FCSTD DOCUMENT  (FreeCAD 0.18R16131 (Git))
Label: Escriba
License: All rights reserved
LicenseURL: http://en.wikipedia.org/wiki/All_rights_reserved
objects: Part::Feature×205, Sketcher::SketchObject×65, App::Part×62, Part::Cylinder×43, Part::Cut×39, PartDesign::Pocket×28, Part::FeaturePython×28, Part::Box×26, Part::Chamfer×22, PartDesign::Pad×16, App::DocumentObjectGroup×14, Part::Revolution×13, Part::MultiFuse×8, PartDesign::Chamfer×8, PartDesign::Revolution×8, Part::Fuse×6, Part::Compound×1, Part::Fillet×1, Mesh::Feature×1
note: 569 computed .brp shape members not serialized (recipe doc carries the construction recipe); baked Part::Feature solids carry a one-line shape summary decoded from their .brp

FEATURE [Part::Cylinder] Cylinder  label="Rod-001"
  Angle = 360
  AttacherType = Attacher::AttachEngine3D
  Height = 500
  Placement = pos=(90,23,26) rot=(0,1,0;1.5708rad)
  Radius = 4
FEATURE [Part::Cylinder] Cylinder001  label="Rod-002"
  Angle = 360
  AttacherType = Attacher::AttachEngine3D
  Height = 500
  Placement = pos=(90,97,26) rot=(0,1,0;1.5708rad)
  Radius = 4
FEATURE [Part::Cylinder] Cylinder002  label="Rod-003"
  Angle = 360
  AttacherType = Attacher::AttachEngine3D
  Height = 350
  Placement = pos=(18,336,14.75) rot=(1,0,0;1.5708rad)
  Radius = 4
FEATURE [Part::Cylinder] Cylinder003  label="Rod-004"
  Angle = 360
  AttacherType = Attacher::AttachEngine3D
  Height = 350
  Placement = pos=(53,336,14.75) rot=(1,0,0;1.5708rad)
  Radius = 4
FEATURE [Part::Compound] Compound001  label="extruder-motor"
  Placement = pos=(109.65,-100.5,-442) rot=(0,0,1;0rad)
FEATURE [Sketcher::SketchObject] Sketch007  label="bottom-part-sketch"
  MapMode = 5
  sketch-geometry (8):
    g0: LineSegment StartX=-16.65 StartY=-21.15 StartZ=0 EndX=16.65 EndY=-21.15 EndZ=0
    g1: LineSegment StartX=21.15 StartY=-16.65 StartZ=0 EndX=21.15 EndY=16.65 EndZ=0
    g2: LineSegment StartX=16.65 StartY=21.15 StartZ=0 EndX=-16.65 EndY=21.15 EndZ=0
    g3: LineSegment StartX=-21.15 StartY=16.65 StartZ=0 EndX=-21.15 EndY=-16.65 EndZ=0
    g4: ArcOfCircle CenterX=0 CenterY=0 CenterZ=0 NormalX=0 NormalY=0 NormalZ=1 AngleXU=0 Radius=26.9174 StartAngle=2.2377 EndAngle=2.47468
    g5: ArcOfCircle CenterX=0 CenterY=0 CenterZ=0 NormalX=0 NormalY=0 NormalZ=1 AngleXU=0 Radius=26.9174 StartAngle=3.8085 EndAngle=4.04548
    g6: ArcOfCircle CenterX=0 CenterY=0 CenterZ=0 NormalX=0 NormalY=0 NormalZ=1 AngleXU=0 Radius=26.9174 StartAngle=5.3793 EndAngle=5.61628
    g7: ArcOfCircle CenterX=0 CenterY=0 CenterZ=0 NormalX=0 NormalY=0 NormalZ=1 AngleXU=0 Radius=26.9174 StartAngle=0.666908 EndAngle=0.903888
  constraints (29):
    c: Horizontal(g0)
    c: Horizontal(g2)
    c: Vertical(g1)
    c: Vertical(g3)
    c: PointOnObject(g0,g4)
    c: PointOnObject(g0,g4)
    c: PointOnObject(g1,g4)
    c: PointOnObject(g1,g4)
    c: Coincident(g4,g2)
    c: Coincident(g7,g2)
    c: Equal(g4,g5)
    c: Coincident(g4,g3)
    c: Coincident(g5,g3)
    c: Coincident(g4,g5)
    c: Equal(g5,g6)
    c: PointOnObject(g5,g0)
    c: PointOnObject(g6,g0)
    c: Coincident(g5,g6)
    c: Equal(g6,g7)
    c: PointOnObject(g6,g1)
    c: PointOnObject(g7,g1)
    c: Coincident(g6,g7)
    c: Equal(g3,g2)
    c: Equal(g2,g1)
    c: Equal(g1,g0)
    c: DistanceX(g3,g1) = 42.3
    c: DistanceX(g2) = -33.3
    c: DistanceY(g2) = 21.15
    c: DistanceX(g1) = 21.15
FEATURE [PartDesign::Pad] Pad002  label="bottom-slice"
  Length = 9.6
  Length2 = 100
  Profile = -> Sketch007
  Type = 0
FEATURE [Sketcher::SketchObject] Sketch008  label="middle-part-sketch"
  ExternalGeometry = -> [Pad002]
  MapMode = 5
  Placement = pos=(0,0,9.6) rot=(0,0,1;0rad)
  Support = -> [Pad002]
  sketch-geometry (9):
    g0: LineSegment StartX=-21 StartY=-13.75 StartZ=0 EndX=-21 EndY=13.75 EndZ=0
    g1: LineSegment StartX=-21 StartY=13.75 StartZ=0 EndX=-13.75 EndY=21 EndZ=0
    g2: LineSegment StartX=-13.75 StartY=21 StartZ=0 EndX=13.75 EndY=21 EndZ=0
    g3: LineSegment [constr] StartX=-21 StartY=13.75 StartZ=0 EndX=-9 EndY=13.75 EndZ=0
    g4: LineSegment StartX=13.75 StartY=21 StartZ=0 EndX=21 EndY=13.75 EndZ=0
    g5: LineSegment StartX=21 StartY=13.75 StartZ=0 EndX=21 EndY=-13.75 EndZ=0
    g6: LineSegment StartX=21 StartY=-13.75 StartZ=0 EndX=13.75 EndY=-21 EndZ=0
    g7: LineSegment StartX=13.75 StartY=-21 StartZ=0 EndX=-13.75 EndY=-21 EndZ=0
    g8: LineSegment StartX=-13.75 StartY=-21 StartZ=0 EndX=-21 EndY=-13.75 EndZ=0
  constraints (24):
    c: Coincident(g0,g1)
    c: Coincident(g1,g2)
    c: Horizontal(g2)
    c: Symmetric(g0,g0,g-1)
    c: Symmetric(g1,g2,g-2)
    c: Horizontal(g3)
    c: Coincident(g3,g0)
    c: DistanceX(g3) = 12
    c: Angle(g3,g1) = 0.785398
    c: DistanceY(g0) = 27.5
    c: Coincident(g4,g5)
    c: Vertical(g5)
    c: Coincident(g5,g6)
    c: Coincident(g6,g7)
    c: Horizontal(g7)
    c: Coincident(g7,g8)
    c: Coincident(g8,g0)
    c: Symmetric(g1,g7,g-1)
    c: Coincident(g4,g2)
    c: Symmetric(g4,g0,g-2)
    c: Symmetric(g0,g5,g-2)
    c: Symmetric(g6,g7,g-2)
    c: DistanceX(g-1,g0) = -21
    c: Equal(g0,g2)
FEATURE [PartDesign::Pad] Pad003  label="middle-slice"
  Length = 22.75
  Length2 = 100
  Profile = -> Sketch008
  Type = 0
FEATURE [Sketcher::SketchObject] Sketch009  label="top-part-sketch"
  MapMode = 5
  Placement = pos=(0,0,32.35) rot=(0,0,1;0rad)
  Support = -> [Pad003]
  sketch-geometry (8):
    g0: LineSegment StartX=-16.65 StartY=-21.15 StartZ=0 EndX=16.65 EndY=-21.15 EndZ=0
    g1: LineSegment StartX=21.15 StartY=-16.65 StartZ=0 EndX=21.15 EndY=16.65 EndZ=0
    g2: LineSegment StartX=16.65 StartY=21.15 StartZ=0 EndX=-16.65 EndY=21.15 EndZ=0
    g3: LineSegment StartX=-21.15 StartY=16.65 StartZ=0 EndX=-21.15 EndY=-16.65 EndZ=0
    g4: ArcOfCircle CenterX=0 CenterY=0 CenterZ=0 NormalX=0 NormalY=0 NormalZ=1 AngleXU=0 Radius=26.9174 StartAngle=2.2377 EndAngle=2.47468
    g5: ArcOfCircle CenterX=0 CenterY=0 CenterZ=0 NormalX=0 NormalY=0 NormalZ=1 AngleXU=0 Radius=26.9174 StartAngle=3.8085 EndAngle=4.04548
    g6: ArcOfCircle CenterX=0 CenterY=0 CenterZ=0 NormalX=0 NormalY=0 NormalZ=1 AngleXU=0 Radius=26.9174 StartAngle=5.3793 EndAngle=5.61628
    g7: ArcOfCircle CenterX=0 CenterY=0 CenterZ=0 NormalX=0 NormalY=0 NormalZ=1 AngleXU=0 Radius=26.9174 StartAngle=0.666908 EndAngle=0.903888
  constraints (29):
    c: Horizontal(g0)
    c: Horizontal(g2)
    c: Vertical(g1)
    c: Vertical(g3)
    c: PointOnObject(g0,g4)
    c: PointOnObject(g0,g4)
    c: PointOnObject(g1,g4)
    c: PointOnObject(g1,g4)
    c: Coincident(g4,g2)
    c: Coincident(g7,g2)
    c: Equal(g4,g5)
    c: Coincident(g4,g3)
    c: Coincident(g5,g3)
    c: Coincident(g4,g5)
    c: Equal(g5,g6)
    c: PointOnObject(g5,g0)
    c: PointOnObject(g6,g0)
    c: Coincident(g5,g6)
    c: Equal(g6,g7)
    c: PointOnObject(g6,g1)
    c: PointOnObject(g7,g1)
    c: Coincident(g6,g7)
    c: Equal(g3,g2)
    c: Equal(g2,g1)
    c: Equal(g1,g0)
    c: DistanceX(g3,g1) = 42.3
    c: DistanceX(g2) = -33.3
    c: DistanceY(g2) = 21.15
    c: DistanceX(g1) = 21.15
FEATURE [PartDesign::Pad] Pad004  label="top-slice"
  Length = 7.75
  Length2 = 100
  Profile = -> Sketch009
  Type = 0
FEATURE [Sketcher::SketchObject] Sketch010  label="top-drills-sketch"
  MapMode = 5
  Placement = pos=(0,0,40.1) rot=(0,0,1;0rad)
  Support = -> [Pad004]
  sketch-geometry (6):
    g0: LineSegment [constr] StartX=-15.5 StartY=15.5 StartZ=0 EndX=15.5 EndY=15.5 EndZ=0
    g1: LineSegment [constr] StartX=-15.5 StartY=15.5 StartZ=0 EndX=-15.5 EndY=-15.5 EndZ=0
    g2: Circle CenterX=-15.5 CenterY=15.5 CenterZ=0 NormalX=0 NormalY=0 NormalZ=1 AngleXU=0 Radius=1.225
    g3: Circle CenterX=15.5 CenterY=15.5 CenterZ=0 NormalX=0 NormalY=0 NormalZ=1 AngleXU=0 Radius=1.225
    g4: Circle CenterX=15.5 CenterY=-15.5 CenterZ=0 NormalX=0 NormalY=0 NormalZ=1 AngleXU=0 Radius=1.225
    g5: Circle CenterX=-15.5 CenterY=-15.5 CenterZ=0 NormalX=0 NormalY=0 NormalZ=1 AngleXU=0 Radius=1.225
  constraints (15):
    c: Horizontal(g0)
    c: Symmetric(g0,g0,g-2)
    c: Vertical(g1)
    c: Symmetric(g1,g1,g-1)
    c: Equal(g0,g1)
    c: DistanceX(g0) = 31
    c: Coincident(g1,g0)
    c: Radius(g2) = 1.225
    c: Coincident(g2,g0)
    c: Equal(g5,g4)
    c: Equal(g4,g3)
    c: Equal(g3,g2)
    c: Coincident(g3,g0)
    c: Coincident(g5,g1)
    c: Symmetric(g4,g1,g-2)
FEATURE [PartDesign::Pocket] Pocket003  label="top-drills"
  Length = 4.5
  Length2 = 100
  Profile = -> Sketch010
  Type = 0
FEATURE [Sketcher::SketchObject] Sketch011  label="shaft-base-sketch"
  MapMode = 5
  Placement = pos=(0,0,40.1) rot=(0,0,1;0rad)
  Support = -> [Pocket003]
  sketch-geometry (2):
    g0: Circle CenterX=0 CenterY=0 CenterZ=0 NormalX=0 NormalY=0 NormalZ=1 AngleXU=0 Radius=11
    g1: Circle CenterX=0 CenterY=0 CenterZ=0 NormalX=0 NormalY=0 NormalZ=1 AngleXU=0 Radius=5
  constraints (4):
    c: Coincident(g0,g-1)
    c: Radius(g0) = 11
    c: Coincident(g1,g-1)
    c: Radius(g1) = 5
FEATURE [PartDesign::Pad] Pad005  label="shaft-base"
  Length = 2
  Length2 = 100
  Profile = -> Sketch011
  Type = 0
FEATURE [Sketcher::SketchObject] Sketch012  label="shaft-1-sketch"
  MapMode = 5
  Placement = pos=(0,0,40.1) rot=(0,0,1;0rad)
  Support = -> [Pad005]
  sketch-geometry (1):
    g0: Circle CenterX=0 CenterY=0 CenterZ=0 NormalX=0 NormalY=0 NormalZ=1 AngleXU=0 Radius=2.5
  constraints (2):
    c: Coincident(g0,g-1)
    c: Radius(g0) = 2.5
FEATURE [PartDesign::Pad] Pad006  label="shaft-1"
  Length = 20
  Length2 = 100
  Profile = -> Sketch012
  Type = 0
FEATURE [Sketcher::SketchObject] Sketch013  label="shaft-2-sketch"
  ExternalGeometry = -> [Pad006]
  MapMode = 5
  Placement = pos=(0,0,60.1) rot=(0,0,1;0rad)
  Support = -> [Pad006]
  sketch-geometry (4):
    g0: LineSegment StartX=-2 StartY=1.5 StartZ=0 EndX=-2 EndY=-1.5 EndZ=0
    g1: LineSegment StartX=-2 StartY=1.5 StartZ=0 EndX=-2.5 EndY=1.5 EndZ=0
    g2: LineSegment StartX=-2.5 StartY=1.5 StartZ=0 EndX=-2.5 EndY=-1.5 EndZ=0
    g3: LineSegment StartX=-2.5 StartY=-1.5 StartZ=0 EndX=-2 EndY=-1.5 EndZ=0
  constraints (12):
    c: Vertical(g0)
    c: Symmetric(g0,g0,g-1)
    c: PointOnObject(g0,g-3)
    c: Coincident(g1,g2)
    c: Coincident(g2,g3)
    c: Horizontal(g3)
    c: Horizontal(g1)
    c: Coincident(g1,g0)
    c: Coincident(g0,g3)
    c: Vertical(g2)
    c: Tangent(g2,g-3)
    c: DistanceX(g1) = -0.5
FEATURE [PartDesign::Pocket] Pocket004  label="shaft-2"
  Length = 17
  Length2 = 100
  Profile = -> Sketch013
  Type = 0
FEATURE [Sketcher::SketchObject] Sketch014  label="bottom-drills-sketch"
  MapMode = 5
  Placement = pos=(0,0,0) rot=(1,0,0;3.14159rad)
  Support = -> [Pocket004]
  sketch-geometry (7):
    g0: LineSegment [constr] StartX=-15.5 StartY=15.5 StartZ=0 EndX=15.5 EndY=15.5 EndZ=0
    g1: LineSegment [constr] StartX=-15.5 StartY=15.5 StartZ=0 EndX=-15.5 EndY=-15.5 EndZ=0
    g2: Circle CenterX=-15.5 CenterY=15.5 CenterZ=0 NormalX=0 NormalY=0 NormalZ=1 AngleXU=0 Radius=1.5
    g3: Circle CenterX=15.5 CenterY=15.5 CenterZ=0 NormalX=0 NormalY=0 NormalZ=1 AngleXU=0 Radius=1.5
    g4: Circle CenterX=15.5 CenterY=-15.5 CenterZ=0 NormalX=0 NormalY=0 NormalZ=1 AngleXU=0 Radius=1.5
    g5: Circle CenterX=-15.5 CenterY=-15.5 CenterZ=0 NormalX=0 NormalY=0 NormalZ=1 AngleXU=0 Radius=1.5
    g6: Circle CenterX=0 CenterY=0 CenterZ=0 NormalX=0 NormalY=0 NormalZ=1 AngleXU=0 Radius=4.5
  constraints (17):
    c: Horizontal(g0)
    c: Vertical(g1)
    c: Coincident(g1,g0)
    c: Symmetric(g0,g0,g-2)
    c: Symmetric(g0,g1,g-1)
    c: Equal(g1,g0)
    c: DistanceX(g0) = 31
    c: Coincident(g2,g0)
    c: Radius(g2) = 1.5
    c: Coincident(g5,g1)
    c: Coincident(g0,g3)
    c: Equal(g3,g2)
    c: Equal(g2,g5)
    c: Equal(g5,g4)
    c: Symmetric(g4,g1,g-2)
    c: Coincident(g6,g-1)
    c: Radius(g6) = 4.5
FEATURE [PartDesign::Pocket] Pocket005  label="bottom-drills"
  Length = 3
  Length2 = 100
  Profile = -> Sketch014
  Type = 0
FEATURE [Part::Chamfer] Chamfer004  label="motor-no-connector"
  Base = -> Pocket005
  Edges = 1 edges r=0.4: [Edge102]
FEATURE [Sketcher::SketchObject] Sketch015  label="connector-support-sketch"
  ExternalGeometry = -> [Chamfer004]
  MapMode = 5
  Placement = pos=(0,0,43.1) rot=(0,0,1;0rad)
  Support = -> [Chamfer004]
  sketch-geometry (4):
    g0: LineSegment StartX=21.15 StartY=8.2 StartZ=0 EndX=25.45 EndY=8.2 EndZ=0
    g1: LineSegment StartX=25.45 StartY=8.2 StartZ=0 EndX=25.45 EndY=-8.2 EndZ=0
    g2: LineSegment StartX=25.45 StartY=-8.2 StartZ=0 EndX=21.15 EndY=-8.2 EndZ=0
    g3: LineSegment StartX=21.15 StartY=-8.2 StartZ=0 EndX=21.15 EndY=8.2 EndZ=0
  constraints (12):
    c: Coincident(g0,g1)
    c: Coincident(g1,g2)
    c: Coincident(g2,g3)
    c: Coincident(g3,g0)
    c: Horizontal(g0)
    c: Horizontal(g2)
    c: Vertical(g1)
    c: Vertical(g3)
    c: Symmetric(g0,g2,g-1)
    c: PointOnObject(g0,g-3)
    c: DistanceY(g1) = -16.4
    c: DistanceX(g0) = 4.3
FEATURE [PartDesign::Pad] Pad007  label="connector-motor"
  Length = 3.6
  Length2 = 100
  Profile = -> Sketch015
  Reversed = true
  Type = 0
FEATURE [Sketcher::SketchObject] Sketch016  label="connector-slot-sketch"
  ExternalGeometry = -> [Pad007]
  MapMode = 5
  Placement = pos=(21.15,0,0) rot=(0.57735,-0.57735,-0.57735;2.0944rad)
  Support = -> [Pad007]
  sketch-geometry (4):
    g0: LineSegment StartX=-8.2 StartY=9.6 StartZ=0 EndX=8.2 EndY=9.6 EndZ=0
    g1: LineSegment StartX=8.2 StartY=9.6 StartZ=0 EndX=8.2 EndY=3.6 EndZ=0
    g2: LineSegment StartX=8.2 StartY=3.6 StartZ=0 EndX=-8.2 EndY=3.6 EndZ=0
    g3: LineSegment StartX=-8.2 StartY=3.6 StartZ=0 EndX=-8.2 EndY=9.6 EndZ=0
  constraints (11):
    c: Coincident(g0,g1)
    c: Coincident(g1,g2)
    c: Coincident(g2,g3)
    c: Coincident(g3,g0)
    c: Horizontal(g0)
    c: Horizontal(g2)
    c: Vertical(g1)
    c: Vertical(g3)
    c: Coincident(g2,g-3)
    c: Coincident(g1,g-3)
    c: PointOnObject(g0,g-4)
FEATURE [PartDesign::Pocket] Pocket006  label="connector-slot"
  Length = 1
  Length2 = 100
  Profile = -> Sketch016
  Type = 0
FEATURE [Sketcher::SketchObject] Sketch017  label="connector-main-body-sketch"
  MapMode = 5
  Placement = pos=(0,0,0) rot=(0.57735,0.57735,0.57735;2.0944rad)
  sketch-geometry (4):
    g0: LineSegment StartX=-7.5 StartY=3.05 StartZ=0 EndX=7.5 EndY=3.05 EndZ=0
    g1: LineSegment StartX=7.5 StartY=3.05 StartZ=0 EndX=7.5 EndY=-3.05 EndZ=0
    g2: LineSegment StartX=7.5 StartY=-3.05 StartZ=0 EndX=-7.5 EndY=-3.05 EndZ=0
    g3: LineSegment StartX=-7.5 StartY=-3.05 StartZ=0 EndX=-7.5 EndY=3.05 EndZ=0
  constraints (11):
    c: Coincident(g0,g1)
    c: Coincident(g1,g2)
    c: Coincident(g2,g3)
    c: Coincident(g3,g0)
    c: Horizontal(g0)
    c: Horizontal(g2)
    c: Vertical(g1)
    c: Vertical(g3)
    c: Symmetric(g0,g1,g-1)
    c: DistanceX(g0) = 15
    c: DistanceY(g1) = -6.1
FEATURE [PartDesign::Pad] Pad008  label="connector-main-body"
  Length = 6.7
  Length2 = 100
  Placement = pos=(0,0,0) rot=(0.57735,0.57735,0.57735;2.0944rad)
  Profile = -> Sketch017
  Type = 0
FEATURE [Sketcher::SketchObject] Sketch018  label="connector-cutout-1-sketch"
  MapMode = 5
  Placement = pos=(6.7,0,0) rot=(0.57735,0.57735,0.57735;2.0944rad)
  Support = -> [Pad008]
  sketch-geometry (8):
    g0: LineSegment StartX=-6.5 StartY=1.85 StartZ=0 EndX=-3.22738 EndY=1.85 EndZ=0
    g1: LineSegment StartX=6.5 StartY=1.85 StartZ=0 EndX=6.5 EndY=-1.85 EndZ=0
    g2: LineSegment StartX=6.5 StartY=-1.85 StartZ=0 EndX=-6.5 EndY=-1.85 EndZ=0
    g3: LineSegment StartX=-6.5 StartY=-1.85 StartZ=0 EndX=-6.5 EndY=1.85 EndZ=0
    g4: LineSegment StartX=-3.22738 StartY=1.85 StartZ=0 EndX=-3.22738 EndY=3.85 EndZ=0
    g5: LineSegment StartX=-3.22738 StartY=3.85 StartZ=0 EndX=3.22738 EndY=3.85 EndZ=0
    g6: LineSegment StartX=3.22738 StartY=3.85 StartZ=0 EndX=3.22738 EndY=1.85 EndZ=0
    g7: LineSegment StartX=3.22738 StartY=1.85 StartZ=0 EndX=6.5 EndY=1.85 EndZ=0
  constraints (21):
    c: Coincident(g7,g1)
    c: Coincident(g1,g2)
    c: Coincident(g2,g3)
    c: Coincident(g3,g0)
    c: Horizontal(g0)
    c: Horizontal(g2)
    c: Vertical(g1)
    c: Vertical(g3)
    c: Symmetric(g0,g1,g-1)
    c: DistanceX(g2) = -13
    c: DistanceY(g1) = -3.7
    c: Vertical(g4)
    c: Coincident(g4,g5)
    c: Horizontal(g5)
    c: Coincident(g5,g6)
    c: Vertical(g6)
    c: Symmetric(g4,g5,g-2)
    c: Coincident(g0,g4)
    c: Coincident(g7,g6)
    c: Tangent(g0,g7)
    c: DistanceY(g6) = -2
FEATURE [PartDesign::Pocket] Pocket007  label="connector-cutout-1"
  Length = 4.6
  Length2 = 100
  Placement = pos=(0,0,0) rot=(0.57735,0.57735,0.57735;2.0944rad)
  Profile = -> Sketch018
  Type = 0
FEATURE [Part::Box] Box  label="pin-master"
  AttacherType = Attacher::AttachEngine3D
  Height = 0.5
  Length = 4
  Width = 0.5
FEATURE [Part::FeaturePython] Array  label="pins"  # Draft array (typed FeaturePython)
  Angle = 360
  ArrayType = 0
  Axis = (0,0,1)
  Base = -> Box
  Center = (0,0,0)
  IntervalX = (1,0,0)
  IntervalY = (0,2,0)
  IntervalZ = (0,0,1)
  NumberPolar = 1
  NumberX = 1
  NumberY = 6
  NumberZ = 1
  Placement = pos=(2,-5.3,0) rot=(0,0,1;0rad)
FEATURE [App::DocumentObjectGroup] Group  label="connector-src"
  Group = -> [Pad008,Pocket007,Array]
FEATURE [Part::MultiFuse] Fusion001  label="connector"
  Placement = pos=(20.15,1e-15,6.65) rot=(0,0,1;0rad)
  Shapes = -> [Pocket007,Array]
FEATURE [Part::MultiFuse] Fusion002  label="Motor-with-connector"
  Shapes = -> [Pocket006,Fusion001]
FEATURE [Part::Feature] Fusion001001  label="Motor-with-connector-final002"
  Placement = pos=(509,0,0) rot=(0.707107,0.707107,0;3.14159rad)
  shape: bbox 42.3 x 48 x 60.1 mm, 110 faces (baked)
FEATURE [Part::Feature] Fusion001002  label="Motor-with-connector-final001"
  Placement = pos=(-3,0,0) rot=(0.707107,0.707107,0;3.14159rad)
  shape: bbox 42.3 x 48 x 60.1 mm, 110 faces (baked)
FEATURE [App::Part] Part003  label="Steppers"
  Group = -> [Compound001,Group,Pocket006,Fusion001,Sketch008,Sketch014,Pad002,Sketch007,Pad007,Pocket004,Sketch017,Sketch015,Sketch016,Sketch013,Sketch009,Chamfer004,Sketch010,Pad003,Sketch012,Pocket007,Sketch011,Pad008,Box,Pad004,Pad006,Pocket003,Pad005,Array,Sketch018,Pocket005,Fusion002,Fusion001001,Fusion001002]
  License = CC BY 3.0
  LicenseURL = http://creativecommons.org/licenses/by/3.0/
  Origin = -> Origin003
  Placement = pos=(97.85,60,108.6) rot=(0,0,1;0rad)
FEATURE [Part::Box] Box001  label="Cubo"
  AttacherType = Attacher::AttachEngine3D
  Height = 22.7
  Length = 11.8
  Width = 22.5
FEATURE [Part::Box] Box002  label="Cubo001"
  AttacherType = Attacher::AttachEngine3D
  Height = 2.5
  Length = 11.8
  Placement = pos=(0,-4.7,15.9) rot=(0,0,1;0rad)
  Width = 32.4
FEATURE [Part::Fuse] Fusion001003  label="Square_body"
  Base = -> Box001
  Tool = -> Box002
FEATURE [Part::Cylinder] Cylinder006  label="Cilindro"
  Angle = 360
  AttacherType = Attacher::AttachEngine3D
  Height = 4
  Placement = pos=(5.9,16.6,22.7) rot=(0,0,1;0rad)
  Radius = 5.9
FEATURE [Part::Cylinder] Cylinder007  label="Cilindro001"
  Angle = 360
  AttacherType = Attacher::AttachEngine3D
  Height = 4
  Placement = pos=(5.9,10.3,22.7) rot=(0,0,1;0rad)
  Radius = 2.5
FEATURE [Part::Fuse] Fusion001004
  Base = -> Cylinder006
  Tool = -> Cylinder007
FEATURE [Part::Fuse] Fusion003
  Base = -> Fusion001003
  Tool = -> Fusion001004
FEATURE [Part::Cylinder] Cylinder008  label="Taladro"
  Angle = 360
  AttacherType = Attacher::AttachEngine3D
  Height = 10
  Placement = pos=(5.9,-2.35,11) rot=(0,0,1;0rad)
  Radius = 1
FEATURE [Part::Cylinder] Cylinder009  label="Taladro2"
  Angle = 360
  AttacherType = Attacher::AttachEngine3D
  Height = 10
  Placement = pos=(5.9,24.85,11) rot=(0,0,1;0rad)
  Radius = 1
FEATURE [Part::Fuse] Fusion004  label="Taladros"
  Base = -> Cylinder008
  Tool = -> Cylinder009
FEATURE [Part::Box] Box003  label="Cubo002"
  AttacherType = Attacher::AttachEngine3D
  Height = 10
  Length = 1.3
  Placement = pos=(5.25,-6,12) rot=(0,0,1;0rad)
  Width = 3.3
FEATURE [Part::Box] Box004  label="Cubo003"
  AttacherType = Attacher::AttachEngine3D
  Height = 10
  Length = 1.3
  Placement = pos=(5.25,25,12) rot=(0,0,1;0rad)
  Width = 3.3
FEATURE [Part::Fuse] Fusion005  label="Rebajes"
  Base = -> Box003
  Tool = -> Box004
FEATURE [Part::Fuse] Fusion006  label="Taladros001"
  Base = -> Fusion004
  Tool = -> Fusion005
FEATURE [Part::Cut] Cut002  label="Cuerpo_con_taladros"
  Base = -> Fusion003
  Placement = pos=(-5.9,0,0) rot=(0,0,1;0rad)
  Tool = -> Fusion006
FEATURE [Sketcher::SketchObject] Sketch019
  MapMode = 5
  Placement = pos=(-5.9,22.5,0) rot=(0,0.707107,0.707107;3.14159rad)
  Support = -> [Cut002]
  sketch-geometry (4):
    g0: LineSegment StartX=-4.1 StartY=4.5 StartZ=0 EndX=-7.7 EndY=4.5 EndZ=0
    g1: LineSegment StartX=-7.7 StartY=4.5 StartZ=0 EndX=-7.7 EndY=5.7 EndZ=0
    g2: LineSegment StartX=-7.7 StartY=5.7 StartZ=0 EndX=-4.1 EndY=5.7 EndZ=0
    g3: LineSegment StartX=-4.1 StartY=5.7 StartZ=0 EndX=-4.1 EndY=4.5 EndZ=0
  constraints (12):
    c: Coincident(g0,g1)
    c: Coincident(g1,g2)
    c: Coincident(g2,g3)
    c: Coincident(g3,g0)
    c: Horizontal(g0)
    c: Horizontal(g2)
    c: Vertical(g1)
    c: Vertical(g3)
    c: DistanceX(g2) = 3.6
    c: DistanceY(g1) = 1.2
    c: DistanceX(g-1,g0) = -4.1
    c: DistanceY(g-1,g0) = 4.5
FEATURE [PartDesign::Pocket] Pocket008  label="Ranura_cable"
  Length = 3
  Length2 = 100
  Placement = pos=(-5.9,0,0) rot=(0,0,1;0rad)
  Profile = -> Sketch019
  Type = 0
FEATURE [Part::Cylinder] Cylinder010  label="Cilindro002"
  Angle = 360
  AttacherType = Attacher::AttachEngine3D
  Height = 3
  Placement = pos=(2.51021,16.5511,26.9) rot=(0,0,1;0rad)
  Radius = 0.35
FEATURE [Part::FeaturePython] Array001  # Draft array (typed FeaturePython)
  Angle = 360
  ArrayType = 1
  Axis = (0,0,1)
  Base = -> Cylinder010
  Center = (0,16.6,0)
  Fuse = false
  IntervalAxis = (0,0,0)
  IntervalX = (1,0,0)
  IntervalY = (0,1,0)
  IntervalZ = (0,0,0)
  NumberPolar = 20
  NumberX = 2
  NumberY = 2
  NumberZ = 1
FEATURE [Part::Cylinder] Cylinder011  label="Cilindro_interior"
  Angle = 360
  AttacherType = Attacher::AttachEngine3D
  Height = 3.2
  Placement = pos=(0,16.6,26.7) rot=(0,0,1;0rad)
  Radius = 2.3
FEATURE [Part::Cylinder] Cylinder012  label="Cilindro_exterior"
  Angle = 360
  AttacherType = Attacher::AttachEngine3D
  Height = 3.2
  Placement = pos=(0,16.6,26.7) rot=(0,0,1;0rad)
  Radius = 0.85
FEATURE [Part::Cut] Cut003  label="Cilindro_vaciado"
  Base = -> Cylinder011
  Tool = -> Cylinder012
FEATURE [Part::Fillet] Fillet
  Base = -> Cut003
  Edges = 1 edges r=0.3: [Edge1]
FEATURE [Part::Cut] Cut004  label="Eje_engranaje"
  Base = -> Fillet
  Tool = -> Array001
FEATURE [App::DocumentObjectGroup] Grupo003  label="Servo"
  Group = -> [Cut002,Pocket008,Cut004]
FEATURE [Part::Feature] Fusion007001  label="Servo-sg90-final"
  shape: bbox 11.8 x 32.4 x 29.9 mm, 77 faces (baked)
FEATURE [App::Part] Part004  label="Servinho"
  Group = -> [Fusion001004,Cylinder006,Cut002,Cylinder007,Cylinder010,Fusion006,Cylinder009,Box002,Cylinder011,Fillet,Box004,Cylinder008,Fusion004,Cut003,Array001,Fusion005,Box003,Cut004,Sketch019,Pocket008,Box001,Cylinder012,Fusion003,Fusion001003,Grupo003,Fusion007001]
  License = CC BY 3.0
  LicenseURL = http://creativecommons.org/licenses/by/3.0/
  Origin = -> Origin004
  Placement = pos=(-48,0,0) rot=(0,0,1;0rad)
FEATURE [Part::Feature] Part__Feature035  label="RES0805 v011"
  Placement = pos=(12.5,-1.605,-6.045) rot=(1,0,0;1.5708rad)
  shape: bbox 0.4 x 0.5 x 1.25 mm, 15 faces (baked)
FEATURE [Part::Feature] Part__Feature029  label="RES0805 v005"
  Placement = pos=(12.5,-1.605,-0.245) rot=(1,0,0;1.5708rad)
  shape: bbox 1.9 x 0.4 x 1.25 mm, 10 faces (baked)
FEATURE [Part::Feature] Part__Feature023  label="BL-LS0805UWC v004"
  Placement = pos=(26.5,0.0068546,-2.40685) rot=(-1,0,0;1.5708rad)
  shape: bbox 0.1999 x 0.199 x 0.1999 mm, 6 faces (baked)
FEATURE [Part::Feature] Part__Feature033  label="RES0805 v009"
  Placement = pos=(12.5,-1.605,-6.045) rot=(1,0,0;1.5708rad)
  shape: bbox 1.9 x 0.4 x 1.25 mm, 10 faces (baked)
FEATURE [Part::Feature] Part__Feature025  label="RES0805 v1"
  Placement = pos=(27,0.005,-0.255) rot=(-1,0,0;1.5708rad)
  shape: bbox 1.9 x 0.4 x 1.25 mm, 10 faces (baked)
FEATURE [Part::Feature] Part__Feature042  label="COMPOUND005"
  shape: bbox 1.7 x 0.6509 x 1.7 mm, 7 faces (baked)
FEATURE [Part::Feature] Part__Feature021  label="Header 3 pin v008"
  Placement = pos=(29.4117,-1.60424,-3.01166) rot=(0.707107,0,0.707107;3.14159rad)
  shape: bbox 0.6 x 9.1 x 0.6 mm, 10 faces (baked)
FEATURE [Part::Feature] Part__Feature044  label="COMPOUND007"
  shape: bbox 1.7 x 0.6509 x 1.7 mm, 7 faces (baked)
FEATURE [Part::Feature] Part__Feature030  label="RES0805 v006"
  Placement = pos=(12.5,-1.605,-0.245) rot=(1,0,0;1.5708rad)
  shape: bbox 1.2 x 0.05 x 1.25 mm, 6 faces (baked)
FEATURE [Part::Feature] Part__Feature026  label="RES0805 v002"
  Placement = pos=(27,0.005,-0.255) rot=(-1,0,0;1.5708rad)
  shape: bbox 1.2 x 0.05 x 1.25 mm, 6 faces (baked)
FEATURE [Part::Feature] Part__Feature037  label="COMPOUND"
  shape: bbox 24.5 x 14.7 x 6.01 mm, 397 faces (baked)
FEATURE [Part::Feature] Part__Feature028  label="RES0805 v004"
  Placement = pos=(27,0.005,-0.255) rot=(-1,0,0;1.5708rad)
  shape: bbox 0.4 x 0.5 x 1.25 mm, 15 faces (baked)
FEATURE [Part::Feature] Part__Feature032  label="RES0805 v008"
  Placement = pos=(12.5,-1.605,-0.245) rot=(1,0,0;1.5708rad)
  shape: bbox 0.4 x 0.5 x 1.25 mm, 15 faces (baked)
FEATURE [Part::Feature] Part__Feature045  label="COMPOUND008"
  shape: bbox 1.7 x 0.6509 x 1.7 mm, 7 faces (baked)
FEATURE [Part::Feature] Part__Feature019  label="Header 3 pin v006"
  Placement = pos=(29.4117,-1.60424,-3.01166) rot=(0.707107,0,0.707107;3.14159rad)
  shape: bbox 0.6 x 9.1 x 0.6 mm, 10 faces (baked)
FEATURE [Part::Feature] Part__Feature034  label="RES0805 v010"
  Placement = pos=(12.5,-1.605,-6.045) rot=(1,0,0;1.5708rad)
  shape: bbox 1.2 x 0.05 x 1.25 mm, 6 faces (baked)
FEATURE [Part::Feature] Part__Feature043  label="COMPOUND006"
  shape: bbox 1.7 x 0.6509 x 1.7 mm, 7 faces (baked)
FEATURE [Part::Feature] Part__Feature038  label="COMPOUND001"
  shape: bbox 33 x 1.6 x 10.1 mm, 24 faces (baked)
FEATURE [Part::Feature] Part__Feature040  label="COMPOUND003"
  shape: bbox 1.795 x 0.7 x 1.795 mm, 3 faces (baked)
FEATURE [Part::Feature] Part__Feature036  label="RES0805 v012"
  Placement = pos=(12.5,-1.605,-6.045) rot=(1,0,0;1.5708rad)
  shape: bbox 0.4 x 0.5 x 1.25 mm, 15 faces (baked)
FEATURE [Part::Feature] Part__Feature041  label="COMPOUND004"
  shape: bbox 1.795 x 0.7 x 1.795 mm, 3 faces (baked)
FEATURE [Part::Feature] Part__Feature039  label="COMPOUND002"
  shape: bbox 1.795 x 0.7 x 1.795 mm, 3 faces (baked)
FEATURE [Part::Feature] Part__Feature031  label="RES0805 v007"
  Placement = pos=(12.5,-1.605,-0.245) rot=(1,0,0;1.5708rad)
  shape: bbox 0.4 x 0.5 x 1.25 mm, 15 faces (baked)
FEATURE [Part::Feature] Part__Feature024  label="BL-LS0805UWC v005"
  Placement = pos=(26.5,0.0068546,-2.40685) rot=(-1,0,0;1.5708rad)
  shape: bbox 1.8 x 0.301 x 1.25 mm, 30 faces (baked)
FEATURE [Part::Feature] Part__Feature020  label="Header 3 pin v007"
  Placement = pos=(29.4117,-1.60424,-3.01166) rot=(0.707107,0,0.707107;3.14159rad)
  shape: bbox 0.6 x 9.1 x 0.6 mm, 10 faces (baked)
FEATURE [Part::Feature] Part__Feature027  label="RES0805 v003"
  Placement = pos=(27,0.005,-0.255) rot=(-1,0,0;1.5708rad)
  shape: bbox 0.4 x 0.5 x 1.25 mm, 15 faces (baked)
FEATURE [Part::Feature] Part__Feature022  label="BL-LS0805UWC v3"
  Placement = pos=(26.5,0.0068546,-2.40685) rot=(-1,0,0;1.5708rad)
  shape: bbox 1.4 x 0.499 x 1.25 mm, 11 faces (baked)
FEATURE [Part::Feature] Part__Feature018  label="Header 3 pin v5"
  Placement = pos=(29.4117,-1.60424,-3.01166) rot=(0.707107,0,0.707107;3.14159rad)
  shape: bbox 5.9 x 7 x 10.16 mm, 44 faces (baked)
FEATURE [App::Part] Part005  label="TCST2103"
  Group = -> [Part__Feature045,Part__Feature033,Part__Feature030,Part__Feature024,Part__Feature028,Part__Feature029,Part__Feature026,Part__Feature027,Part__Feature025,Part__Feature031,Part__Feature032,Part__Feature039,Part__Feature041,Part__Feature023,Part__Feature034,Part__Feature037,Part__Feature035,Part__Feature018,Part__Feature022,Part__Feature020,Part__Feature021,Part__Feature019,Part__Feature036,+5 more]
  License = CC BY 3.0
  LicenseURL = http://creativecommons.org/licenses/by/3.0/
  Origin = -> Origin005
  Placement = pos=(93,38,54) rot=(0.57735,0.57735,-0.57735;2.0944rad)
FEATURE [Part::Feature] Arduino_UNO
  Placement = pos=(-36.508,0.214012,94.725) rot=(0,0,1;0rad)
  shape: bbox 68.2 x 1.55 x 53.05 mm, 23 faces, 0 solids (baked)
FEATURE [Part::Feature] Arduino_UNO001
  Placement = pos=(-33.508,1.76401,48.375) rot=(0,0,1;0rad)
  shape: bbox 9.475 x 3.104 x 6.2 mm, 73 faces, 0 solids (baked)
FEATURE [Part::Feature] Arduino_UNO002
  Placement = pos=(-8.15803,1.76401,83.425) rot=(0,0,1;0rad)
  shape: bbox 35.6 x 4.9 x 9.9 mm, 18 faces, 0 solids (baked)
FEATURE [Part::Feature] Arduino_UNO003
  Placement = pos=(-7.75803,5.66401,81.875) rot=(0,0,1;0rad)
  shape: bbox 35.62 x 3.2 x 7.279 mm, 10 faces, 0 solids (baked)
FEATURE [Part::Feature] Arduino_UNO004
  Placement = pos=(-7.55448,4.26401,82.5715) rot=(0,0,1;0rad)
  shape: bbox 1.1 x 3 x 0.5 mm, 10 faces, 0 solids (baked)
FEATURE [Part::Feature] Arduino_UNO005
  Placement = pos=(25.7455,4.26401,82.5715) rot=(0,0,1;0rad)
  shape: bbox 1.1 x 3 x 0.5 mm, 10 faces, 0 solids (baked)
FEATURE [Part::Feature] Arduino_UNO006 .. Arduino_UNO017  x12 (patterned run collapsed; names and placements below)
  shape: bbox 1.6 x 3 x 0.5 mm, 10 faces, 0 solids (baked)
  placements: 12 in arithmetic series — first pos=(-5.45448,4.26401,82.5715) rot=(0,0,1;0rad), step (2.6,0,0), last pos=(23.1455,4.26401,82.5715) rot=(0,0,1;0rad)
FEATURE [Part::Feature] Arduino_UNO018
  Placement = pos=(26.8455,4.26401,74.3785) rot=(0,1,0;3.14159rad)
  shape: bbox 1.1 x 3 x 0.5 mm, 10 faces, 0 solids (baked)
FEATURE [Part::Feature] Arduino_UNO019 .. Arduino_UNO030  x12 (patterned run collapsed; names and placements below)
  shape: bbox 1.6 x 3 x 0.5 mm, 10 faces, 0 solids (baked)
  placements: 12 in arithmetic series — first pos=(24.7455,4.26401,74.3785) rot=(0,1,0;3.14159rad), step (-2.6,0,0), last pos=(-3.85448,4.26401,74.3785) rot=(0,1,0;3.14159rad)
FEATURE [Part::Feature] Arduino_UNO031
  Placement = pos=(-6.45448,4.26401,74.3785) rot=(0,1,0;3.14159rad)
  shape: bbox 1.1 x 3 x 0.5 mm, 10 faces, 0 solids (baked)
FEATURE [Part::Feature] Arduino_UNO032
  Placement = pos=(-14.658,1.76401,88.925) rot=(0,1,0;1.5708rad)
  shape: bbox 6.55 x 5.529 x 12.08 mm, 55 faces, 0 solids (baked)
FEATURE [Part::Feature] Arduino_UNO033
  Placement = pos=(-7.60803,1.76401,88.925) rot=(0,1,0;1.5708rad)
  shape: bbox 6.55 x 5.529 x 12.08 mm, 55 faces, 0 solids (baked)
FEATURE [Part::Feature] Arduino_UNO034
  Placement = pos=(-20.808,1.76401,68.375) rot=(0,0,1;0rad)
  shape: bbox 15.38 x 3.463 x 4.513 mm, 27 faces, 0 solids (baked)
FEATURE [Part::Feature] Arduino_UNO035
  Placement = pos=(25.492,1.76401,70.375) rot=(0,0,1;0rad)
  shape: bbox 5 x 11.6 x 7.4 mm, 188 faces, 0 solids (baked)
FEATURE [Part::Feature] Arduino_UNO036
  Placement = pos=(-10.308,1.76401,93.525) rot=(0,0,1;0rad)
  shape: bbox 47.95 x 11.7 x 50.9 mm, 600 faces, 0 solids (baked)
FEATURE [Part::Feature] Arduino_UNO037
  Placement = pos=(-14.208,1.76401,62.675) rot=(0,1,0;1.5708rad)
  shape: bbox 5 x 0.9 x 5 mm, 9 faces, 0 solids (baked)
FEATURE [Part::Feature] Arduino_UNO038
  Placement = pos=(-27.208,1.76401,74.225) rot=(0,1,0;3.14159rad)
  shape: bbox 7.764 x 1.9 x 6 mm, 73 faces, 0 solids (baked)
FEATURE [Part::Feature] Arduino_UNO039
  Placement = pos=(-26.808,1.76401,62.575) rot=(0,0,1;0rad)
  shape: bbox 16.3 x 15 x 13.1 mm, 84 faces, 0 solids (baked)
FEATURE [Part::Feature] Arduino_UNO040
  Placement = pos=(-38.608,1.76401,91.125) rot=(0,0,1;0rad)
  shape: bbox 14.86 x 14.9 x 9.825 mm, 124 faces, 0 solids (baked)
FEATURE [Part::Feature] Arduino_UNO041
  Placement = pos=(-22.008,1.76401,45.975) rot=(0,-1,0;1.5708rad)
  shape: bbox 7.4 x 11.6 x 5 mm, 188 faces, 0 solids (baked)
FEATURE [Part::Feature] Arduino_UNO042
  Placement = pos=(-17.208,1.76401,93.425) rot=(0,0,1;0rad)
  shape: bbox 5.688 x 2.22 x 2.6 mm, 62 faces, 0 solids (baked)
FEATURE [App::Part] Part001  label="Arduino"
  Group = -> [Arduino_UNO,Arduino_UNO001,Arduino_UNO002,Arduino_UNO003,Arduino_UNO004,Arduino_UNO005,Arduino_UNO006,Arduino_UNO007,Arduino_UNO008,Arduino_UNO009,Arduino_UNO010,Arduino_UNO011,Arduino_UNO012,Arduino_UNO013,Arduino_UNO014,Arduino_UNO015,Arduino_UNO016,Arduino_UNO017,Arduino_UNO018,Arduino_UNO019,Arduino_UNO020,Arduino_UNO021,Arduino_UNO022,Arduino_UNO023,Arduino_UNO024,Arduino_UNO025,+17 more]
  License = CC BY 3.0
  LicenseURL = http://creativecommons.org/licenses/by/3.0/
  Origin = -> Origin001
  Placement = pos=(100,83,20.8) rot=(0.57735,-0.57735,-0.57735;2.0944rad)
FEATURE [Part::Box] Box005  label="Cube"
  AttacherType = Attacher::AttachEngine3D
  Height = 5.75
  Length = 105
  Placement = pos=(0,0,0.25) rot=(0,0,1;0rad)
  Width = 120
FEATURE [Sketcher::SketchObject] Sketch021
  MapMode = 5
  sketch-geometry (8):
    g0: LineSegment StartX=-2.75 StartY=-1.58771 StartZ=0 EndX=-2.75 EndY=1.58771 EndZ=0
    g1: LineSegment StartX=-2.75 StartY=1.58771 StartZ=0 EndX=0 EndY=3.17543 EndZ=0
    g2: LineSegment StartX=0 StartY=3.17543 StartZ=0 EndX=2.75 EndY=1.58771 EndZ=0
    g3: LineSegment StartX=2.75 StartY=1.58771 StartZ=0 EndX=2.75 EndY=-1.58771 EndZ=0
    g4: LineSegment StartX=2.75 StartY=-1.58771 StartZ=0 EndX=0 EndY=-3.17543 EndZ=0
    g5: LineSegment StartX=0 StartY=-3.17543 StartZ=0 EndX=-2.75 EndY=-1.58771 EndZ=0
    g6: LineSegment [constr] StartX=-2.75 StartY=1.58771 StartZ=0 EndX=2.75 EndY=-1.58771 EndZ=0
    g7: GeomPoint [constr] X=0 Y=0 Z=0
  constraints (22):
    c: Vertical(g0)
    c: Coincident(g0,g1)
    c: Coincident(g1,g2)
    c: Coincident(g2,g3)
    c: Vertical(g3)
    c: Coincident(g3,g4)
    c: Coincident(g4,g5)
    c: Coincident(g5,g0)
    c: PointOnObject(g4,g-2)
    c: PointOnObject(g1,g-2)
    c: Equal(g1,g2)
    c: Equal(g2,g3)
    c: Equal(g3,g4)
    c: Equal(g4,g5)
    c: Equal(g5,g0)
    c: DistanceX(g0,g3) = 5.5
    c: Distance(g4,g2) = 5.5
    c: Coincident(g6,g0)
    c: Coincident(g6,g3)
    c: PointOnObject(g7,g6)
    c: PointOnObject(g7,g-2)
    c: Coincident(g7,g-1)
FEATURE [PartDesign::Pad] Pad
  Length = 15
  Length2 = 4
  Profile = -> Sketch021
  Type = 0
FEATURE [Sketcher::SketchObject] Sketch022
  MapMode = 5
  Placement = pos=(0,0,0) rot=(1,0,0;3.14159rad)
  Support = -> [Pad]
  sketch-geometry (1):
    g0: Circle CenterX=0 CenterY=0 CenterZ=0 NormalX=0 NormalY=0 NormalZ=1 AngleXU=0 Radius=1.5
  constraints (1):
    c: Radius(g0) = 1.5
FEATURE [PartDesign::Pad] Pad001
  Length = 6
  Length2 = 4
  Profile = -> Sketch022
  Type = 0
FEATURE [Sketcher::SketchObject] Sketch023
  MapMode = 5
  Placement = pos=(0,0,15) rot=(0,0,1;0rad)
  Support = -> [Pad001]
  sketch-geometry (1):
    g0: Circle CenterX=0 CenterY=0 CenterZ=0 NormalX=0 NormalY=0 NormalZ=1 AngleXU=0 Radius=1.5
  constraints (2):
    c: Coincident(g0,g-1)
    c: Radius(g0) = 1.5
FEATURE [PartDesign::Pocket] Pocket009
  Length = 8.5
  Length2 = 100
  Profile = -> Sketch023
  Type = 0
FEATURE [PartDesign::Chamfer] Chamfer005
  Base = -> Pocket009 [Edge24]
  Size = 1.5
FEATURE [PartDesign::Chamfer] Chamfer006
  Base = -> Chamfer005 [Edge26]
  Size = 0.5
FEATURE [App::Part] Part007  label="Hex-Standoff-M3-15mm001"
  Group = -> [Pad001,Chamfer005,Pocket009,Pad,Sketch023,Sketch021,Sketch022,Chamfer006]
  License = CC BY 3.0
  LicenseURL = http://creativecommons.org/licenses/by/3.0/
  Origin = -> Origin007
  Placement = pos=(12.9,53.7,21) rot=(0,1,0;-3.14159rad)
FEATURE [Sketcher::SketchObject] Sketch025
  MapMode = 5
  sketch-geometry (8):
    g0: LineSegment StartX=-2.75 StartY=-1.58771 StartZ=0 EndX=-2.75 EndY=1.58771 EndZ=0
    g1: LineSegment StartX=-2.75 StartY=1.58771 StartZ=0 EndX=0 EndY=3.17543 EndZ=0
    g2: LineSegment StartX=0 StartY=3.17543 StartZ=0 EndX=2.75 EndY=1.58771 EndZ=0
    g3: LineSegment StartX=2.75 StartY=1.58771 StartZ=0 EndX=2.75 EndY=-1.58771 EndZ=0
    g4: LineSegment StartX=2.75 StartY=-1.58771 StartZ=0 EndX=0 EndY=-3.17543 EndZ=0
    g5: LineSegment StartX=0 StartY=-3.17543 StartZ=0 EndX=-2.75 EndY=-1.58771 EndZ=0
    g6: LineSegment [constr] StartX=-2.75 StartY=1.58771 StartZ=0 EndX=2.75 EndY=-1.58771 EndZ=0
    g7: GeomPoint [constr] X=0 Y=0 Z=0
  constraints (22):
    c: Vertical(g0)
    c: Coincident(g0,g1)
    c: Coincident(g1,g2)
    c: Coincident(g2,g3)
    c: Vertical(g3)
    c: Coincident(g3,g4)
    c: Coincident(g4,g5)
    c: Coincident(g5,g0)
    c: PointOnObject(g4,g-2)
    c: PointOnObject(g1,g-2)
    c: Equal(g1,g2)
    c: Equal(g2,g3)
    c: Equal(g3,g4)
    c: Equal(g4,g5)
    c: Equal(g5,g0)
    c: DistanceX(g0,g3) = 5.5
    c: Distance(g4,g2) = 5.5
    c: Coincident(g6,g0)
    c: Coincident(g6,g3)
    c: PointOnObject(g7,g6)
    c: PointOnObject(g7,g-2)
    c: Coincident(g7,g-1)
FEATURE [PartDesign::Pad] Pad010
  Length = 15
  Length2 = 4
  Profile = -> Sketch025
  Type = 0
FEATURE [Sketcher::SketchObject] Sketch026
  MapMode = 5
  Placement = pos=(0,0,0) rot=(1,0,0;3.14159rad)
  Support = -> [Pad010]
  sketch-geometry (1):
    g0: Circle CenterX=0 CenterY=0 CenterZ=0 NormalX=0 NormalY=0 NormalZ=1 AngleXU=0 Radius=1.5
  constraints (1):
    c: Radius(g0) = 1.5
FEATURE [PartDesign::Pad] Pad009
  Length = 6
  Length2 = 4
  Profile = -> Sketch026
  Type = 0
FEATURE [Sketcher::SketchObject] Sketch024
  MapMode = 5
  Placement = pos=(0,0,15) rot=(0,0,1;0rad)
  Support = -> [Pad009]
  sketch-geometry (1):
    g0: Circle CenterX=0 CenterY=0 CenterZ=0 NormalX=0 NormalY=0 NormalZ=1 AngleXU=0 Radius=1.5
  constraints (2):
    c: Coincident(g0,g-1)
    c: Radius(g0) = 1.5
FEATURE [PartDesign::Pocket] Pocket010
  Length = 8.5
  Length2 = 100
  Profile = -> Sketch024
  Type = 0
FEATURE [PartDesign::Chamfer] Chamfer008
  Base = -> Pocket010 [Edge24]
  Size = 1.5
FEATURE [PartDesign::Chamfer] Chamfer007
  Base = -> Chamfer008 [Edge26]
  Size = 0.5
FEATURE [App::Part] Part009  label="Hex-Standoff-M3-15mm002"
  Group = -> [Pad009,Chamfer008,Pocket010,Pad010,Sketch024,Sketch025,Sketch026,Chamfer007]
  License = CC BY 3.0
  LicenseURL = http://creativecommons.org/licenses/by/3.0/
  Origin = -> Origin009
  Placement = pos=(7.67,105.9,21) rot=(0,1,0;-3.14159rad)
FEATURE [Sketcher::SketchObject] Sketch027
  MapMode = 5
  sketch-geometry (8):
    g0: LineSegment StartX=-2.75 StartY=-1.58771 StartZ=0 EndX=-2.75 EndY=1.58771 EndZ=0
    g1: LineSegment StartX=-2.75 StartY=1.58771 StartZ=0 EndX=0 EndY=3.17543 EndZ=0
    g2: LineSegment StartX=0 StartY=3.17543 StartZ=0 EndX=2.75 EndY=1.58771 EndZ=0
    g3: LineSegment StartX=2.75 StartY=1.58771 StartZ=0 EndX=2.75 EndY=-1.58771 EndZ=0
    g4: LineSegment StartX=2.75 StartY=-1.58771 StartZ=0 EndX=0 EndY=-3.17543 EndZ=0
    g5: LineSegment StartX=0 StartY=-3.17543 StartZ=0 EndX=-2.75 EndY=-1.58771 EndZ=0
    g6: LineSegment [constr] StartX=-2.75 StartY=1.58771 StartZ=0 EndX=2.75 EndY=-1.58771 EndZ=0
    g7: GeomPoint [constr] X=0 Y=0 Z=0
  constraints (22):
    c: Vertical(g0)
    c: Coincident(g0,g1)
    c: Coincident(g1,g2)
    c: Coincident(g2,g3)
    c: Vertical(g3)
    c: Coincident(g3,g4)
    c: Coincident(g4,g5)
    c: Coincident(g5,g0)
    c: PointOnObject(g4,g-2)
    c: PointOnObject(g1,g-2)
    c: Equal(g1,g2)
    c: Equal(g2,g3)
    c: Equal(g3,g4)
    c: Equal(g4,g5)
    c: Equal(g5,g0)
    c: DistanceX(g0,g3) = 5.5
    c: Distance(g4,g2) = 5.5
    c: Coincident(g6,g0)
    c: Coincident(g6,g3)
    c: PointOnObject(g7,g6)
    c: PointOnObject(g7,g-2)
    c: Coincident(g7,g-1)
FEATURE [PartDesign::Pad] Pad012
  Length = 15
  Length2 = 4
  Profile = -> Sketch027
  Type = 0
FEATURE [Sketcher::SketchObject] Sketch029
  MapMode = 5
  Placement = pos=(0,0,0) rot=(1,0,0;3.14159rad)
  Support = -> [Pad012]
  sketch-geometry (1):
    g0: Circle CenterX=0 CenterY=0 CenterZ=0 NormalX=0 NormalY=0 NormalZ=1 AngleXU=0 Radius=1.5
  constraints (1):
    c: Radius(g0) = 1.5
FEATURE [PartDesign::Pad] Pad011
  Length = 6
  Length2 = 4
  Profile = -> Sketch029
  Type = 0
FEATURE [Sketcher::SketchObject] Sketch028
  MapMode = 5
  Placement = pos=(0,0,15) rot=(0,0,1;0rad)
  Support = -> [Pad011]
  sketch-geometry (1):
    g0: Circle CenterX=0 CenterY=0 CenterZ=0 NormalX=0 NormalY=0 NormalZ=1 AngleXU=0 Radius=1.5
  constraints (2):
    c: Coincident(g0,g-1)
    c: Radius(g0) = 1.5
FEATURE [PartDesign::Pocket] Pocket011
  Length = 8.5
  Length2 = 100
  Profile = -> Sketch028
  Type = 0
FEATURE [PartDesign::Chamfer] Chamfer009
  Base = -> Pocket011 [Edge24]
  Size = 1.5
FEATURE [PartDesign::Chamfer] Chamfer010
  Base = -> Chamfer009 [Edge26]
  Size = 0.5
FEATURE [App::Part] Part010  label="Hex-Standoff-M3-15mm003"
  Group = -> [Pad011,Chamfer009,Pocket011,Pad012,Sketch028,Sketch027,Sketch029,Chamfer010]
  License = CC BY 3.0
  LicenseURL = http://creativecommons.org/licenses/by/3.0/
  Origin = -> Origin010
  Placement = pos=(40.9,53.7,21) rot=(0,1,0;-3.14159rad)
FEATURE [Sketcher::SketchObject] Sketch030
  MapMode = 5
  sketch-geometry (8):
    g0: LineSegment StartX=-2.75 StartY=-1.58771 StartZ=0 EndX=-2.75 EndY=1.58771 EndZ=0
    g1: LineSegment StartX=-2.75 StartY=1.58771 StartZ=0 EndX=0 EndY=3.17543 EndZ=0
    g2: LineSegment StartX=0 StartY=3.17543 StartZ=0 EndX=2.75 EndY=1.58771 EndZ=0
    g3: LineSegment StartX=2.75 StartY=1.58771 StartZ=0 EndX=2.75 EndY=-1.58771 EndZ=0
    g4: LineSegment StartX=2.75 StartY=-1.58771 StartZ=0 EndX=0 EndY=-3.17543 EndZ=0
    g5: LineSegment StartX=0 StartY=-3.17543 StartZ=0 EndX=-2.75 EndY=-1.58771 EndZ=0
    g6: LineSegment [constr] StartX=-2.75 StartY=1.58771 StartZ=0 EndX=2.75 EndY=-1.58771 EndZ=0
    g7: GeomPoint [constr] X=0 Y=0 Z=0
  constraints (22):
    c: Vertical(g0)
    c: Coincident(g0,g1)
    c: Coincident(g1,g2)
    c: Coincident(g2,g3)
    c: Vertical(g3)
    c: Coincident(g3,g4)
    c: Coincident(g4,g5)
    c: Coincident(g5,g0)
    c: PointOnObject(g4,g-2)
    c: PointOnObject(g1,g-2)
    c: Equal(g1,g2)
    c: Equal(g2,g3)
    c: Equal(g3,g4)
    c: Equal(g4,g5)
    c: Equal(g5,g0)
    c: DistanceX(g0,g3) = 5.5
    c: Distance(g4,g2) = 5.5
    c: Coincident(g6,g0)
    c: Coincident(g6,g3)
    c: PointOnObject(g7,g6)
    c: PointOnObject(g7,g-2)
    c: Coincident(g7,g-1)
FEATURE [PartDesign::Pad] Pad014
  Length = 15
  Length2 = 4
  Profile = -> Sketch030
  Type = 0
FEATURE [Sketcher::SketchObject] Sketch032
  MapMode = 5
  Placement = pos=(0,0,0) rot=(1,0,0;3.14159rad)
  Support = -> [Pad014]
  sketch-geometry (1):
    g0: Circle CenterX=0 CenterY=0 CenterZ=0 NormalX=0 NormalY=0 NormalZ=1 AngleXU=0 Radius=1.5
  constraints (1):
    c: Radius(g0) = 1.5
FEATURE [PartDesign::Pad] Pad013
  Length = 6
  Length2 = 4
  Profile = -> Sketch032
  Type = 0
FEATURE [Sketcher::SketchObject] Sketch031
  MapMode = 5
  Placement = pos=(0,0,15) rot=(0,0,1;0rad)
  Support = -> [Pad013]
  sketch-geometry (1):
    g0: Circle CenterX=0 CenterY=0 CenterZ=0 NormalX=0 NormalY=0 NormalZ=1 AngleXU=0 Radius=1.5
  constraints (2):
    c: Coincident(g0,g-1)
    c: Radius(g0) = 1.5
FEATURE [PartDesign::Pocket] Pocket012
  Length = 8.5
  Length2 = 100
  Profile = -> Sketch031
  Type = 0
FEATURE [PartDesign::Chamfer] Chamfer011
  Base = -> Pocket012 [Edge24]
  Size = 1.5
FEATURE [PartDesign::Chamfer] Chamfer012
  Base = -> Chamfer011 [Edge26]
  Size = 0.5
FEATURE [App::Part] Part011  label="Hex-Standoff-M3-15mm004"
  Group = -> [Pad013,Chamfer011,Pocket012,Pad014,Sketch031,Sketch030,Sketch032,Chamfer012]
  License = CC BY 3.0
  LicenseURL = http://creativecommons.org/licenses/by/3.0/
  Origin = -> Origin011
  Placement = pos=(56,104.5,21) rot=(0,1,0;-3.14159rad)
FEATURE [Sketcher::SketchObject] Sketch033
  MapMode = 5
  Placement = pos=(0,0,0) rot=(1,0,0;1.5708rad)
  sketch-geometry (7):
    g0: LineSegment StartX=1.45 StartY=3 StartZ=0 EndX=2.75 EndY=3 EndZ=0
    g1: LineSegment StartX=2.75 StartY=3 StartZ=0 EndX=2.75 EndY=0 EndZ=0
    g2: LineSegment StartX=2.75 StartY=0 StartZ=0 EndX=1.5 EndY=0 EndZ=0
    g3: LineSegment StartX=1.5 StartY=0 StartZ=0 EndX=1.5 EndY=-10 EndZ=0
    g4: LineSegment StartX=1.5 StartY=-10 StartZ=0 EndX=0 EndY=-10 EndZ=0
    g5: LineSegment StartX=0 StartY=-10 StartZ=0 EndX=0 EndY=1.55 EndZ=0
    g6: LineSegment StartX=0 StartY=1.55 StartZ=0 EndX=1.45 EndY=3 EndZ=0
  constraints (21):
    c: Horizontal(g0)
    c: Coincident(g0,g1)
    c: Vertical(g1)
    c: Coincident(g1,g2)
    c: Horizontal(g2)
    c: Coincident(g2,g3)
    c: Vertical(g3)
    c: Coincident(g3,g4)
    c: Horizontal(g4)
    c: Coincident(g4,g5)
    c: Vertical(g5)
    c: Coincident(g0,g6)
    c: DistanceX(g4) = -1.5
    c: DistanceY(g1,g3) = -10
    c: Angle(g6,g0) = 2.35619
    c: DistanceY(g1) = -3
    c: DistanceX(g0,g5) = -2.75
    c: DistanceX(g0,g5) = -1.45
    c: PointOnObject(g1,g-1)
    c: PointOnObject(g5,g-2)
    c: Coincident(g6,g5)
FEATURE [PartDesign::Revolution] Revolution004  label="main-body"
  Angle = 360
  Axis = (0,0,1)
  Base = (0,0,0)
  Placement = pos=(0,0,0) rot=(1,0,0;1.5708rad)
  Profile = -> Sketch033
  ReferenceAxis = -> Sketch033 [V_Axis]
  Reversed = true
FEATURE [Sketcher::SketchObject] Sketch035  label="Sketch034"
  MapMode = 5
  Placement = pos=(0,0,0) rot=(1,0,0;1.5708rad)
  sketch-geometry (4):
    g0: LineSegment StartX=0 StartY=0.29908 StartZ=0 EndX=2.75 EndY=1.3 EndZ=0
    g1: LineSegment StartX=2.75 StartY=1.3 StartZ=0 EndX=2.75 EndY=10 EndZ=0
    g2: LineSegment StartX=2.75 StartY=10 StartZ=0 EndX=0 EndY=10 EndZ=0
    g3: LineSegment StartX=0 StartY=10 StartZ=0 EndX=0 EndY=0.29908 EndZ=0
  constraints (12):
    c: Coincident(g0,g1)
    c: Vertical(g1)
    c: Coincident(g1,g2)
    c: Horizontal(g2)
    c: Coincident(g2,g3)
    c: Vertical(g3)
    c: Coincident(g0,g3)
    c: DistanceX(g2) = -2.75
    c: PointOnObject(g0,g-2)
    c: DistanceY(g-1,g0) = 1.3
    c: DistanceY(g2) = 10
    c: Angle(g0,g3) = 1.22173
FEATURE [PartDesign::Revolution] Revolution005
  Angle = 360
  Axis = (0,0,1)
  Base = (0,0,0)
  Placement = pos=(0,0,0) rot=(1,0,0;1.5708rad)
  Profile = -> Sketch035
  ReferenceAxis = -> Sketch035 [V_Axis]
  Reversed = true
FEATURE [Sketcher::SketchObject] Sketch034  label="Hexagon001"
  ExternalGeometry = -> [Revolution005]
  MapMode = 5
  Placement = pos=(0,3.3e-15,10) rot=(0,0,1;3.14159rad)
  Support = -> [Revolution005]
  sketch-geometry (9):
    g0: LineSegment StartX=-0.721688 StartY=1.25 StartZ=0 EndX=0.721688 EndY=1.25 EndZ=0
    g1: LineSegment StartX=0.721688 StartY=1.25 StartZ=0 EndX=1.44338 EndY=0 EndZ=0
    g2: LineSegment StartX=1.44338 StartY=0 StartZ=0 EndX=0.721688 EndY=-1.25 EndZ=0
    g3: LineSegment StartX=0.721688 StartY=-1.25 StartZ=0 EndX=-0.721688 EndY=-1.25 EndZ=0
    g4: LineSegment StartX=-0.721688 StartY=-1.25 StartZ=0 EndX=-1.44338 EndY=0 EndZ=0
    g5: LineSegment StartX=-1.44338 StartY=0 StartZ=0 EndX=-0.721688 EndY=1.25 EndZ=0
    g6: Circle [constr] CenterX=0 CenterY=0 CenterZ=0 NormalX=0 NormalY=0 NormalZ=1 AngleXU=0 Radius=1.44338
    g7: Circle CenterX=0 CenterY=0 CenterZ=0 NormalX=0 NormalY=0 NormalZ=1 AngleXU=0 Radius=3.75
    g8: LineSegment [constr] StartX=0 StartY=3.75 StartZ=0 EndX=0 EndY=2.75 EndZ=0
  constraints (26):
    c: Horizontal(g0)
    c: Coincident(g0,g1)
    c: Coincident(g1,g2)
    c: Coincident(g2,g3)
    c: Horizontal(g3)
    c: Coincident(g3,g4)
    c: Coincident(g4,g5)
    c: Coincident(g5,g0)
    c: Equal(g5,g0)
    c: Equal(g0,g4)
    c: Equal(g4,g3)
    c: Equal(g3,g2)
    c: Equal(g2,g1)
    c: PointOnObject(g0,g6)
    c: PointOnObject(g2,g6)
    c: PointOnObject(g1,g6)
    c: PointOnObject(g4,g6)
    c: PointOnObject(g0,g6)
    c: DistanceY(g3,g0) = 2.5
    c: Coincident(g6,g-1)
    c: Coincident(g7,g-1)
    c: Vertical(g8)
    c: PointOnObject(g8,g7)
    c: PointOnObject(g8,g-2)
    c: DistanceY(g8) = -1
    c: PointOnObject(g8,g-3)
FEATURE [PartDesign::Pocket] Pocket013
  Length = 5
  Length2 = 100
  Placement = pos=(0,0,0) rot=(1,0,0;1.5708rad)
  Profile = -> Sketch034
  Type = 1
FEATURE [Part::Cut] Cut005
  Base = -> Revolution004
  Tool = -> Pocket013
FEATURE [Part::Chamfer] Chamfer013
  Base = -> Cut005
  Edges = 1 edges r=0.4: [Edge27]
FEATURE [Part::Chamfer] Chamfer014
  Base = -> Chamfer013
  Edges = 2 edges r=0.1: [Edge6,Edge7]
FEATURE [App::Part] Part012  label="Hex_Socket_Head_Cap_Screw_M3x10mm001"
  Group = -> [Cut005,Chamfer013,Sketch033,Revolution004,Pocket013,Revolution005,Sketch034,Sketch035,Chamfer014]
  License = CC BY 3.0
  LicenseURL = http://creativecommons.org/licenses/by/3.0/
  Origin = -> Origin012
  Placement = pos=(12.9,53.7,0.25) rot=(0,1,0;-3.14159rad)
FEATURE [Part::Cylinder] Cylinder013  label="Cilindro003"
  Angle = 360
  AttacherType = Attacher::AttachEngine3D
  Height = 7.6
  Placement = pos=(6.7,0,0) rot=(0,0,1;0rad)
  Radius = 0.6
FEATURE [Part::FeaturePython] Array002  # Draft array (typed FeaturePython)
  Angle = 360
  ArrayType = 1
  Axis = (0,0,1)
  Base = -> Cylinder013
  Center = (0,0,0)
  IntervalX = (1,0,0)
  IntervalY = (0,1,0)
  IntervalZ = (0,0,1)
  NumberPolar = 20
  NumberX = 2
  NumberY = 2
  NumberZ = 1
FEATURE [Part::Cylinder] Cylinder014  label="Cilindro004"
  Angle = 360
  AttacherType = Attacher::AttachEngine3D
  Height = 7.6
  Radius = 6.7
FEATURE [Part::Cut] Cut006
  Base = -> Cylinder014
  Placement = pos=(0,0,0.7) rot=(0,0,1;0rad)
  Tool = -> Array002
FEATURE [Part::Cylinder] Cylinder015  label="Cilindro005"
  Angle = 360
  AttacherType = Attacher::AttachEngine3D
  Height = 0.7
  Radius = 9
FEATURE [Part::Cylinder] Cylinder016  label="Cilindro006"
  Angle = 360
  AttacherType = Attacher::AttachEngine3D
  Height = 0.7
  Placement = pos=(0,0,8.3) rot=(0,0,1;0rad)
  Radius = 9
FEATURE [Part::Chamfer] Chamfer015
  Base = -> Cylinder015
  Edges = 1 edges r=0.2: [Edge1]
FEATURE [Part::Chamfer] Chamfer016
  Base = -> Cylinder016
  Edges = 1 edges r=0.2: [Edge3]
FEATURE [Part::MultiFuse] Fusion007002
  Shapes = -> [Cut006,Chamfer015,Chamfer016]
FEATURE [Part::Cylinder] Cylinder017  label="Cilindro007"
  Angle = 360
  AttacherType = Attacher::AttachEngine3D
  Height = 28.6
  Placement = pos=(0,0,-6) rot=(0,0,1;0rad)
  Radius = 2.5
FEATURE [Part::Cut] Cut007
  Base = -> Fusion007002
  Tool = -> Cylinder017
FEATURE [Part::Feature] Cut001001  label="GT2Pulley"
  shape: bbox 18 x 18 x 9 mm, 49 faces (baked)
FEATURE [Part::Cylinder] Cylinder018  label="Cilindro008"
  Angle = 360
  AttacherType = Attacher::AttachEngine3D
  Height = 7.6
  Placement = pos=(6.1,0,0) rot=(0,0,1;0rad)
  Radius = 0.6
FEATURE [Part::FeaturePython] Array003  # Draft array (typed FeaturePython)
  Angle = 360
  ArrayType = 1
  Axis = (0,0,1)
  Base = -> Cylinder018
  Center = (0,0,0)
  IntervalX = (1,0,0)
  IntervalY = (0,1,0)
  IntervalZ = (0,0,1)
  NumberPolar = 20
  NumberX = 2
  NumberY = 2
  NumberZ = 1
FEATURE [Part::Cylinder] Cylinder019  label="Cilindro009"
  Angle = 360
  AttacherType = Attacher::AttachEngine3D
  Height = 7.6
  Radius = 6.1
FEATURE [Part::Cut] Cut001002
  Base = -> Cylinder019
  Placement = pos=(0,0,1) rot=(0,0,1;0rad)
  Tool = -> Array003
FEATURE [Part::Cylinder] Cylinder020  label="Cilindro010"
  Angle = 360
  AttacherType = Attacher::AttachEngine3D
  Height = 1
  Radius = 9
FEATURE [Part::Cylinder] Cylinder021  label="Cilindro011"
  Angle = 360
  AttacherType = Attacher::AttachEngine3D
  Height = 6
  Placement = pos=(0,0,8.6) rot=(0,0,1;0rad)
  Radius = 9
FEATURE [Part::Cylinder] Cylinder022  label="Cilindro012"
  Angle = 360
  AttacherType = Attacher::AttachEngine3D
  Height = 14.6
  Radius = 2.5
FEATURE [Part::Chamfer] Chamfer017
  Base = -> Cylinder020
  Edges = 1 edges r=0.5: [Edge1]
FEATURE [Part::Chamfer] Chamfer018
  Base = -> Cylinder021
  Edges = 1 edges r=0.5: [Edge3]
FEATURE [Part::MultiFuse] Fusion007003
  Shapes = -> [Cut001002,Chamfer017,Chamfer018]
FEATURE [Part::Cut] Cut001003
  Base = -> Fusion007003
  Tool = -> Cylinder022
FEATURE [Part::Cylinder] Cylinder023  label="Cilindro013"
  Angle = 360
  AttacherType = Attacher::AttachEngine3D
  Height = 9
  Placement = pos=(1,0,12) rot=(0,1,0;1.5708rad)
  Radius = 1.5
FEATURE [Part::Cut] Cut001004
  Base = -> Cut001003
  Tool = -> Cylinder023
FEATURE [Part::Feature] Cut002001  label="Polea"
  Placement = pos=(94.85,60,40.6) rot=(0,0,-1;1.5708rad)
  shape: bbox 18 x 18 x 14.6 mm, 50 faces (baked)
FEATURE [Part::Cylinder] Cylinder024  label="Cilindro014"
  Angle = 360
  AttacherType = Attacher::AttachEngine3D
  Height = 6
  Placement = pos=(3,0,2.6) rot=(0,1,0;1.5708rad)
  Radius = 1.5
FEATURE [Part::Chamfer] Chamfer002
  Base = -> Cylinder024
  Edges = 2 edges r=0.25: [Edge1,Edge3]
FEATURE [Sketcher::SketchObject] Sketch038
  ExternalGeometry = -> [Chamfer002]
  MapMode = 5
  Placement = pos=(9,0,0) rot=(0.57735,0.57735,0.57735;2.0944rad)
  Support = -> [Chamfer002]
  sketch-geometry (9):
    g0: LineSegment StartX=-1 StartY=3.17735 StartZ=0 EndX=0 EndY=3.7547 EndZ=0
    g1: LineSegment StartX=0 StartY=3.7547 StartZ=0 EndX=1 EndY=3.17735 EndZ=0
    g2: LineSegment StartX=1 StartY=3.17735 StartZ=0 EndX=1 EndY=2.02265 EndZ=0
    g3: LineSegment StartX=1 StartY=2.02265 StartZ=0 EndX=0 EndY=1.4453 EndZ=0
    g4: LineSegment StartX=0 StartY=1.4453 StartZ=0 EndX=-1 EndY=2.02265 EndZ=0
    g5: LineSegment StartX=-1 StartY=2.02265 StartZ=0 EndX=-1 EndY=3.17735 EndZ=0
    g6: LineSegment [constr] StartX=0 StartY=2.6 StartZ=0 EndX=0 EndY=3.7547 EndZ=0
    g7: LineSegment [constr] StartX=0 StartY=2.6 StartZ=0 EndX=0 EndY=1.4453 EndZ=0
    g8: LineSegment [constr] StartX=0 StartY=2.6 StartZ=0 EndX=-1 EndY=3.17735 EndZ=0
  constraints (24):
    c: Coincident(g0,g1)
    c: Coincident(g1,g2)
    c: Coincident(g2,g3)
    c: Coincident(g3,g4)
    c: Coincident(g4,g5)
    c: Coincident(g5,g0)
    c: Vertical(g5)
    c: Vertical(g2)
    c: Equal(g0,g1)
    c: Equal(g1,g2)
    c: Equal(g2,g3)
    c: Equal(g3,g4)
    c: Equal(g4,g5)
    c: Coincident(g8,g-3)
    c: Coincident(g8,g6)
    c: Coincident(g8,g7)
    c: Coincident(g8,g0)
    c: Coincident(g6,g0)
    c: Coincident(g7,g3)
    c: Equal(g6,g8)
    c: Equal(g8,g7)
    c: Vertical(g6)
    c: Vertical(g7)
    c: DistanceX(g4,g2) = 2
FEATURE [PartDesign::Pocket] Pocket014  label="Tornillo"
  Length = 2.5
  Length2 = 100
  Profile = -> Sketch038
  Type = 0
FEATURE [Part::Feature] Pocket015  label="TornilloM3"
  Placement = pos=(0.5,0,0) rot=(0,0,1;0rad)
  shape: bbox 6 x 3 x 3 mm, 12 faces (baked)
FEATURE [Sketcher::SketchObject] Sketch039  label="Sketch042"
  MapMode = 5
  Placement = pos=(0,0,0) rot=(1,0,0;1.5708rad)
  sketch-geometry (4):
    g0: LineSegment StartX=0 StartY=0.29908 StartZ=0 EndX=2.75 EndY=1.3 EndZ=0
    g1: LineSegment StartX=2.75 StartY=1.3 StartZ=0 EndX=2.75 EndY=10 EndZ=0
    g2: LineSegment StartX=2.75 StartY=10 StartZ=0 EndX=0 EndY=10 EndZ=0
    g3: LineSegment StartX=0 StartY=10 StartZ=0 EndX=0 EndY=0.29908 EndZ=0
  constraints (12):
    c: Coincident(g0,g1)
    c: Vertical(g1)
    c: Coincident(g1,g2)
    c: Horizontal(g2)
    c: Coincident(g2,g3)
    c: Vertical(g3)
    c: Coincident(g0,g3)
    c: DistanceX(g2) = -2.75
    c: PointOnObject(g0,g-2)
    c: DistanceY(g-1,g0) = 1.3
    c: DistanceY(g2) = 10
    c: Angle(g0,g3) = 1.22173
FEATURE [Sketcher::SketchObject] Sketch040
  MapMode = 5
  Placement = pos=(0,0,0) rot=(1,0,0;1.5708rad)
  sketch-geometry (7):
    g0: LineSegment StartX=1.45 StartY=3 StartZ=0 EndX=2.75 EndY=3 EndZ=0
    g1: LineSegment StartX=2.75 StartY=3 StartZ=0 EndX=2.75 EndY=0 EndZ=0
    g2: LineSegment StartX=2.75 StartY=0 StartZ=0 EndX=1.5 EndY=0 EndZ=0
    g3: LineSegment StartX=1.5 StartY=0 StartZ=0 EndX=1.5 EndY=-10 EndZ=0
    g4: LineSegment StartX=1.5 StartY=-10 StartZ=0 EndX=0 EndY=-10 EndZ=0
    g5: LineSegment StartX=0 StartY=-10 StartZ=0 EndX=0 EndY=1.55 EndZ=0
    g6: LineSegment StartX=0 StartY=1.55 StartZ=0 EndX=1.45 EndY=3 EndZ=0
  constraints (21):
    c: Horizontal(g0)
    c: Coincident(g0,g1)
    c: Vertical(g1)
    c: Coincident(g1,g2)
    c: Horizontal(g2)
    c: Coincident(g2,g3)
    c: Vertical(g3)
    c: Coincident(g3,g4)
    c: Horizontal(g4)
    c: Coincident(g4,g5)
    c: Vertical(g5)
    c: Coincident(g0,g6)
    c: DistanceX(g4) = -1.5
    c: DistanceY(g1,g3) = -10
    c: Angle(g6,g0) = 2.35619
    c: DistanceY(g1) = -3
    c: DistanceX(g0,g5) = -2.75
    c: DistanceX(g0,g5) = -1.45
    c: PointOnObject(g1,g-1)
    c: PointOnObject(g5,g-2)
    c: Coincident(g6,g5)
FEATURE [PartDesign::Revolution] Revolution006  label="main-body001"
  Angle = 360
  Axis = (0,0,1)
  Base = (0,0,0)
  Placement = pos=(0,0,0) rot=(1,0,0;1.5708rad)
  Profile = -> Sketch040
  ReferenceAxis = -> Sketch040 [V_Axis]
  Reversed = true
FEATURE [PartDesign::Revolution] Revolution007
  Angle = 360
  Axis = (0,0,1)
  Base = (0,0,0)
  Placement = pos=(0,0,0) rot=(1,0,0;1.5708rad)
  Profile = -> Sketch039
  ReferenceAxis = -> Sketch039 [V_Axis]
  Reversed = true
FEATURE [Sketcher::SketchObject] Sketch041  label="Hexagon002"
  ExternalGeometry = -> [Revolution007]
  MapMode = 5
  Placement = pos=(0,3.3e-15,10) rot=(0,0,1;3.14159rad)
  Support = -> [Revolution007]
  sketch-geometry (9):
    g0: LineSegment StartX=-0.721688 StartY=1.25 StartZ=0 EndX=0.721688 EndY=1.25 EndZ=0
    g1: LineSegment StartX=0.721688 StartY=1.25 StartZ=0 EndX=1.44338 EndY=0 EndZ=0
    g2: LineSegment StartX=1.44338 StartY=0 StartZ=0 EndX=0.721688 EndY=-1.25 EndZ=0
    g3: LineSegment StartX=0.721688 StartY=-1.25 StartZ=0 EndX=-0.721688 EndY=-1.25 EndZ=0
    g4: LineSegment StartX=-0.721688 StartY=-1.25 StartZ=0 EndX=-1.44338 EndY=0 EndZ=0
    g5: LineSegment StartX=-1.44338 StartY=0 StartZ=0 EndX=-0.721688 EndY=1.25 EndZ=0
    g6: Circle [constr] CenterX=0 CenterY=0 CenterZ=0 NormalX=0 NormalY=0 NormalZ=1 AngleXU=0 Radius=1.44338
    g7: Circle CenterX=0 CenterY=0 CenterZ=0 NormalX=0 NormalY=0 NormalZ=1 AngleXU=0 Radius=3.75
    g8: LineSegment [constr] StartX=0 StartY=3.75 StartZ=0 EndX=0 EndY=2.75 EndZ=0
  constraints (26):
    c: Horizontal(g0)
    c: Coincident(g0,g1)
    c: Coincident(g1,g2)
    c: Coincident(g2,g3)
    c: Horizontal(g3)
    c: Coincident(g3,g4)
    c: Coincident(g4,g5)
    c: Coincident(g5,g0)
    c: Equal(g5,g0)
    c: Equal(g0,g4)
    c: Equal(g4,g3)
    c: Equal(g3,g2)
    c: Equal(g2,g1)
    c: PointOnObject(g0,g6)
    c: PointOnObject(g2,g6)
    c: PointOnObject(g1,g6)
    c: PointOnObject(g4,g6)
    c: PointOnObject(g0,g6)
    c: DistanceY(g3,g0) = 2.5
    c: Coincident(g6,g-1)
    c: Coincident(g7,g-1)
    c: Vertical(g8)
    c: PointOnObject(g8,g7)
    c: PointOnObject(g8,g-2)
    c: DistanceY(g8) = -1
    c: PointOnObject(g8,g-3)
FEATURE [PartDesign::Pocket] Pocket016
  Length = 5
  Length2 = 100
  Placement = pos=(0,0,0) rot=(1,0,0;1.5708rad)
  Profile = -> Sketch041
  Type = 1
FEATURE [Part::Cut] Cut002002
  Base = -> Revolution006
  Tool = -> Pocket016
FEATURE [Part::Chamfer] Chamfer020
  Base = -> Cut002002
  Edges = 1 edges r=0.4: [Edge27]
FEATURE [Part::Chamfer] Chamfer019
  Base = -> Chamfer020
  Edges = 2 edges r=0.1: [Edge6,Edge7]
FEATURE [App::Part] Part018  label="Hex_Socket_Head_Cap_Screw_M3x10mm002"
  Group = -> [Cut002002,Chamfer020,Sketch040,Revolution006,Pocket016,Revolution007,Sketch041,Sketch039,Chamfer019]
  License = CC BY 3.0
  LicenseURL = http://creativecommons.org/licenses/by/3.0/
  Origin = -> Origin018
  Placement = pos=(7.67,105.9,0.25) rot=(0,1,0;-3.14159rad)
FEATURE [Sketcher::SketchObject] Sketch045
  MapMode = 5
  Placement = pos=(0,0,0) rot=(1,0,0;1.5708rad)
  sketch-geometry (4):
    g0: LineSegment StartX=0 StartY=0.29908 StartZ=0 EndX=2.75 EndY=1.3 EndZ=0
    g1: LineSegment StartX=2.75 StartY=1.3 StartZ=0 EndX=2.75 EndY=10 EndZ=0
    g2: LineSegment StartX=2.75 StartY=10 StartZ=0 EndX=0 EndY=10 EndZ=0
    g3: LineSegment StartX=0 StartY=10 StartZ=0 EndX=0 EndY=0.29908 EndZ=0
  constraints (12):
    c: Coincident(g0,g1)
    c: Vertical(g1)
    c: Coincident(g1,g2)
    c: Horizontal(g2)
    c: Coincident(g2,g3)
    c: Vertical(g3)
    c: Coincident(g0,g3)
    c: DistanceX(g2) = -2.75
    c: PointOnObject(g0,g-2)
    c: DistanceY(g-1,g0) = 1.3
    c: DistanceY(g2) = 10
    c: Angle(g0,g3) = 1.22173
FEATURE [PartDesign::Revolution] Revolution011
  Angle = 360
  Axis = (0,0,1)
  Base = (0,0,0)
  Placement = pos=(0,0,0) rot=(1,0,0;1.5708rad)
  Profile = -> Sketch045
  ReferenceAxis = -> Sketch045 [V_Axis]
  Reversed = true
FEATURE [Sketcher::SketchObject] Sketch046
  MapMode = 5
  Placement = pos=(0,0,0) rot=(1,0,0;1.5708rad)
  sketch-geometry (7):
    g0: LineSegment StartX=1.45 StartY=3 StartZ=0 EndX=2.75 EndY=3 EndZ=0
    g1: LineSegment StartX=2.75 StartY=3 StartZ=0 EndX=2.75 EndY=0 EndZ=0
    g2: LineSegment StartX=2.75 StartY=0 StartZ=0 EndX=1.5 EndY=0 EndZ=0
    g3: LineSegment StartX=1.5 StartY=0 StartZ=0 EndX=1.5 EndY=-10 EndZ=0
    g4: LineSegment StartX=1.5 StartY=-10 StartZ=0 EndX=0 EndY=-10 EndZ=0
    g5: LineSegment StartX=0 StartY=-10 StartZ=0 EndX=0 EndY=1.55 EndZ=0
    g6: LineSegment StartX=0 StartY=1.55 StartZ=0 EndX=1.45 EndY=3 EndZ=0
  constraints (21):
    c: Horizontal(g0)
    c: Coincident(g0,g1)
    c: Vertical(g1)
    c: Coincident(g1,g2)
    c: Horizontal(g2)
    c: Coincident(g2,g3)
    c: Vertical(g3)
    c: Coincident(g3,g4)
    c: Horizontal(g4)
    c: Coincident(g4,g5)
    c: Vertical(g5)
    c: Coincident(g0,g6)
    c: DistanceX(g4) = -1.5
    c: DistanceY(g1,g3) = -10
    c: Angle(g6,g0) = 2.35619
    c: DistanceY(g1) = -3
    c: DistanceX(g0,g5) = -2.75
    c: DistanceX(g0,g5) = -1.45
    c: PointOnObject(g1,g-1)
    c: PointOnObject(g5,g-2)
    c: Coincident(g6,g5)
FEATURE [PartDesign::Revolution] Revolution010  label="main-body003"
  Angle = 360
  Axis = (0,0,1)
  Base = (0,0,0)
  Placement = pos=(0,0,0) rot=(1,0,0;1.5708rad)
  Profile = -> Sketch046
  ReferenceAxis = -> Sketch046 [V_Axis]
  Reversed = true
FEATURE [Sketcher::SketchObject] Sketch047  label="Hexagon004"
  ExternalGeometry = -> [Revolution011]
  MapMode = 5
  Placement = pos=(0,3.3e-15,10) rot=(0,0,1;3.14159rad)
  Support = -> [Revolution011]
  sketch-geometry (9):
    g0: LineSegment StartX=-0.721688 StartY=1.25 StartZ=0 EndX=0.721688 EndY=1.25 EndZ=0
    g1: LineSegment StartX=0.721688 StartY=1.25 StartZ=0 EndX=1.44338 EndY=0 EndZ=0
    g2: LineSegment StartX=1.44338 StartY=0 StartZ=0 EndX=0.721688 EndY=-1.25 EndZ=0
    g3: LineSegment StartX=0.721688 StartY=-1.25 StartZ=0 EndX=-0.721688 EndY=-1.25 EndZ=0
    g4: LineSegment StartX=-0.721688 StartY=-1.25 StartZ=0 EndX=-1.44338 EndY=0 EndZ=0
    g5: LineSegment StartX=-1.44338 StartY=0 StartZ=0 EndX=-0.721688 EndY=1.25 EndZ=0
    g6: Circle [constr] CenterX=0 CenterY=0 CenterZ=0 NormalX=0 NormalY=0 NormalZ=1 AngleXU=0 Radius=1.44338
    g7: Circle CenterX=0 CenterY=0 CenterZ=0 NormalX=0 NormalY=0 NormalZ=1 AngleXU=0 Radius=3.75
    g8: LineSegment [constr] StartX=0 StartY=3.75 StartZ=0 EndX=0 EndY=2.75 EndZ=0
  constraints (26):
    c: Horizontal(g0)
    c: Coincident(g0,g1)
    c: Coincident(g1,g2)
    c: Coincident(g2,g3)
    c: Horizontal(g3)
    c: Coincident(g3,g4)
    c: Coincident(g4,g5)
    c: Coincident(g5,g0)
    c: Equal(g5,g0)
    c: Equal(g0,g4)
    c: Equal(g4,g3)
    c: Equal(g3,g2)
    c: Equal(g2,g1)
    c: PointOnObject(g0,g6)
    c: PointOnObject(g2,g6)
    c: PointOnObject(g1,g6)
    c: PointOnObject(g4,g6)
    c: PointOnObject(g0,g6)
    c: DistanceY(g3,g0) = 2.5
    c: Coincident(g6,g-1)
    c: Coincident(g7,g-1)
    c: Vertical(g8)
    c: PointOnObject(g8,g7)
    c: PointOnObject(g8,g-2)
    c: DistanceY(g8) = -1
    c: PointOnObject(g8,g-3)
FEATURE [PartDesign::Pocket] Pocket018
  Length = 5
  Length2 = 100
  Placement = pos=(0,0,0) rot=(1,0,0;1.5708rad)
  Profile = -> Sketch047
  Type = 1
FEATURE [Part::Cut] Cut002004
  Base = -> Revolution010
  Tool = -> Pocket018
FEATURE [Part::Chamfer] Chamfer023
  Base = -> Cut002004
  Edges = 1 edges r=0.4: [Edge27]
FEATURE [Part::Chamfer] Chamfer024
  Base = -> Chamfer023
  Edges = 2 edges r=0.1: [Edge6,Edge7]
FEATURE [App::Part] Part020  label="Hex_Socket_Head_Cap_Screw_M3x10mm004"
  Group = -> [Cut002004,Chamfer023,Sketch046,Revolution010,Pocket018,Revolution011,Sketch047,Sketch045,Chamfer024]
  License = CC BY 3.0
  LicenseURL = http://creativecommons.org/licenses/by/3.0/
  Origin = -> Origin020
  Placement = pos=(40.9,53.7,0.25) rot=(0,1,0;-3.14159rad)
FEATURE [Sketcher::SketchObject] Sketch049
  MapMode = 5
  Placement = pos=(0,0,0) rot=(1,0,0;1.5708rad)
  sketch-geometry (7):
    g0: LineSegment StartX=1.45 StartY=3 StartZ=0 EndX=2.75 EndY=3 EndZ=0
    g1: LineSegment StartX=2.75 StartY=3 StartZ=0 EndX=2.75 EndY=0 EndZ=0
    g2: LineSegment StartX=2.75 StartY=0 StartZ=0 EndX=1.5 EndY=0 EndZ=0
    g3: LineSegment StartX=1.5 StartY=0 StartZ=0 EndX=1.5 EndY=-10 EndZ=0
    g4: LineSegment StartX=1.5 StartY=-10 StartZ=0 EndX=0 EndY=-10 EndZ=0
    g5: LineSegment StartX=0 StartY=-10 StartZ=0 EndX=0 EndY=1.55 EndZ=0
    g6: LineSegment StartX=0 StartY=1.55 StartZ=0 EndX=1.45 EndY=3 EndZ=0
  constraints (21):
    c: Horizontal(g0)
    c: Coincident(g0,g1)
    c: Vertical(g1)
    c: Coincident(g1,g2)
    c: Horizontal(g2)
    c: Coincident(g2,g3)
    c: Vertical(g3)
    c: Coincident(g3,g4)
    c: Horizontal(g4)
    c: Coincident(g4,g5)
    c: Vertical(g5)
    c: Coincident(g0,g6)
    c: DistanceX(g4) = -1.5
    c: DistanceY(g1,g3) = -10
    c: Angle(g6,g0) = 2.35619
    c: DistanceY(g1) = -3
    c: DistanceX(g0,g5) = -2.75
    c: DistanceX(g0,g5) = -1.45
    c: PointOnObject(g1,g-1)
    c: PointOnObject(g5,g-2)
    c: Coincident(g6,g5)
FEATURE [PartDesign::Revolution] Revolution012  label="main-body004"
  Angle = 360
  Axis = (0,0,1)
  Base = (0,0,0)
  Placement = pos=(0,0,0) rot=(1,0,0;1.5708rad)
  Profile = -> Sketch049
  ReferenceAxis = -> Sketch049 [V_Axis]
  Reversed = true
FEATURE [Sketcher::SketchObject] Sketch050
  MapMode = 5
  Placement = pos=(0,0,0) rot=(1,0,0;1.5708rad)
  sketch-geometry (4):
    g0: LineSegment StartX=0 StartY=0.29908 StartZ=0 EndX=2.75 EndY=1.3 EndZ=0
    g1: LineSegment StartX=2.75 StartY=1.3 StartZ=0 EndX=2.75 EndY=10 EndZ=0
    g2: LineSegment StartX=2.75 StartY=10 StartZ=0 EndX=0 EndY=10 EndZ=0
    g3: LineSegment StartX=0 StartY=10 StartZ=0 EndX=0 EndY=0.29908 EndZ=0
  constraints (12):
    c: Coincident(g0,g1)
    c: Vertical(g1)
    c: Coincident(g1,g2)
    c: Horizontal(g2)
    c: Coincident(g2,g3)
    c: Vertical(g3)
    c: Coincident(g0,g3)
    c: DistanceX(g2) = -2.75
    c: PointOnObject(g0,g-2)
    c: DistanceY(g-1,g0) = 1.3
    c: DistanceY(g2) = 10
    c: Angle(g0,g3) = 1.22173
FEATURE [PartDesign::Revolution] Revolution013
  Angle = 360
  Axis = (0,0,1)
  Base = (0,0,0)
  Placement = pos=(0,0,0) rot=(1,0,0;1.5708rad)
  Profile = -> Sketch050
  ReferenceAxis = -> Sketch050 [V_Axis]
  Reversed = true
FEATURE [Sketcher::SketchObject] Sketch048  label="Hexagon005"
  ExternalGeometry = -> [Revolution013]
  MapMode = 5
  Placement = pos=(0,3.3e-15,10) rot=(0,0,1;3.14159rad)
  Support = -> [Revolution013]
  sketch-geometry (9):
    g0: LineSegment StartX=-0.721688 StartY=1.25 StartZ=0 EndX=0.721688 EndY=1.25 EndZ=0
    g1: LineSegment StartX=0.721688 StartY=1.25 StartZ=0 EndX=1.44338 EndY=0 EndZ=0
    g2: LineSegment StartX=1.44338 StartY=0 StartZ=0 EndX=0.721688 EndY=-1.25 EndZ=0
    g3: LineSegment StartX=0.721688 StartY=-1.25 StartZ=0 EndX=-0.721688 EndY=-1.25 EndZ=0
    g4: LineSegment StartX=-0.721688 StartY=-1.25 StartZ=0 EndX=-1.44338 EndY=0 EndZ=0
    g5: LineSegment StartX=-1.44338 StartY=0 StartZ=0 EndX=-0.721688 EndY=1.25 EndZ=0
    g6: Circle [constr] CenterX=0 CenterY=0 CenterZ=0 NormalX=0 NormalY=0 NormalZ=1 AngleXU=0 Radius=1.44338
    g7: Circle CenterX=0 CenterY=0 CenterZ=0 NormalX=0 NormalY=0 NormalZ=1 AngleXU=0 Radius=3.75
    g8: LineSegment [constr] StartX=0 StartY=3.75 StartZ=0 EndX=0 EndY=2.75 EndZ=0
  constraints (26):
    c: Horizontal(g0)
    c: Coincident(g0,g1)
    c: Coincident(g1,g2)
    c: Coincident(g2,g3)
    c: Horizontal(g3)
    c: Coincident(g3,g4)
    c: Coincident(g4,g5)
    c: Coincident(g5,g0)
    c: Equal(g5,g0)
    c: Equal(g0,g4)
    c: Equal(g4,g3)
    c: Equal(g3,g2)
    c: Equal(g2,g1)
    c: PointOnObject(g0,g6)
    c: PointOnObject(g2,g6)
    c: PointOnObject(g1,g6)
    c: PointOnObject(g4,g6)
    c: PointOnObject(g0,g6)
    c: DistanceY(g3,g0) = 2.5
    c: Coincident(g6,g-1)
    c: Coincident(g7,g-1)
    c: Vertical(g8)
    c: PointOnObject(g8,g7)
    c: PointOnObject(g8,g-2)
    c: DistanceY(g8) = -1
    c: PointOnObject(g8,g-3)
FEATURE [PartDesign::Pocket] Pocket019
  Length = 5
  Length2 = 100
  Placement = pos=(0,0,0) rot=(1,0,0;1.5708rad)
  Profile = -> Sketch048
  Type = 1
FEATURE [Part::Cut] Cut002005
  Base = -> Revolution012
  Tool = -> Pocket019
FEATURE [Part::Chamfer] Chamfer026
  Base = -> Cut002005
  Edges = 1 edges r=0.4: [Edge27]
FEATURE [Part::Chamfer] Chamfer025
  Base = -> Chamfer026
  Edges = 2 edges r=0.1: [Edge6,Edge7]
FEATURE [App::Part] Part021  label="Hex_Socket_Head_Cap_Screw_M3x10mm005"
  Group = -> [Cut002005,Chamfer026,Sketch049,Revolution012,Pocket019,Revolution013,Sketch048,Sketch050,Chamfer025]
  License = CC BY 3.0
  LicenseURL = http://creativecommons.org/licenses/by/3.0/
  Origin = -> Origin021
  Placement = pos=(56,104.5,0.25) rot=(0,1,0;-3.14159rad)
FEATURE [Part::Box] Box006  label="Cube001"
  AttacherType = Attacher::AttachEngine3D
  Height = 50
  Length = 50
  Width = 50
FEATURE [Part::Box] Box007  label="Cube002"
  AttacherType = Attacher::AttachEngine3D
  Height = 50
  Length = 50
  Placement = pos=(5,-3,-5) rot=(0,0,1;0rad)
  Width = 58
FEATURE [Part::Cut] Cut002006
  Base = -> Box006
  Placement = pos=(66,35,18.5) rot=(0,0,1;0rad)
  Tool = -> Box007
FEATURE [Part::Cut] Cut002007
  Base = -> Box006
  Placement = pos=(635.68,85,18.5) rot=(0,0,1;3.14159rad)
  Tool = -> Box007
FEATURE [Part::Cut] Cut002008
  Base = -> Box006
  Placement = pos=(66,35,56) rot=(0,1,0;3.14159rad)
  Tool = -> Box007
FEATURE [Part::Cut] Cut002009
  Base = -> Box006
  Placement = pos=(590.68,85,6) rot=(0.707107,0,0.707107;3.14159rad)
  Tool = -> Box007
FEATURE [Part::Feature] Cut002010  label="Polea001"
  Placement = pos=(606.85,60,40.6) rot=(0,0,-1;1.5708rad)
  shape: bbox 18 x 18 x 14.6 mm, 50 faces (baked)
FEATURE [App::Part] Part017  label="GT2-20T"
  Group = -> [Cylinder021,Cylinder018,Cylinder023,Cylinder022,Cut001003,Cut001002,Chamfer018,Cylinder019,Fusion007003,Array003,Chamfer017,Cylinder020,Cut001004,Cut002001,Cylinder024,Chamfer002,Sketch038,Pocket014,Pocket015,Cut002010]
  License = CC BY 3.0
  LicenseURL = http://creativecommons.org/licenses/by/3.0/
  Origin = -> Origin017
FEATURE [Part::Feature] Part__Feature001  label="SHF009"
  shape: bbox 22.8 x 7.577 x 7.577 mm, 30 faces (baked)
FEATURE [Part::Feature] Part__Feature  label="SHF8"
  shape: bbox 42 x 24 x 10 mm, 87 faces (baked)
FEATURE [App::Part] SHF8  label="SHF8_001"
  Group = -> [Part__Feature,Part__Feature001]
  License = CC BY 3.0
  LicenseURL = http://creativecommons.org/licenses/by/3.0/
  Origin = -> Origin029
  Placement = pos=(18,-4,14.7) rot=(0.889126,-0.323616,0.323616;1.68804rad)
FEATURE [Part::Feature] CNC_shield
  Placement = pos=(-43.68,-35.7172,-8.545) rot=(0,0,1;0rad)
  shape: bbox 52.96 x 10.9 x 68.19 mm, 397 faces, 35 solids (baked)
FEATURE [Part::Feature] CNC_shield001
  Placement = pos=(-5.50511,-31.7172,43.759) rot=(0,0,1;0rad)
  shape: bbox 20.57 x 11.65 x 2.5 mm, 290 faces (baked)
FEATURE [Part::Feature] CNC_shield002
  Placement = pos=(-5.50511,-31.7172,31.069) rot=(0,0,1;0rad)
  shape: bbox 20.57 x 11.65 x 2.5 mm, 290 faces (baked)
FEATURE [Part::Feature] CNC_shield004
  Placement = pos=(-28.895,-31.7172,43.759) rot=(0,0,1;0rad)
  shape: bbox 20.57 x 11.65 x 2.5 mm, 290 faces (baked)
FEATURE [Part::Feature] CNC_shield005
  Placement = pos=(-28.895,-31.7172,31.069) rot=(0,0,1;0rad)
  shape: bbox 20.57 x 11.65 x 2.5 mm, 290 faces (baked)
FEATURE [Part::Feature] CNC_shield007
  Placement = pos=(-28.895,-31.7172,22.642) rot=(0,0,1;0rad)
  shape: bbox 20.57 x 11.65 x 2.5 mm, 290 faces (baked)
FEATURE [Part::Feature] CNC_shield008
  Placement = pos=(-28.895,-31.7172,9.952) rot=(0,0,1;0rad)
  shape: bbox 20.57 x 11.65 x 2.5 mm, 290 faces (baked)
FEATURE [Part::Feature] CNC_shield010
  Placement = pos=(-5.50511,-31.7172,22.642) rot=(0,0,1;0rad)
  shape: bbox 20.57 x 11.65 x 2.5 mm, 290 faces (baked)
FEATURE [Part::Feature] CNC_shield011
  Placement = pos=(-5.50511,-31.7172,9.952) rot=(0,0,1;0rad)
  shape: bbox 20.57 x 11.65 x 2.5 mm, 290 faces (baked)
FEATURE [Part::Feature] CNC_shield013
  Placement = pos=(2.27989,-31.7172,34.874) rot=(0,0,1;0rad)
  shape: bbox 5 x 11.75 x 2.54 mm, 46 faces (baked)
FEATURE [Part::Feature] CNC_shield014
  Placement = pos=(2.27989,-31.7172,37.414) rot=(0,0,1;0rad)
  shape: bbox 5 x 11.75 x 2.54 mm, 46 faces (baked)
FEATURE [Part::Feature] CNC_shield015
  Placement = pos=(2.27989,-31.7172,39.954) rot=(0,0,1;0rad)
  shape: bbox 5 x 11.75 x 2.54 mm, 46 faces (baked)
FEATURE [Part::Feature] CNC_shield016
  Placement = pos=(-21.11,-31.7172,34.874) rot=(0,0,1;0rad)
  shape: bbox 5 x 11.75 x 2.54 mm, 46 faces (baked)
FEATURE [Part::Feature] CNC_shield017
  Placement = pos=(-21.11,-31.7172,37.414) rot=(0,0,1;0rad)
  shape: bbox 5 x 11.75 x 2.54 mm, 46 faces (baked)
FEATURE [Part::Feature] CNC_shield018
  Placement = pos=(-21.11,-31.7172,39.954) rot=(0,0,1;0rad)
  shape: bbox 5 x 11.75 x 2.54 mm, 46 faces (baked)
FEATURE [Part::Feature] CNC_shield019
  Placement = pos=(-21.11,-31.7172,13.757) rot=(0,0,1;0rad)
  shape: bbox 5 x 11.75 x 2.54 mm, 46 faces (baked)
FEATURE [Part::Feature] CNC_shield020
  Placement = pos=(-21.11,-31.7172,16.297) rot=(0,0,1;0rad)
  shape: bbox 5 x 11.75 x 2.54 mm, 46 faces (baked)
FEATURE [Part::Feature] CNC_shield021
  Placement = pos=(-21.11,-31.7172,18.837) rot=(0,0,1;0rad)
  shape: bbox 5 x 11.75 x 2.54 mm, 46 faces (baked)
FEATURE [Part::Feature] CNC_shield022
  Placement = pos=(2.27989,-31.7172,13.757) rot=(0,0,1;0rad)
  shape: bbox 5 x 11.75 x 2.54 mm, 46 faces (baked)
FEATURE [Part::Feature] CNC_shield023
  Placement = pos=(2.27989,-31.7172,16.297) rot=(0,0,1;0rad)
  shape: bbox 5 x 11.75 x 2.54 mm, 46 faces (baked)
FEATURE [Part::Feature] CNC_shield024
  Placement = pos=(2.27989,-31.7172,18.837) rot=(0,0,1;0rad)
  shape: bbox 5 x 11.75 x 2.54 mm, 46 faces (baked)
FEATURE [Part::Feature] CNC_shield026
  Placement = pos=(-9.36011,-29.4272,6.457) rot=(-1,0,0;1.5708rad)
  shape: bbox 10.16 x 11.54 x 2.49 mm, 128 faces, 8 solids (baked)
FEATURE [Part::Feature] CNC_shield027
  Placement = pos=(-37.3801,-29.4272,-1.90485) rot=(-1,0,0;1.5708rad)
  shape: bbox 10.16 x 11.54 x 4.98 mm, 240 faces, 12 solids (baked)
FEATURE [Part::Feature] CNC_shield028
  Placement = pos=(-33.91,-29.4272,46.754) rot=(-1,0,0;1.5708rad)
  shape: bbox 15.24 x 11.54 x 4.98 mm, 360 faces, 18 solids (baked)
FEATURE [Part::Feature] CNC_shield029
  Placement = pos=(-27.2201,-29.4272,-3.06) rot=(-1,0,0;1.5708rad)
  shape: bbox 33.02 x 11.54 x 4.98 mm, 612 faces, 2 solids (baked)
FEATURE [Part::Feature] CNC_shield030
  Placement = pos=(-18.17,-29.4272,49.194) rot=(-1,0,0;1.5708rad)
  shape: bbox 10.16 x 11.54 x 9.96 mm, 464 faces, 20 solids (baked)
FEATURE [Part::Feature] CNC_shield031
  Placement = pos=(-32.66,-29.4272,27.574) rot=(-1,0,0;1.5708rad)
  shape: bbox 10.16 x 11.54 x 2.49 mm, 128 faces, 8 solids (baked)
FEATURE [Part::Feature] CNC_shield032
  Placement = pos=(-32.66,-29.4272,6.457) rot=(-1,0,0;1.5708rad)
  shape: bbox 10.16 x 11.54 x 2.49 mm, 128 faces, 8 solids (baked)
FEATURE [Part::Feature] CNC_shield033
  Placement = pos=(-9.36011,-29.4272,27.574) rot=(-1,0,0;1.5708rad)
  shape: bbox 10.16 x 11.54 x 2.49 mm, 128 faces, 8 solids (baked)
FEATURE [Part::Feature] CNC_shield034
  Placement = pos=(-4.02011,-31.7172,52.6449) rot=(0,1,0;1.5708rad)
  shape: bbox 7.606 x 13.5 x 11.16 mm, 176 faces, 7 solids (baked)
FEATURE [Part::Feature] CNC_shield035
  Placement = pos=(-39.38,-28.3172,53.6449) rot=(0.57735,0.57735,0.57735;4.18879rad)
  shape: bbox 6 x 4.4 x 10 mm, 48 faces (baked)
FEATURE [Part::Feature] CNC_shield039
  Placement = pos=(-21.15,-29.2172,40.024) rot=(-1,0,0;1.5708rad)
  shape: bbox 5.08 x 6.1 x 2.4 mm, 59 faces, 2 solids (baked)
FEATURE [Part::Feature] CNC_shield040
  Placement = pos=(-21.15,-29.2172,37.484) rot=(-1,0,0;1.5708rad)
  shape: bbox 5.08 x 6.1 x 2.4 mm, 59 faces, 2 solids (baked)
FEATURE [Part::Feature] CNC_shield041
  Placement = pos=(-21.15,-29.2172,34.944) rot=(-1,0,0;1.5708rad)
  shape: bbox 5.08 x 6.1 x 2.4 mm, 59 faces, 2 solids (baked)
FEATURE [Part::Feature] CNC_shield042
  Placement = pos=(2.23989,-29.2172,40.024) rot=(-1,0,0;1.5708rad)
  shape: bbox 5.08 x 6.1 x 2.4 mm, 59 faces, 2 solids (baked)
FEATURE [Part::Feature] CNC_shield043
  Placement = pos=(2.23989,-29.2172,37.484) rot=(-1,0,0;1.5708rad)
  shape: bbox 5.08 x 6.1 x 2.4 mm, 59 faces, 2 solids (baked)
FEATURE [Part::Feature] CNC_shield044
  Placement = pos=(2.23989,-29.2172,34.944) rot=(-1,0,0;1.5708rad)
  shape: bbox 5.08 x 6.1 x 2.4 mm, 59 faces, 2 solids (baked)
FEATURE [Part::Feature] CNC_shield045
  Placement = pos=(-21.15,-29.2172,18.907) rot=(-1,0,0;1.5708rad)
  shape: bbox 5.08 x 6.1 x 2.4 mm, 59 faces, 2 solids (baked)
FEATURE [Part::Feature] CNC_shield046
  Placement = pos=(-21.15,-29.2172,16.367) rot=(-1,0,0;1.5708rad)
  shape: bbox 5.08 x 6.1 x 2.4 mm, 59 faces, 2 solids (baked)
FEATURE [Part::Feature] CNC_shield047
  Placement = pos=(-21.15,-29.2172,13.827) rot=(-1,0,0;1.5708rad)
  shape: bbox 5.08 x 6.1 x 2.4 mm, 59 faces, 2 solids (baked)
FEATURE [Part::Feature] CNC_shield048
  Placement = pos=(2.23989,-29.2172,18.907) rot=(-1,0,0;1.5708rad)
  shape: bbox 5.08 x 6.1 x 2.4 mm, 59 faces, 2 solids (baked)
FEATURE [Part::Feature] CNC_shield049
  Placement = pos=(2.23989,-29.2172,16.367) rot=(-1,0,0;1.5708rad)
  shape: bbox 5.08 x 6.1 x 2.4 mm, 59 faces, 2 solids (baked)
FEATURE [Part::Feature] CNC_shield050
  Placement = pos=(2.23989,-29.2172,13.827) rot=(-1,0,0;1.5708rad)
  shape: bbox 5.08 x 6.1 x 2.4 mm, 59 faces, 2 solids (baked)
FEATURE [App::Part] Part029  label="CNC Shield"
  Group = -> [CNC_shield,CNC_shield001,CNC_shield002,CNC_shield004,CNC_shield005,CNC_shield007,CNC_shield008,CNC_shield010,CNC_shield011,CNC_shield013,CNC_shield014,CNC_shield015,CNC_shield016,CNC_shield017,CNC_shield018,CNC_shield019,CNC_shield020,CNC_shield021,CNC_shield022,CNC_shield023,CNC_shield024,CNC_shield026,CNC_shield027,CNC_shield028,CNC_shield029,CNC_shield030,CNC_shield031,CNC_shield032,+15 more]
  License = CC BY 3.0
  LicenseURL = http://creativecommons.org/licenses/by/3.0/
  Origin = -> Origin030
  Placement = pos=(15,60,67) rot=(0,0.707107,0.707107;-3.14159rad)
FEATURE [App::DocumentObjectGroup] Group002  label="Electronics"
  Group = -> [Part003,Part005,Part001,Part029]
FEATURE [Part::Cylinder] Cylinder027
  Angle = 360
  AttacherType = Attacher::AttachEngine3D
  Height = 6
  Placement = pos=(-6.75,0,7) rot=(1,0,0;1.5708rad)
  Radius = 2.75
FEATURE [Part::Cylinder] Cylinder028
  Angle = 360
  AttacherType = Attacher::AttachEngine3D
  Height = 14
  Placement = pos=(9,14,0) rot=(0,0,1;0rad)
  Radius = 4
FEATURE [Part::Box] Box008  label="Cube003"
  AttacherType = Attacher::AttachEngine3D
  Height = 14
  Length = 42
  Placement = pos=(-12,-6,0) rot=(0,0,1;0rad)
  Width = 6
FEATURE [Part::Feature] Chamfer001001  label="Chamfer028"
  shape: bbox 42 x 33 x 14 mm, 30 faces (baked)
FEATURE [Part::Box] Box009  label="Cube004"
  AttacherType = Attacher::AttachEngine3D
  Height = 14
  Length = 1
  Placement = pos=(8.5,17,0) rot=(0,0,1;0rad)
  Width = 10
FEATURE [Part::Cylinder] Cylinder029
  Angle = 360
  AttacherType = Attacher::AttachEngine3D
  Height = 6
  Placement = pos=(24.75,0,7) rot=(1,0,0;1.5708rad)
  Radius = 2.75
FEATURE [Part::Box] Box010  label="Cube005"
  AttacherType = Attacher::AttachEngine3D
  Height = 14
  Length = 18
  Width = 27
FEATURE [Part::MultiFuse] Fusion007004
  Shapes = -> [Box010,Box008]
FEATURE [Part::Cut] Cut002015
  Base = -> Fusion007004
  Tool = -> Cylinder027
FEATURE [Part::Cut] Cut002011
  Base = -> Cut002015
  Tool = -> Cylinder029
FEATURE [Part::Cylinder] Cylinder030
  Angle = 360
  AttacherType = Attacher::AttachEngine3D
  Height = 18
  Placement = pos=(0,21.75,7) rot=(0,1,0;1.5708rad)
  Radius = 2
FEATURE [Part::Cut] Cut002016
  Base = -> Cut002011
  Tool = -> Box009
FEATURE [Part::Cut] Cut002012
  Base = -> Cut002016
  Tool = -> Cylinder028
FEATURE [Part::Cut] Cut002013
  Base = -> Cut002012
  Tool = -> Cylinder030
FEATURE [Sketcher::SketchObject] Sketch056
  MapMode = 5
  Placement = pos=(0,0,0) rot=(0.57735,0.57735,0.57735;2.0944rad)
  sketch-geometry (9):
    g0: LineSegment StartX=1.999 StartY=0 StartZ=0 EndX=3.5 EndY=0 EndZ=0
    g1: LineSegment StartX=3.5 StartY=0 StartZ=0 EndX=3.5 EndY=3.97229 EndZ=0
    g2: LineSegment StartX=3.47229 StartY=4 StartZ=0 EndX=0 EndY=4 EndZ=0
    g3: LineSegment StartX=1.999 StartY=0 StartZ=0 EndX=2 EndY=-0.2 EndZ=0
    g4: LineSegment StartX=2 StartY=-0.2 StartZ=0 EndX=2 EndY=-13.3 EndZ=0
    g5: LineSegment StartX=2 StartY=-13.3 StartZ=0 EndX=1.3 EndY=-14 EndZ=0
    g6: LineSegment StartX=1.3 StartY=-14 StartZ=0 EndX=0 EndY=-14 EndZ=0
    g7: LineSegment StartX=0 StartY=-14 StartZ=0 EndX=0 EndY=4 EndZ=0
    g8: ArcOfCircle CenterX=3.47229 CenterY=3.97229 CenterZ=0 NormalX=0 NormalY=0 NormalZ=1 AngleXU=0 Radius=0.02771 StartAngle=0 EndAngle=1.5708
  constraints (26):
    c: PointOnObject(g0,g-1)
    c: Horizontal(g0)
    c: Coincident(g1,g0)
    c: Vertical(g1)
    c: Horizontal(g2)
    c: Coincident(g3,g0)
    c: Coincident(g4,g3)
    c: Vertical(g4)
    c: Coincident(g5,g4)
    c: Coincident(g6,g5)
    c: Horizontal(g6)
    c: Coincident(g7,g6)
    c: Coincident(g7,g2)
    c: Vertical(g7)
    c: Tangent(g1,g8) = -1.5708
    c: Tangent(g2,g8) = -1.5708
    c: DistanceY(g5) = -0.7
    c: DistanceX(g5) = -0.7
    c: DistanceY(g5,g3) = 13.8
    c: DistanceY(g5,g0) = 14
    c: DistanceY(g0,g2) = 4
    c: DistanceX(g2,g0) = 3.5
    c: DistanceX(g6,g4) = 2
    c: DistanceX(g3,g0) = -0.001
    c: PointOnObject(g-1,g7)
    c: Radius(g8) = 0.02771
FEATURE [Part::Revolution] Revolve
  Angle = 360
  Axis = (0,0,1)
  Base = (0,0,0)
  Solid = true
  Source = -> Sketch056
  Symmetric = false
FEATURE [Sketcher::SketchObject] Sketch055
  MapMode = 5
  Placement = pos=(0,0,4) rot=(0,0,1;0rad)
  Support = -> [Revolve]
  sketch-geometry (7):
    g0: LineSegment StartX=1.76669 StartY=0 StartZ=0 EndX=0.883346 EndY=1.53 EndZ=0
    g1: LineSegment StartX=0.883346 StartY=1.53 StartZ=0 EndX=-0.883346 EndY=1.53 EndZ=0
    g2: LineSegment StartX=-0.883346 StartY=1.53 StartZ=0 EndX=-1.76669 EndY=0 EndZ=0
    g3: LineSegment StartX=-1.76669 StartY=0 StartZ=0 EndX=-0.883346 EndY=-1.53 EndZ=0
    g4: LineSegment StartX=-0.883346 StartY=-1.53 StartZ=0 EndX=0.883346 EndY=-1.53 EndZ=0
    g5: LineSegment StartX=0.883346 StartY=-1.53 StartZ=0 EndX=1.76669 EndY=0 EndZ=0
    g6: Circle [constr] CenterX=0 CenterY=0 CenterZ=0 NormalX=0 NormalY=0 NormalZ=1 AngleXU=0 Radius=1.76669
  constraints (16):
    c: Coincident(g0,g1)
    c: Coincident(g1,g2)
    c: Coincident(g2,g3)
    c: Coincident(g3,g4)
    c: Coincident(g4,g5)
    c: Coincident(g5,g0)
    c: Equal(g0, g1-g5) x5
    c: PointOnObject(g0,g6)
    c: PointOnObject(g1,g6)
    c: PointOnObject(g2,g6)
    c: PointOnObject(g3,g6)
    c: PointOnObject(g4,g6)
    c: PointOnObject(g5,g6)
    c: Horizontal(g4)
    c: DistanceY(g4,g0) = 3.06
    c: Coincident(g6,g-1)
FEATURE [PartDesign::Pocket] Pocket001002  label="Screw M4x14 ISO4762 8,8 A2K"
  Length = 3.06
  Length2 = 100
  Profile = -> Sketch055
  Type = 0
FEATURE [App::Part] Part030  label="Screw"
  Group = -> [Sketch056,Sketch055,Revolve,Pocket001002]
  License = CC BY 3.0
  LicenseURL = http://creativecommons.org/licenses/by/3.0/
  Origin = -> Origin031
  Placement = pos=(4,21.75,7) rot=(0,-1,0;1.5708rad)
FEATURE [Part::Cylinder] Cylinder031
  Angle = 360
  AttacherType = Attacher::AttachEngine3D
  Height = 4.75
  Placement = pos=(0,21.75,7) rot=(0,1,0;1.5708rad)
  Radius = 3.5
FEATURE [Part::Cut] Cut002014
  Base = -> Cut002013
  Tool = -> Cylinder031
FEATURE [Part::Chamfer] Chamfer001002
  Base = -> Cut002014
  Edges = 5 edges r=0.5: [Edge24,Edge45,Edge50,Edge53,Edge54]
FEATURE [Part::Chamfer] Chamfer027
  Base = -> Chamfer001002
  Edges = 5 edges r=0.2: [Edge14,Edge15,Edge22,Edge23,Edge50]
FEATURE [App::Part] Part031  label="SK8-001"
  Group = -> [Part030,Chamfer001002,Fusion007004,Box010,Cut002015,Cut002011,Box008,Cylinder028,Cylinder029,Box009,Cylinder027,Cylinder030,Cylinder031,Cut002016,Cut002012,Cut002013,Cut002014,Chamfer027,Chamfer001001]
  License = CC BY 3.0
  LicenseURL = http://creativecommons.org/licenses/by/3.0/
  Origin = -> Origin032
  Placement = pos=(90,14,12) rot=(0.57735,0.57735,0.57735;2.0944rad)
FEATURE [Part::Cylinder] Cylinder032
  Angle = 360
  AttacherType = Attacher::AttachEngine3D
  Height = 6
  Placement = pos=(-6.75,0,7) rot=(1,0,0;1.5708rad)
  Radius = 2.75
FEATURE [Part::Cylinder] Cylinder033
  Angle = 360
  AttacherType = Attacher::AttachEngine3D
  Height = 14
  Placement = pos=(9,14,0) rot=(0,0,1;0rad)
  Radius = 4
FEATURE [Part::Box] Box011  label="Cube006"
  AttacherType = Attacher::AttachEngine3D
  Height = 14
  Length = 42
  Placement = pos=(-12,-6,0) rot=(0,0,1;0rad)
  Width = 6
FEATURE [Part::Feature] Chamfer001004
  shape: bbox 42 x 33 x 14 mm, 30 faces (baked)
FEATURE [Part::Box] Box012  label="Cube007"
  AttacherType = Attacher::AttachEngine3D
  Height = 14
  Length = 1
  Placement = pos=(8.5,17,0) rot=(0,0,1;0rad)
  Width = 10
FEATURE [Part::Box] Box013  label="Cube008"
  AttacherType = Attacher::AttachEngine3D
  Height = 14
  Length = 18
  Width = 27
FEATURE [Part::MultiFuse] Fusion007005
  Shapes = -> [Box013,Box011]
FEATURE [Part::Cylinder] Cylinder034
  Angle = 360
  AttacherType = Attacher::AttachEngine3D
  Height = 6
  Placement = pos=(24.75,0,7) rot=(1,0,0;1.5708rad)
  Radius = 2.75
FEATURE [Part::Cut] Cut002021
  Base = -> Fusion007005
  Tool = -> Cylinder032
FEATURE [Part::Cut] Cut002017
  Base = -> Cut002021
  Tool = -> Cylinder034
FEATURE [Part::Cylinder] Cylinder035
  Angle = 360
  AttacherType = Attacher::AttachEngine3D
  Height = 18
  Placement = pos=(0,21.75,7) rot=(0,1,0;1.5708rad)
  Radius = 2
FEATURE [Part::Cut] Cut002022
  Base = -> Cut002017
  Tool = -> Box012
FEATURE [Part::Cut] Cut002018
  Base = -> Cut002022
  Tool = -> Cylinder033
FEATURE [Part::Cut] Cut002019
  Base = -> Cut002018
  Tool = -> Cylinder035
FEATURE [Sketcher::SketchObject] Sketch058
  MapMode = 5
  Placement = pos=(0,0,0) rot=(0.57735,0.57735,0.57735;2.0944rad)
  sketch-geometry (9):
    g0: LineSegment StartX=1.999 StartY=0 StartZ=0 EndX=3.5 EndY=0 EndZ=0
    g1: LineSegment StartX=3.5 StartY=0 StartZ=0 EndX=3.5 EndY=3.97229 EndZ=0
    g2: LineSegment StartX=3.47229 StartY=4 StartZ=0 EndX=0 EndY=4 EndZ=0
    g3: LineSegment StartX=1.999 StartY=0 StartZ=0 EndX=2 EndY=-0.2 EndZ=0
    g4: LineSegment StartX=2 StartY=-0.2 StartZ=0 EndX=2 EndY=-13.3 EndZ=0
    g5: LineSegment StartX=2 StartY=-13.3 StartZ=0 EndX=1.3 EndY=-14 EndZ=0
    g6: LineSegment StartX=1.3 StartY=-14 StartZ=0 EndX=0 EndY=-14 EndZ=0
    g7: LineSegment StartX=0 StartY=-14 StartZ=0 EndX=0 EndY=4 EndZ=0
    g8: ArcOfCircle CenterX=3.47229 CenterY=3.97229 CenterZ=0 NormalX=0 NormalY=0 NormalZ=1 AngleXU=0 Radius=0.02771 StartAngle=0 EndAngle=1.5708
  constraints (26):
    c: PointOnObject(g0,g-1)
    c: Horizontal(g0)
    c: Coincident(g1,g0)
    c: Vertical(g1)
    c: Horizontal(g2)
    c: Coincident(g3,g0)
    c: Coincident(g4,g3)
    c: Vertical(g4)
    c: Coincident(g5,g4)
    c: Coincident(g6,g5)
    c: Horizontal(g6)
    c: Coincident(g7,g6)
    c: Coincident(g7,g2)
    c: Vertical(g7)
    c: Tangent(g1,g8) = -1.5708
    c: Tangent(g2,g8) = -1.5708
    c: DistanceY(g5) = -0.7
    c: DistanceX(g5) = -0.7
    c: DistanceY(g5,g3) = 13.8
    c: DistanceY(g5,g0) = 14
    c: DistanceY(g0,g2) = 4
    c: DistanceX(g2,g0) = 3.5
    c: DistanceX(g6,g4) = 2
    c: DistanceX(g3,g0) = -0.001
    c: PointOnObject(g-1,g7)
    c: Radius(g8) = 0.02771
FEATURE [Part::Revolution] Revolve001
  Angle = 360
  Axis = (0,0,1)
  Base = (0,0,0)
  Solid = true
  Source = -> Sketch058
  Symmetric = false
FEATURE [Sketcher::SketchObject] Sketch057
  MapMode = 5
  Placement = pos=(0,0,4) rot=(0,0,1;0rad)
  Support = -> [Revolve001]
  sketch-geometry (7):
    g0: LineSegment StartX=1.76669 StartY=0 StartZ=0 EndX=0.883346 EndY=1.53 EndZ=0
    g1: LineSegment StartX=0.883346 StartY=1.53 StartZ=0 EndX=-0.883346 EndY=1.53 EndZ=0
    g2: LineSegment StartX=-0.883346 StartY=1.53 StartZ=0 EndX=-1.76669 EndY=0 EndZ=0
    g3: LineSegment StartX=-1.76669 StartY=0 StartZ=0 EndX=-0.883346 EndY=-1.53 EndZ=0
    g4: LineSegment StartX=-0.883346 StartY=-1.53 StartZ=0 EndX=0.883346 EndY=-1.53 EndZ=0
    g5: LineSegment StartX=0.883346 StartY=-1.53 StartZ=0 EndX=1.76669 EndY=0 EndZ=0
    g6: Circle [constr] CenterX=0 CenterY=0 CenterZ=0 NormalX=0 NormalY=0 NormalZ=1 AngleXU=0 Radius=1.76669
  constraints (16):
    c: Coincident(g0,g1)
    c: Coincident(g1,g2)
    c: Coincident(g2,g3)
    c: Coincident(g3,g4)
    c: Coincident(g4,g5)
    c: Coincident(g5,g0)
    c: Equal(g0, g1-g5) x5
    c: PointOnObject(g0,g6)
    c: PointOnObject(g1,g6)
    c: PointOnObject(g2,g6)
    c: PointOnObject(g3,g6)
    c: PointOnObject(g4,g6)
    c: PointOnObject(g5,g6)
    c: Horizontal(g4)
    c: DistanceY(g4,g0) = 3.06
    c: Coincident(g6,g-1)
FEATURE [PartDesign::Pocket] Pocket001003  label="Screw M4x14 ISO4762 8,8 A2K001"
  Length = 3.06
  Length2 = 100
  Profile = -> Sketch057
  Type = 0
FEATURE [App::Part] Part032  label="Screw001"
  Group = -> [Sketch058,Sketch057,Revolve001,Pocket001003]
  License = CC BY 3.0
  LicenseURL = http://creativecommons.org/licenses/by/3.0/
  Origin = -> Origin033
  Placement = pos=(4,21.75,7) rot=(0,-1,0;1.5708rad)
FEATURE [Part::Cylinder] Cylinder036
  Angle = 360
  AttacherType = Attacher::AttachEngine3D
  Height = 4.75
  Placement = pos=(0,21.75,7) rot=(0,1,0;1.5708rad)
  Radius = 3.5
FEATURE [Part::Cut] Cut002020
  Base = -> Cut002019
  Tool = -> Cylinder036
FEATURE [Part::Chamfer] Chamfer001005
  Base = -> Cut002020
  Edges = 5 edges r=0.5: [Edge24,Edge45,Edge50,Edge53,Edge54]
FEATURE [Part::Chamfer] Chamfer001003
  Base = -> Chamfer001005
  Edges = 5 edges r=0.2: [Edge14,Edge15,Edge22,Edge23,Edge50]
FEATURE [App::Part] Part033  label="SK8-002"
  Group = -> [Part032,Chamfer001005,Fusion007005,Box013,Cut002021,Cut002017,Box011,Cylinder033,Cylinder034,Box012,Cylinder032,Cylinder035,Cylinder036,Cut002022,Cut002018,Cut002019,Cut002020,Chamfer001003,Chamfer001004]
  License = CC BY 3.0
  LicenseURL = http://creativecommons.org/licenses/by/3.0/
  Origin = -> Origin034
  Placement = pos=(104,106,12) rot=(-0.57735,0.57735,0.57735;-2.0944rad)
FEATURE [Part::Cylinder] Cylinder037
  Angle = 360
  AttacherType = Attacher::AttachEngine3D
  Height = 6
  Placement = pos=(-6.75,0,7) rot=(1,0,0;1.5708rad)
  Radius = 2.75
FEATURE [Part::Cylinder] Cylinder038
  Angle = 360
  AttacherType = Attacher::AttachEngine3D
  Height = 14
  Placement = pos=(9,14,0) rot=(0,0,1;0rad)
  Radius = 4
FEATURE [Part::Box] Box014  label="Cube009"
  AttacherType = Attacher::AttachEngine3D
  Height = 14
  Length = 42
  Placement = pos=(-12,-6,0) rot=(0,0,1;0rad)
  Width = 6
FEATURE [Part::Feature] Chamfer001007
  shape: bbox 42 x 33 x 14 mm, 30 faces (baked)
FEATURE [Part::Box] Box015  label="Cube010"
  AttacherType = Attacher::AttachEngine3D
  Height = 14
  Length = 1
  Placement = pos=(8.5,17,0) rot=(0,0,1;0rad)
  Width = 10
FEATURE [Part::Box] Box016  label="Cube011"
  AttacherType = Attacher::AttachEngine3D
  Height = 14
  Length = 18
  Width = 27
FEATURE [Part::MultiFuse] Fusion007006
  Shapes = -> [Box016,Box014]
FEATURE [Part::Cylinder] Cylinder039
  Angle = 360
  AttacherType = Attacher::AttachEngine3D
  Height = 6
  Placement = pos=(24.75,0,7) rot=(1,0,0;1.5708rad)
  Radius = 2.75
FEATURE [Part::Cut] Cut002023
  Tool = -> Cylinder039
FEATURE [Part::Cylinder] Cylinder040
  Angle = 360
  AttacherType = Attacher::AttachEngine3D
  Height = 18
  Placement = pos=(0,21.75,7) rot=(0,1,0;1.5708rad)
  Radius = 2
FEATURE [Part::Cut] Cut002028
  Base = -> Cut002023
  Tool = -> Box015
FEATURE [Part::Cut] Cut002024
  Base = -> Cut002028
  Tool = -> Cylinder038
FEATURE [Part::Cut] Cut002025
  Base = -> Cut002024
  Tool = -> Cylinder040
FEATURE [Sketcher::SketchObject] Sketch060
  MapMode = 5
  Placement = pos=(0,0,0) rot=(0.57735,0.57735,0.57735;2.0944rad)
  sketch-geometry (9):
    g0: LineSegment StartX=1.999 StartY=0 StartZ=0 EndX=3.5 EndY=0 EndZ=0
    g1: LineSegment StartX=3.5 StartY=0 StartZ=0 EndX=3.5 EndY=3.97229 EndZ=0
    g2: LineSegment StartX=3.47229 StartY=4 StartZ=0 EndX=0 EndY=4 EndZ=0
    g3: LineSegment StartX=1.999 StartY=0 StartZ=0 EndX=2 EndY=-0.2 EndZ=0
    g4: LineSegment StartX=2 StartY=-0.2 StartZ=0 EndX=2 EndY=-13.3 EndZ=0
    g5: LineSegment StartX=2 StartY=-13.3 StartZ=0 EndX=1.3 EndY=-14 EndZ=0
    g6: LineSegment StartX=1.3 StartY=-14 StartZ=0 EndX=0 EndY=-14 EndZ=0
    g7: LineSegment StartX=0 StartY=-14 StartZ=0 EndX=0 EndY=4 EndZ=0
    g8: ArcOfCircle CenterX=3.47229 CenterY=3.97229 CenterZ=0 NormalX=0 NormalY=0 NormalZ=1 AngleXU=0 Radius=0.02771 StartAngle=0 EndAngle=1.5708
  constraints (26):
    c: PointOnObject(g0,g-1)
    c: Horizontal(g0)
    c: Coincident(g1,g0)
    c: Vertical(g1)
    c: Horizontal(g2)
    c: Coincident(g3,g0)
    c: Coincident(g4,g3)
    c: Vertical(g4)
    c: Coincident(g5,g4)
    c: Coincident(g6,g5)
    c: Horizontal(g6)
    c: Coincident(g7,g6)
    c: Coincident(g7,g2)
    c: Vertical(g7)
    c: Tangent(g1,g8) = -1.5708
    c: Tangent(g2,g8) = -1.5708
    c: DistanceY(g5) = -0.7
    c: DistanceX(g5) = -0.7
    c: DistanceY(g5,g3) = 13.8
    c: DistanceY(g5,g0) = 14
    c: DistanceY(g0,g2) = 4
    c: DistanceX(g2,g0) = 3.5
    c: DistanceX(g6,g4) = 2
    c: DistanceX(g3,g0) = -0.001
    c: PointOnObject(g-1,g7)
    c: Radius(g8) = 0.02771
FEATURE [Part::Revolution] Revolve002
  Angle = 360
  Axis = (0,0,1)
  Base = (0,0,0)
  Solid = true
  Source = -> Sketch060
  Symmetric = false
FEATURE [Sketcher::SketchObject] Sketch059
  MapMode = 5
  Placement = pos=(0,0,4) rot=(0,0,1;0rad)
  Support = -> [Revolve002]
  sketch-geometry (7):
    g0: LineSegment StartX=1.76669 StartY=0 StartZ=0 EndX=0.883346 EndY=1.53 EndZ=0
    g1: LineSegment StartX=0.883346 StartY=1.53 StartZ=0 EndX=-0.883346 EndY=1.53 EndZ=0
    g2: LineSegment StartX=-0.883346 StartY=1.53 StartZ=0 EndX=-1.76669 EndY=0 EndZ=0
    g3: LineSegment StartX=-1.76669 StartY=0 StartZ=0 EndX=-0.883346 EndY=-1.53 EndZ=0
    g4: LineSegment StartX=-0.883346 StartY=-1.53 StartZ=0 EndX=0.883346 EndY=-1.53 EndZ=0
    g5: LineSegment StartX=0.883346 StartY=-1.53 StartZ=0 EndX=1.76669 EndY=0 EndZ=0
    g6: Circle [constr] CenterX=0 CenterY=0 CenterZ=0 NormalX=0 NormalY=0 NormalZ=1 AngleXU=0 Radius=1.76669
  constraints (16):
    c: Coincident(g0,g1)
    c: Coincident(g1,g2)
    c: Coincident(g2,g3)
    c: Coincident(g3,g4)
    c: Coincident(g4,g5)
    c: Coincident(g5,g0)
    c: Equal(g0, g1-g5) x5
    c: PointOnObject(g0,g6)
    c: PointOnObject(g1,g6)
    c: PointOnObject(g2,g6)
    c: PointOnObject(g3,g6)
    c: PointOnObject(g4,g6)
    c: PointOnObject(g5,g6)
    c: Horizontal(g4)
    c: DistanceY(g4,g0) = 3.06
    c: Coincident(g6,g-1)
FEATURE [PartDesign::Pocket] Pocket001004  label="Screw M4x14 ISO4762 8,8 A2K002"
  Length = 3.06
  Length2 = 100
  Profile = -> Sketch059
  Type = 0
FEATURE [App::Part] Part034  label="Screw002"
  Group = -> [Sketch060,Sketch059,Revolve002,Pocket001004]
  License = CC BY 3.0
  LicenseURL = http://creativecommons.org/licenses/by/3.0/
  Origin = -> Origin035
  Placement = pos=(4,21.75,7) rot=(0,-1,0;1.5708rad)
FEATURE [Part::Cylinder] Cylinder041
  Angle = 360
  AttacherType = Attacher::AttachEngine3D
  Height = 4.75
  Placement = pos=(0,21.75,7) rot=(0,1,0;1.5708rad)
  Radius = 3.5
FEATURE [Part::Cut] Cut002026
  Base = -> Cut002025
  Tool = -> Cylinder041
FEATURE [Part::Chamfer] Chamfer001008
  Base = -> Cut002026
  Edges = 5 edges r=0.5: [Edge24,Edge45,Edge50,Edge53,Edge54]
FEATURE [Part::Chamfer] Chamfer001006
  Base = -> Chamfer001008
  Edges = 5 edges r=0.2: [Edge14,Edge15,Edge22,Edge23,Edge50]
FEATURE [App::Part] Part035  label="SK8-003"
  Group = -> [Part034,Chamfer001008,Fusion007006,Box016,Cut002023,Box014,Cylinder038,Cylinder039,Box015,Cylinder037,Cylinder040,Cylinder041,Cut002028,Cut002024,Cut002025,Cut002026,Chamfer001006,Chamfer001007]
  License = CC BY 3.0
  LicenseURL = http://creativecommons.org/licenses/by/3.0/
  Origin = -> Origin036
  Placement = pos=(590,106,12) rot=(-0.57735,0.57735,0.57735;-2.0944rad)
FEATURE [Part::Cylinder] Cylinder042
  Angle = 360
  AttacherType = Attacher::AttachEngine3D
  Height = 6
  Placement = pos=(24.75,0,7) rot=(1,0,0;1.5708rad)
  Radius = 2.75
FEATURE [Part::Cylinder] Cylinder043
  Angle = 360
  AttacherType = Attacher::AttachEngine3D
  Height = 18
  Placement = pos=(0,21.75,7) rot=(0,1,0;1.5708rad)
  Radius = 2
FEATURE [Part::Cylinder] Cylinder044
  Angle = 360
  AttacherType = Attacher::AttachEngine3D
  Height = 4.75
  Placement = pos=(0,21.75,7) rot=(0,1,0;1.5708rad)
  Radius = 3.5
FEATURE [Part::Box] Box017  label="Cube012"
  AttacherType = Attacher::AttachEngine3D
  Height = 14
  Length = 42
  Placement = pos=(-12,-6,0) rot=(0,0,1;0rad)
  Width = 6
FEATURE [Part::Box] Box018  label="Cube013"
  AttacherType = Attacher::AttachEngine3D
  Height = 14
  Length = 1
  Placement = pos=(8.5,17,0) rot=(0,0,1;0rad)
  Width = 10
FEATURE [Sketcher::SketchObject] Sketch062
  MapMode = 5
  Placement = pos=(0,0,0) rot=(0.57735,0.57735,0.57735;2.0944rad)
  sketch-geometry (9):
    g0: LineSegment StartX=1.999 StartY=0 StartZ=0 EndX=3.5 EndY=0 EndZ=0
    g1: LineSegment StartX=3.5 StartY=0 StartZ=0 EndX=3.5 EndY=3.97229 EndZ=0
    g2: LineSegment StartX=3.47229 StartY=4 StartZ=0 EndX=0 EndY=4 EndZ=0
    g3: LineSegment StartX=1.999 StartY=0 StartZ=0 EndX=2 EndY=-0.2 EndZ=0
    g4: LineSegment StartX=2 StartY=-0.2 StartZ=0 EndX=2 EndY=-13.3 EndZ=0
    g5: LineSegment StartX=2 StartY=-13.3 StartZ=0 EndX=1.3 EndY=-14 EndZ=0
    g6: LineSegment StartX=1.3 StartY=-14 StartZ=0 EndX=0 EndY=-14 EndZ=0
    g7: LineSegment StartX=0 StartY=-14 StartZ=0 EndX=0 EndY=4 EndZ=0
    g8: ArcOfCircle CenterX=3.47229 CenterY=3.97229 CenterZ=0 NormalX=0 NormalY=0 NormalZ=1 AngleXU=0 Radius=0.02771 StartAngle=0 EndAngle=1.5708
  constraints (26):
    c: PointOnObject(g0,g-1)
    c: Horizontal(g0)
    c: Coincident(g1,g0)
    c: Vertical(g1)
    c: Horizontal(g2)
    c: Coincident(g3,g0)
    c: Coincident(g4,g3)
    c: Vertical(g4)
    c: Coincident(g5,g4)
    c: Coincident(g6,g5)
    c: Horizontal(g6)
    c: Coincident(g7,g6)
    c: Coincident(g7,g2)
    c: Vertical(g7)
    c: Tangent(g1,g8) = -1.5708
    c: Tangent(g2,g8) = -1.5708
    c: DistanceY(g5) = -0.7
    c: DistanceX(g5) = -0.7
    c: DistanceY(g5,g3) = 13.8
    c: DistanceY(g5,g0) = 14
    c: DistanceY(g0,g2) = 4
    c: DistanceX(g2,g0) = 3.5
    c: DistanceX(g6,g4) = 2
    c: DistanceX(g3,g0) = -0.001
    c: PointOnObject(g-1,g7)
    c: Radius(g8) = 0.02771
FEATURE [Part::Feature] Chamfer001010
  shape: bbox 42 x 33 x 14 mm, 30 faces (baked)
FEATURE [Part::Cylinder] Cylinder045
  Angle = 360
  AttacherType = Attacher::AttachEngine3D
  Height = 6
  Placement = pos=(-6.75,0,7) rot=(1,0,0;1.5708rad)
  Radius = 2.75
FEATURE [Part::Cylinder] Cylinder046
  Angle = 360
  AttacherType = Attacher::AttachEngine3D
  Height = 14
  Placement = pos=(9,14,0) rot=(0,0,1;0rad)
  Radius = 4
FEATURE [Part::Revolution] Revolve003
  Angle = 360
  Axis = (0,0,1)
  Base = (0,0,0)
  Solid = true
  Source = -> Sketch062
  Symmetric = false
FEATURE [Sketcher::SketchObject] Sketch061
  MapMode = 5
  Placement = pos=(0,0,4) rot=(0,0,1;0rad)
  Support = -> [Revolve003]
  sketch-geometry (7):
    g0: LineSegment StartX=1.76669 StartY=0 StartZ=0 EndX=0.883346 EndY=1.53 EndZ=0
    g1: LineSegment StartX=0.883346 StartY=1.53 StartZ=0 EndX=-0.883346 EndY=1.53 EndZ=0
    g2: LineSegment StartX=-0.883346 StartY=1.53 StartZ=0 EndX=-1.76669 EndY=0 EndZ=0
    g3: LineSegment StartX=-1.76669 StartY=0 StartZ=0 EndX=-0.883346 EndY=-1.53 EndZ=0
    g4: LineSegment StartX=-0.883346 StartY=-1.53 StartZ=0 EndX=0.883346 EndY=-1.53 EndZ=0
    g5: LineSegment StartX=0.883346 StartY=-1.53 StartZ=0 EndX=1.76669 EndY=0 EndZ=0
    g6: Circle [constr] CenterX=0 CenterY=0 CenterZ=0 NormalX=0 NormalY=0 NormalZ=1 AngleXU=0 Radius=1.76669
  constraints (16):
    c: Coincident(g0,g1)
    c: Coincident(g1,g2)
    c: Coincident(g2,g3)
    c: Coincident(g3,g4)
    c: Coincident(g4,g5)
    c: Coincident(g5,g0)
    c: Equal(g0, g1-g5) x5
    c: PointOnObject(g0,g6)
    c: PointOnObject(g1,g6)
    c: PointOnObject(g2,g6)
    c: PointOnObject(g3,g6)
    c: PointOnObject(g4,g6)
    c: PointOnObject(g5,g6)
    c: Horizontal(g4)
    c: DistanceY(g4,g0) = 3.06
    c: Coincident(g6,g-1)
FEATURE [PartDesign::Pocket] Pocket001005  label="Screw M4x14 ISO4762 8,8 A2K003"
  Length = 3.06
  Length2 = 100
  Profile = -> Sketch061
  Type = 0
FEATURE [App::Part] Part036  label="Screw003"
  Group = -> [Sketch062,Sketch061,Revolve003,Pocket001005]
  License = CC BY 3.0
  LicenseURL = http://creativecommons.org/licenses/by/3.0/
  Origin = -> Origin037
  Placement = pos=(4,21.75,7) rot=(0,-1,0;1.5708rad)
FEATURE [Part::Box] Box019  label="Cube014"
  AttacherType = Attacher::AttachEngine3D
  Height = 14
  Length = 18
  Width = 27
FEATURE [Part::MultiFuse] Fusion007007
  Shapes = -> [Box019,Box017]
FEATURE [Part::Cut] Cut002033
  Base = -> Fusion007007
  Tool = -> Cylinder045
FEATURE [Part::Cut] Cut002031
  Base = -> Cut002033
  Tool = -> Cylinder042
FEATURE [Part::Cut] Cut002030
  Base = -> Cut002031
  Tool = -> Box018
FEATURE [Part::Cut] Cut002034
  Base = -> Cut002030
  Tool = -> Cylinder046
FEATURE [Part::Cut] Cut002032
  Base = -> Cut002034
  Tool = -> Cylinder043
FEATURE [Part::Cut] Cut002029
  Base = -> Cut002032
  Tool = -> Cylinder044
FEATURE [Part::Chamfer] Chamfer001009
  Base = -> Cut002029
  Edges = 5 edges r=0.5: [Edge24,Edge45,Edge50,Edge53,Edge54]
FEATURE [Part::Chamfer] Chamfer001011
  Base = -> Chamfer001009
  Edges = 5 edges r=0.2: [Edge14,Edge15,Edge22,Edge23,Edge50]
FEATURE [App::Part] Part037  label="SK8-004"
  Group = -> [Part036,Chamfer001009,Fusion007007,Box019,Cut002033,Cut002031,Box017,Cylinder046,Cylinder042,Box018,Cylinder045,Cylinder043,Cylinder044,Cut002030,Cut002034,Cut002032,Cut002029,Chamfer001011,Chamfer001010]
  License = CC BY 3.0
  LicenseURL = http://creativecommons.org/licenses/by/3.0/
  Origin = -> Origin038
  Placement = pos=(576,14,12) rot=(0.57735,0.57735,0.57735;2.0944rad)
FEATURE [Part::Box] Box020  label="Cube015"
  AttacherType = Attacher::AttachEngine3D
  Height = 5.75
  Length = 66
  Placement = pos=(575,0,0.25) rot=(0,0,1;0rad)
  Width = 120
FEATURE [Sketcher::SketchObject] Sketch063
  MapMode = 5
  Placement = pos=(0,0,0) rot=(0.57735,0.57735,0.57735;2.0944rad)
  sketch-geometry (9):
    g0: LineSegment StartX=2.499 StartY=0 StartZ=0 EndX=4.25 EndY=0 EndZ=0
    g1: LineSegment StartX=4.25 StartY=0 StartZ=0 EndX=4.25 EndY=4.97229 EndZ=0
    g2: LineSegment StartX=4.22229 StartY=5 StartZ=0 EndX=0 EndY=5 EndZ=0
    g3: LineSegment StartX=2.499 StartY=0 StartZ=0 EndX=2.5 EndY=-0.2 EndZ=0
    g4: LineSegment StartX=2.5 StartY=-0.2 StartZ=0 EndX=2.5 EndY=-15.2 EndZ=0
    g5: LineSegment StartX=2.5 StartY=-15.2 StartZ=0 EndX=1.7 EndY=-16 EndZ=0
    g6: LineSegment StartX=1.7 StartY=-16 StartZ=0 EndX=0 EndY=-16 EndZ=0
    g7: LineSegment StartX=0 StartY=-16 StartZ=0 EndX=0 EndY=5 EndZ=0
    g8: ArcOfCircle CenterX=4.22229 CenterY=4.97229 CenterZ=0 NormalX=0 NormalY=0 NormalZ=1 AngleXU=0 Radius=0.02771 StartAngle=0 EndAngle=1.5708
  constraints (26):
    c: PointOnObject(g0,g-1)
    c: Horizontal(g0)
    c: Coincident(g1,g0)
    c: Vertical(g1)
    c: Horizontal(g2)
    c: Coincident(g3,g0)
    c: Coincident(g4,g3)
    c: Vertical(g4)
    c: Coincident(g5,g4)
    c: Coincident(g6,g5)
    c: Horizontal(g6)
    c: Coincident(g7,g6)
    c: Coincident(g7,g2)
    c: Vertical(g7)
    c: Tangent(g1,g8) = -1.5708
    c: Tangent(g2,g8) = -1.5708
    c: DistanceY(g5) = -0.8
    c: DistanceX(g5) = -0.8
    c: DistanceY(g5,g3) = 15.8
    c: DistanceY(g5,g0) = 16
    c: DistanceY(g0,g2) = 5
    c: DistanceX(g2,g0) = 4.25
    c: DistanceX(g6,g4) = 2.5
    c: DistanceX(g3,g0) = -0.001
    c: PointOnObject(g-1,g7)
    c: Radius(g8) = 0.02771
FEATURE [Part::Revolution] Revolve004
  Angle = 360
  Axis = (0,0,1)
  Base = (0,0,0)
  Solid = true
  Source = -> Sketch063
  Symmetric = false
FEATURE [Sketcher::SketchObject] Sketch064
  MapMode = 5
  Placement = pos=(0,0,5) rot=(0,0,1;0rad)
  Support = -> [Revolve004]
  sketch-geometry (7):
    g0: LineSegment StartX=2.34404 StartY=0 StartZ=0 EndX=1.17202 EndY=2.03 EndZ=0
    g1: LineSegment StartX=1.17202 StartY=2.03 StartZ=0 EndX=-1.17202 EndY=2.03 EndZ=0
    g2: LineSegment StartX=-1.17202 StartY=2.03 StartZ=0 EndX=-2.34404 EndY=0 EndZ=0
    g3: LineSegment StartX=-2.34404 StartY=0 StartZ=0 EndX=-1.17202 EndY=-2.03 EndZ=0
    g4: LineSegment StartX=-1.17202 StartY=-2.03 StartZ=0 EndX=1.17202 EndY=-2.03 EndZ=0
    g5: LineSegment StartX=1.17202 StartY=-2.03 StartZ=0 EndX=2.34404 EndY=0 EndZ=0
    g6: Circle [constr] CenterX=0 CenterY=0 CenterZ=0 NormalX=0 NormalY=0 NormalZ=1 AngleXU=0 Radius=2.34404
  constraints (16):
    c: Coincident(g0,g1)
    c: Coincident(g1,g2)
    c: Coincident(g2,g3)
    c: Coincident(g3,g4)
    c: Coincident(g4,g5)
    c: Coincident(g5,g0)
    c: Equal(g0, g1-g5) x5
    c: PointOnObject(g0,g6)
    c: PointOnObject(g1,g6)
    c: PointOnObject(g2,g6)
    c: PointOnObject(g3,g6)
    c: PointOnObject(g4,g6)
    c: PointOnObject(g5,g6)
    c: Horizontal(g4)
    c: DistanceY(g4,g0) = 4.06
    c: Coincident(g6,g-1)
FEATURE [PartDesign::Pocket] Pocket001006  label="Screw M5x16 ISO4762 8,8 A2K-001"
  Length = 4.06
  Length2 = 100
  Profile = -> Sketch064
  Type = 0
FEATURE [Part::Feature] Pocket001006001  label="Screw M5x16 ISO4762 8,8 A2K-002"
  Placement = pos=(0,31.5,0) rot=(0,0,1;0rad)
  shape: bbox 9.2 x 9.2 x 21 mm, 15 faces (baked)
FEATURE [Part::Feature] Pocket001006001001  label="Screw M5x16 ISO4762 8,8 A2K-003"
  Placement = pos=(0,74,0) rot=(0,0,1;0rad)
  shape: bbox 9.2 x 9.2 x 21 mm, 15 faces (baked)
FEATURE [Part::Feature] Pocket001006001001001  label="Screw M5x16 ISO4762 8,8 A2K-004"
  Placement = pos=(0,105.5,0) rot=(0,0,1;0rad)
  shape: bbox 9.2 x 9.2 x 21 mm, 15 faces (baked)
FEATURE [Part::Feature] Pocket001006001001002  label="Screw M5x16 ISO4762 8,8 A2K-005"
  Placement = pos=(486,0,0) rot=(0,0,1;0rad)
  shape: bbox 9.2 x 9.2 x 21 mm, 15 faces (baked)
FEATURE [Part::Feature] Pocket001006001001003  label="Screw M5x16 ISO4762 8,8 A2K-006"
  Placement = pos=(486,31.5,0) rot=(0,0,1;0rad)
  shape: bbox 9.2 x 9.2 x 21 mm, 15 faces (baked)
FEATURE [Part::Feature] Pocket001006001001004  label="Screw M5x16 ISO4762 8,8 A2K-007"
  Placement = pos=(486,74,0) rot=(0,0,1;0rad)
  shape: bbox 9.2 x 9.2 x 21 mm, 15 faces (baked)
FEATURE [Part::Feature] Pocket001006001001001001  label="Screw M5x16 ISO4762 8,8 A2K-008"
  Placement = pos=(486,105.5,0) rot=(0,0,1;0rad)
  shape: bbox 9.2 x 9.2 x 21 mm, 15 faces (baked)
FEATURE [Part::Box] Box021  label="Cube016"
  AttacherType = Attacher::AttachEngine3D
  Height = 3.75
  Length = 71
  Placement = pos=(0,-14,-10) rot=(1,0,0;1.5708rad)
  Width = 44
FEATURE [Part::Feature] Part__Feature046  label="SOLID"
  Placement = pos=(0,3.66461,0) rot=(0,0,1;0rad)
  shape: bbox 34 x 14.5 x 22 mm, 24 faces (baked)
FEATURE [Part::Feature] Part__Feature151  label="COMPOUND009"
  Placement = pos=(2.85933e-05,-4.58539,11.0094) rot=(0,1,0;3.14464rad)
  shape: bbox 17.02 x 1 x 18.57 mm, 36 faces, 2 solids (baked)
FEATURE [Part::Feature] Part__Feature152  label="SOLID105"
  Placement = pos=(2.85933e-05,11.9146,11.0094) rot=(0,1,0;3.14464rad)
  shape: bbox 17.02 x 1 x 18.57 mm, 18 faces (baked)
FEATURE [App::DocumentObjectGroup] Group006  label="Right"
  Group = -> [Box020,Cut002007,Cut002009]
FEATURE [App::DocumentObjectGroup] Group013  label="Rods"
  Group = -> [Cylinder,Cylinder001]
FEATURE [App::DocumentObjectGroup] Group015  label="Arduino Standoff"
  Group = -> [Part007,Part009,Part010,Part011,Part012,Part018,Part020,Part021]
FEATURE [App::DocumentObjectGroup] Group005  label="Left"
  Group = -> [Box005,Cut002008,Cut002006,Group015]
FEATURE [App::DocumentObjectGroup] Group004  label="Frame"
  Group = -> [Group005,Group006,Part017]
FEATURE [Part::Feature] Part__Feature203  label="SOLID155"
  Placement = pos=(0,3.66461,0) rot=(0,0,1;0rad)
FEATURE [App::Part] Part016  label="GT2-TPulley"
  Group = -> [Array002,Cylinder013,Chamfer015,Cylinder015,Cut006,Fusion007002,Chamfer016,Cylinder016,Cylinder014,Cylinder017,Cut007,Cut001001,Part__Feature203]
  License = CC BY 3.0
  LicenseURL = http://creativecommons.org/licenses/by/3.0/
  Origin = -> Origin016
FEATURE [Part::Feature] Part__Feature218  label="COMPOUND010"
  Placement = pos=(2.85933e-05,-4.58539,11.0094) rot=(0,1,0;3.14464rad)
  shape: bbox 17.02 x 1 x 18.57 mm, 36 faces, 2 solids (baked)
FEATURE [Part::Feature] Part__Feature254  label="SOLID205"
  Placement = pos=(0,3.66461,0) rot=(0,0,1;0rad)
  shape: bbox 34 x 14.5 x 22 mm, 24 faces (baked)
FEATURE [Part::Feature] Part__Feature296  label="SOLID247"
  Placement = pos=(2.85933e-05,11.9146,11.0094) rot=(0,1,0;3.14464rad)
  shape: bbox 17.02 x 1 x 18.57 mm, 18 faces (baked)
FEATURE [Part::Feature] Part__Feature325  label="COMPOUND011"
  Placement = pos=(2.85933e-05,-4.58539,11.0094) rot=(0,1,0;3.14464rad)
  shape: bbox 17.02 x 1 x 18.57 mm, 36 faces, 2 solids (baked)
FEATURE [Part::Feature] Part__Feature361  label="SOLID311"
  Placement = pos=(0,3.66461,0) rot=(0,0,1;0rad)
  shape: bbox 34 x 14.5 x 22 mm, 24 faces (baked)
FEATURE [Part::Feature] Part__Feature403  label="SOLID353"
  Placement = pos=(2.85933e-05,11.9146,11.0094) rot=(0,1,0;3.14464rad)
  shape: bbox 17.02 x 1 x 18.57 mm, 18 faces (baked)
FEATURE [Part::Feature] Part__Feature432  label="COMPOUND012"
  Placement = pos=(2.85933e-05,-4.58539,11.0094) rot=(0,1,0;3.14464rad)
  shape: bbox 17.02 x 1 x 18.57 mm, 36 faces, 2 solids (baked)
FEATURE [Part::Feature] Part__Feature468  label="SOLID417"
  Placement = pos=(0,3.66461,0) rot=(0,0,1;0rad)
  shape: bbox 34 x 14.5 x 22 mm, 24 faces (baked)
FEATURE [Part::Feature] Part__Feature510  label="SOLID459"
  Placement = pos=(2.85933e-05,11.9146,11.0094) rot=(0,1,0;3.14464rad)
  shape: bbox 17.02 x 1 x 18.57 mm, 18 faces (baked)
FEATURE [App::Part] Part039  label="Screws"
  Group = -> [Sketch063,Pocket001006,Sketch064,Revolve004,Pocket001006001,Pocket001006001001,Pocket001006001001001,Pocket001006001001002,Pocket001006001001003,Pocket001006001001004,Pocket001006001001001001]
  License = CC BY 3.0
  LicenseURL = http://creativecommons.org/licenses/by/3.0/
  Origin = -> Origin049
  Placement = pos=(97,7.25,12) rot=(0,0,1;0rad)
FEATURE [App::DocumentObjectGroup] Group014  label="SK8"
  Group = -> [Part031,Part033,Part035,Part037,Part039]
FEATURE [App::DocumentObjectGroup] Group009  label="x"
  Group = -> [Group014,Group013]
FEATURE [Sketcher::SketchObject] Sketch065
  MapMode = 5
  Placement = pos=(0,0,0) rot=(0.57735,0.57735,0.57735;2.0944rad)
  sketch-geometry (9):
    g0: LineSegment StartX=1.499 StartY=0 StartZ=0 EndX=2.75 EndY=0 EndZ=0
    g1: LineSegment StartX=2.75 StartY=0 StartZ=0 EndX=2.75 EndY=2.97229 EndZ=0
    g2: LineSegment StartX=2.72229 StartY=3 StartZ=0 EndX=0 EndY=3 EndZ=0
    g3: LineSegment StartX=1.499 StartY=0 StartZ=0 EndX=1.5 EndY=-0.2 EndZ=0
    g4: LineSegment StartX=1.5 StartY=-0.2 StartZ=0 EndX=1.5 EndY=-9.5 EndZ=0
    g5: LineSegment StartX=1.5 StartY=-9.5 StartZ=0 EndX=1 EndY=-10 EndZ=0
    g6: LineSegment StartX=1 StartY=-10 StartZ=0 EndX=0 EndY=-10 EndZ=0
    g7: LineSegment StartX=0 StartY=-10 StartZ=0 EndX=0 EndY=3 EndZ=0
    g8: ArcOfCircle CenterX=2.72229 CenterY=2.97229 CenterZ=0 NormalX=0 NormalY=0 NormalZ=1 AngleXU=0 Radius=0.02771 StartAngle=0 EndAngle=1.5708
  constraints (26):
    c: PointOnObject(g0,g-1)
    c: Horizontal(g0)
    c: Coincident(g1,g0)
    c: Vertical(g1)
    c: Horizontal(g2)
    c: Coincident(g3,g0)
    c: Coincident(g4,g3)
    c: Vertical(g4)
    c: Coincident(g5,g4)
    c: Coincident(g6,g5)
    c: Horizontal(g6)
    c: Coincident(g7,g6)
    c: Coincident(g7,g2)
    c: Vertical(g7)
    c: Tangent(g1,g8) = -1.5708
    c: Tangent(g2,g8) = -1.5708
    c: DistanceY(g5) = -0.5
    c: DistanceX(g5) = -0.5
    c: DistanceY(g5,g3) = 9.8
    c: DistanceY(g5,g0) = 10
    c: DistanceY(g0,g2) = 3
    c: DistanceX(g2,g0) = 2.75
    c: DistanceX(g6,g4) = 1.5
    c: DistanceX(g3,g0) = -0.001
    c: PointOnObject(g-1,g7)
    c: Radius(g8) = 0.02771
FEATURE [Part::Revolution] Revolve005
  Angle = 360
  Axis = (0,0,1)
  Base = (0,0,0)
  Solid = true
  Source = -> Sketch065
  Symmetric = false
FEATURE [Sketcher::SketchObject] Sketch066
  MapMode = 5
  Placement = pos=(0,0,3) rot=(0,0,1;0rad)
  Support = -> [Revolve005]
  sketch-geometry (7):
    g0: LineSegment StartX=1.47802 StartY=0 StartZ=0 EndX=0.739008 EndY=1.28 EndZ=0
    g1: LineSegment StartX=0.739008 StartY=1.28 StartZ=0 EndX=-0.739008 EndY=1.28 EndZ=0
    g2: LineSegment StartX=-0.739008 StartY=1.28 StartZ=0 EndX=-1.47802 EndY=0 EndZ=0
    g3: LineSegment StartX=-1.47802 StartY=0 StartZ=0 EndX=-0.739008 EndY=-1.28 EndZ=0
    g4: LineSegment StartX=-0.739008 StartY=-1.28 StartZ=0 EndX=0.739008 EndY=-1.28 EndZ=0
    g5: LineSegment StartX=0.739008 StartY=-1.28 StartZ=0 EndX=1.47802 EndY=0 EndZ=0
    g6: Circle [constr] CenterX=0 CenterY=0 CenterZ=0 NormalX=0 NormalY=0 NormalZ=1 AngleXU=0 Radius=1.47802
  constraints (16):
    c: Coincident(g0,g1)
    c: Coincident(g1,g2)
    c: Coincident(g2,g3)
    c: Coincident(g3,g4)
    c: Coincident(g4,g5)
    c: Coincident(g5,g0)
    c: Equal(g0, g1-g5) x5
    c: PointOnObject(g0,g6)
    c: PointOnObject(g1,g6)
    c: PointOnObject(g2,g6)
    c: PointOnObject(g3,g6)
    c: PointOnObject(g4,g6)
    c: PointOnObject(g5,g6)
    c: Horizontal(g4)
    c: DistanceY(g4,g0) = 2.56
    c: Coincident(g6,g-1)
FEATURE [PartDesign::Pocket] Pocket001006001001001002  label="Screw M3x10 ISO4762 8,8 A2K-001"
  Length = 2.56
  Length2 = 100
  Profile = -> Sketch066
  Type = 0
FEATURE [Part::Feature] Pocket001006001001001002001  label="Screw M3x10 ISO4762 8,8 A2K-002"
  Placement = pos=(0,24,0) rot=(0,0,1;0rad)
  shape: bbox 5.953 x 5.953 x 13 mm, 15 faces (baked)
FEATURE [Part::Feature] Pocket001006001001001002001001  label="Screw M3x10 ISO4762 8,8 A2K-003"
  Placement = pos=(52.5,24,0) rot=(0,0,1;0rad)
  shape: bbox 5.953 x 5.953 x 13 mm, 15 faces (baked)
FEATURE [Part::Feature] Pocket001006001001001002001002  label="Screw M3x10 ISO4762 8,8 A2K-004"
  Placement = pos=(52.5,0,0) rot=(0,0,1;0rad)
  shape: bbox 5.953 x 5.953 x 13 mm, 15 faces (baked)
FEATURE [Part::Feature] Pocket001006001001001002001003  label="Screw M3x10 ISO4762 8,8 A2K-005"
  Placement = pos=(0,74,0) rot=(0,0,1;0rad)
  shape: bbox 5.953 x 5.953 x 13 mm, 15 faces (baked)
FEATURE [Part::Feature] Pocket001006001001001002001003001  label="Screw M3x10 ISO4762 8,8 A2K-006"
  Placement = pos=(0,98,0) rot=(0,0,1;0rad)
  shape: bbox 5.953 x 5.953 x 13 mm, 15 faces (baked)
FEATURE [Part::Feature] Pocket001006001001001002001003001001  label="Screw M3x10 ISO4762 8,8 A2K-007"
  Placement = pos=(52.5,98,0) rot=(0,0,1;0rad)
  shape: bbox 5.953 x 5.953 x 13 mm, 15 faces (baked)
FEATURE [Part::Feature] Pocket001006001001001002001003001002  label="Screw M3x10 ISO4762 8,8 A2K-008"
  Placement = pos=(52.5,74,0) rot=(0,0,1;0rad)
  shape: bbox 5.953 x 5.953 x 13 mm, 15 faces (baked)
FEATURE [App::Part] Part040  label="Screw M3x10 ISO4762 8,8 A2K"
  Group = -> [Sketch066,Sketch065,Pocket001006001001001002,Revolve005,Pocket001006001001001002001,Pocket001006001001001002001001,Pocket001006001001001002001002,Pocket001006001001001002001003,Pocket001006001001001002001003001,Pocket001006001001001002001003001001,Pocket001006001001001002001003001002]
  License = CC BY 3.0
  LicenseURL = http://creativecommons.org/licenses/by/3.0/
  Origin = -> Origin050
  Placement = pos=(9.24,10.9,3.75) rot=(0,0,1;0rad)
FEATURE [Part::Box] Box022  label="Cube017"
  AttacherType = Attacher::AttachEngine3D
  Height = 3.75
  Length = 71
  Width = 120
FEATURE [Part::Feature] Part__Feature538  label="SOLID487"
  Placement = pos=(-14.0044,1.66024,-2.0407e-11) rot=(0,0,1;0rad)
  shape: bbox 23 x 13.62 x 13.6 mm, 69 faces (baked)
FEATURE [Part::Feature] Part__Feature539  label="COMPOUND013"
  Placement = pos=(2.85933e-05,-4.58539,11.0094) rot=(0,1,0;3.14464rad)
  shape: bbox 17.02 x 1 x 18.57 mm, 36 faces, 2 solids (baked)
FEATURE [Part::Feature] Part__Feature575  label="SOLID523"
  Placement = pos=(0,3.66461,0) rot=(0,0,1;0rad)
  shape: bbox 34 x 14.5 x 22 mm, 24 faces (baked)
FEATURE [Part::Feature] Part__Feature617  label="SOLID565"
  Placement = pos=(2.85933e-05,11.9146,11.0094) rot=(0,1,0;3.14464rad)
  shape: bbox 17.02 x 1 x 18.57 mm, 18 faces (baked)
FEATURE [Part::Feature] Part__Feature629  label="SOLID577"
  Placement = pos=(-14.0044,1.66024,-2.0408e-11) rot=(-1,0,0;0.595235rad)
  shape: bbox 24 x 15.94 x 15.94 mm, 34 faces (baked)
FEATURE [App::Part] LU8MM004
  Group = -> [Part__Feature538,Part__Feature629]
  License = CC BY 3.0
  LicenseURL = http://creativecommons.org/licenses/by/3.0/
  Origin = -> Origin051
  Placement = pos=(-1.66024,1.66024,11) rot=(0,0,-1;1.5708rad)
FEATURE [App::Part] SCV8UU004  label="SCV8UU-005"
  Group = -> [Part__Feature575,LU8MM004,Part__Feature539,Part__Feature617]
  License = CC BY 3.0
  LicenseURL = http://creativecommons.org/licenses/by/3.0/
  Origin = -> Origin052
  Placement = pos=(18,11.9,25.75) rot=(1,0,0;-3.14159rad)
FEATURE [Part::Feature] Part__Feature646  label="COMPOUND014"
  Placement = pos=(2.85933e-05,-4.58539,11.0094) rot=(0,1,0;3.14464rad)
  shape: bbox 17.02 x 1 x 18.57 mm, 36 faces, 2 solids (baked)
FEATURE [Part::Feature] Part__Feature682  label="SOLID629"
  Placement = pos=(0,3.66461,0) rot=(0,0,1;0rad)
  shape: bbox 34 x 14.5 x 22 mm, 24 faces (baked)
FEATURE [Part::Feature] Part__Feature724  label="SOLID671"
  Placement = pos=(2.85933e-05,11.9146,11.0094) rot=(0,1,0;3.14464rad)
  shape: bbox 17.02 x 1 x 18.57 mm, 18 faces (baked)
FEATURE [Part::Feature] Part__Feature753  label="COMPOUND015"
  Placement = pos=(2.85933e-05,-4.58539,11.0094) rot=(0,1,0;3.14464rad)
  shape: bbox 17.02 x 1 x 18.57 mm, 36 faces, 2 solids (baked)
FEATURE [Part::Feature] Part__Feature789  label="SOLID735"
  Placement = pos=(0,3.66461,0) rot=(0,0,1;0rad)
  shape: bbox 34 x 14.5 x 22 mm, 24 faces (baked)
FEATURE [Part::Feature] Part__Feature831  label="SOLID777"
  Placement = pos=(2.85933e-05,11.9146,11.0094) rot=(0,1,0;3.14464rad)
  shape: bbox 17.02 x 1 x 18.57 mm, 18 faces (baked)
FEATURE [Part::Feature] Part__Feature864  label="COMPOUND016"
  Placement = pos=(2.85933e-05,-4.58539,11.0094) rot=(0,1,0;3.14464rad)
  shape: bbox 17.02 x 1 x 18.57 mm, 36 faces, 2 solids (baked)
FEATURE [Part::Feature] Part__Feature875  label="SOLID820"
  Placement = pos=(0,3.66461,0) rot=(0,0,1;0rad)
  shape: bbox 34 x 14.5 x 22 mm, 24 faces (baked)
FEATURE [Part::Feature] Part__Feature941  label="SOLID886"
  Placement = pos=(2.85933e-05,11.9146,11.0094) rot=(0,1,0;3.14464rad)
  shape: bbox 17.02 x 1 x 18.57 mm, 18 faces (baked)
FEATURE [Sketcher::SketchObject] Sketch067
  MapMode = 5
  Placement = pos=(0,0,0) rot=(0.57735,0.57735,0.57735;2.0944rad)
  sketch-geometry (9):
    g0: LineSegment StartX=1.499 StartY=0 StartZ=0 EndX=2.75 EndY=0 EndZ=0
    g1: LineSegment StartX=2.75 StartY=0 StartZ=0 EndX=2.75 EndY=2.97229 EndZ=0
    g2: LineSegment StartX=2.72229 StartY=3 StartZ=0 EndX=0 EndY=3 EndZ=0
    g3: LineSegment StartX=1.499 StartY=0 StartZ=0 EndX=1.5 EndY=-0.2 EndZ=0
    g4: LineSegment StartX=1.5 StartY=-0.2 StartZ=0 EndX=1.5 EndY=-9.5 EndZ=0
    g5: LineSegment StartX=1.5 StartY=-9.5 StartZ=0 EndX=1 EndY=-10 EndZ=0
    g6: LineSegment StartX=1 StartY=-10 StartZ=0 EndX=0 EndY=-10 EndZ=0
    g7: LineSegment StartX=0 StartY=-10 StartZ=0 EndX=0 EndY=3 EndZ=0
    g8: ArcOfCircle CenterX=2.72229 CenterY=2.97229 CenterZ=0 NormalX=0 NormalY=0 NormalZ=1 AngleXU=0 Radius=0.02771 StartAngle=0 EndAngle=1.5708
  constraints (26):
    c: PointOnObject(g0,g-1)
    c: Horizontal(g0)
    c: Coincident(g1,g0)
    c: Vertical(g1)
    c: Horizontal(g2)
    c: Coincident(g3,g0)
    c: Coincident(g4,g3)
    c: Vertical(g4)
    c: Coincident(g5,g4)
    c: Coincident(g6,g5)
    c: Horizontal(g6)
    c: Coincident(g7,g6)
    c: Coincident(g7,g2)
    c: Vertical(g7)
    c: Tangent(g1,g8) = -1.5708
    c: Tangent(g2,g8) = -1.5708
    c: DistanceY(g5) = -0.5
    c: DistanceX(g5) = -0.5
    c: DistanceY(g5,g3) = 9.8
    c: DistanceY(g5,g0) = 10
    c: DistanceY(g0,g2) = 3
    c: DistanceX(g2,g0) = 2.75
    c: DistanceX(g6,g4) = 1.5
    c: DistanceX(g3,g0) = -0.001
    c: PointOnObject(g-1,g7)
    c: Radius(g8) = 0.02771
FEATURE [Part::Revolution] Revolve006
  Angle = 360
  Axis = (0,0,1)
  Base = (0,0,0)
  Solid = true
  Source = -> Sketch067
  Symmetric = false
FEATURE [Sketcher::SketchObject] Sketch068
  MapMode = 5
  Placement = pos=(0,0,3) rot=(0,0,1;0rad)
  Support = -> [Revolve006]
  sketch-geometry (7):
    g0: LineSegment StartX=1.47802 StartY=0 StartZ=0 EndX=0.739008 EndY=1.28 EndZ=0
    g1: LineSegment StartX=0.739008 StartY=1.28 StartZ=0 EndX=-0.739008 EndY=1.28 EndZ=0
    g2: LineSegment StartX=-0.739008 StartY=1.28 StartZ=0 EndX=-1.47802 EndY=0 EndZ=0
    g3: LineSegment StartX=-1.47802 StartY=0 StartZ=0 EndX=-0.739008 EndY=-1.28 EndZ=0
    g4: LineSegment StartX=-0.739008 StartY=-1.28 StartZ=0 EndX=0.739008 EndY=-1.28 EndZ=0
    g5: LineSegment StartX=0.739008 StartY=-1.28 StartZ=0 EndX=1.47802 EndY=0 EndZ=0
    g6: Circle [constr] CenterX=0 CenterY=0 CenterZ=0 NormalX=0 NormalY=0 NormalZ=1 AngleXU=0 Radius=1.47802
  constraints (16):
    c: Coincident(g0,g1)
    c: Coincident(g1,g2)
    c: Coincident(g2,g3)
    c: Coincident(g3,g4)
    c: Coincident(g4,g5)
    c: Coincident(g5,g0)
    c: Equal(g0, g1-g5) x5
    c: PointOnObject(g0,g6)
    c: PointOnObject(g1,g6)
    c: PointOnObject(g2,g6)
    c: PointOnObject(g3,g6)
    c: PointOnObject(g4,g6)
    c: PointOnObject(g5,g6)
    c: Horizontal(g4)
    c: DistanceY(g4,g0) = 2.56
    c: Coincident(g6,g-1)
FEATURE [PartDesign::Pocket] Pocket001006001001001002001003001003  label="Screw M3x10 ISO4762 8,8 A2K-009"
  Length = 2.56
  Length2 = 100
  Profile = -> Sketch068
  Type = 0
FEATURE [Part::Feature] Pocket001006001001001002001003001003001  label="Screw M3x10 ISO4762 8,8 A2K-010"
  Placement = pos=(24,0,0) rot=(0,0,1;0rad)
  shape: bbox 5.953 x 5.953 x 13 mm, 15 faces (baked)
FEATURE [Part::Feature] Pocket001006001001001002001003001003001001  label="Screw M3x10 ISO4762 8,8 A2K-011"
  Placement = pos=(35,0,0) rot=(0,0,1;0rad)
  shape: bbox 5.953 x 5.953 x 13 mm, 15 faces (baked)
FEATURE [Part::Feature] Pocket001006001001001002001003001003001001001  label="Screw M3x10 ISO4762 8,8 A2K-012"
  Placement = pos=(59,0,0) rot=(0,0,1;0rad)
  shape: bbox 5.953 x 5.953 x 13 mm, 15 faces (baked)
FEATURE [Part::Feature] Pocket001006001001001002001003001003001001002  label="Screw M3x10 ISO4762 8,8 A2K-013"
  Placement = pos=(0,-103.5,0) rot=(0,0,1;0rad)
  shape: bbox 5.953 x 5.953 x 13 mm, 15 faces (baked)
FEATURE [Part::Feature] Pocket001006001001001002001003001003001001002001  label="Screw M3x10 ISO4762 8,8 A2K-014"
  Placement = pos=(24,-103.5,0) rot=(0,0,1;0rad)
  shape: bbox 5.953 x 5.953 x 13 mm, 15 faces (baked)
FEATURE [Part::Feature] Pocket001006001001001002001003001003001001002001001  label="Screw M3x10 ISO4762 8,8 A2K-015"
  Placement = pos=(35,-103.5,0) rot=(0,0,1;0rad)
  shape: bbox 5.953 x 5.953 x 13 mm, 15 faces (baked)
FEATURE [Part::Feature] Pocket001006001001001002001003001003001001002001001001  label="Screw M3x10 ISO4762 8,8 A2K-016"
  Placement = pos=(59,-103.5,0) rot=(0,0,1;0rad)
  shape: bbox 5.953 x 5.953 x 13 mm, 15 faces (baked)
FEATURE [App::Part] Part043  label="Screw M3x10 ISO4762 8,8 A2K001"
  Group = -> [Sketch068,Sketch067,Pocket001006001001001002001003001003,Revolve006,Pocket001006001001001002001003001003001,Pocket001006001001001002001003001003001001,Pocket001006001001001002001003001003001001001,Pocket001006001001001002001003001003001001002,Pocket001006001001001002001003001003001001002001,Pocket001006001001001002001003001003001001002001001,Pocket001006001001001002001003001003001001002001001001]
  License = CC BY 3.0
  LicenseURL = http://creativecommons.org/licenses/by/3.0/
  Origin = -> Origin061
  Placement = pos=(6,8.23,0) rot=(1,0,0;-3.14159rad)
FEATURE [Part::Feature] Part__Feature953  label="SOLID898"
  Placement = pos=(-14.0044,1.66024,-2.0407e-11) rot=(0,0,1;0rad)
  shape: bbox 23 x 13.62 x 13.6 mm, 69 faces (baked)
FEATURE [Part::Feature] Part__Feature954  label="SOLID899"
  Placement = pos=(-14.0044,1.66024,-2.0408e-11) rot=(-1,0,0;0.595235rad)
  shape: bbox 24 x 15.94 x 15.94 mm, 34 faces (baked)
FEATURE [App::Part] LU8MM005
  Group = -> [Part__Feature953,Part__Feature954]
  License = CC BY 3.0
  LicenseURL = http://creativecommons.org/licenses/by/3.0/
  Origin = -> Origin055
  Placement = pos=(-1.66024,1.66024,11) rot=(0,0,-1;1.5708rad)
FEATURE [App::Part] SCV8UU005  label="SCV8UU-006"
  Group = -> [Part__Feature682,LU8MM005,Part__Feature646,Part__Feature724]
  License = CC BY 3.0
  LicenseURL = http://creativecommons.org/licenses/by/3.0/
  Origin = -> Origin056
  Placement = pos=(53,11.9,25.75) rot=(1,0,0;-3.14159rad)
FEATURE [Part::Feature] Part__Feature955  label="SOLID900"
  Placement = pos=(-14.0044,1.66024,-2.0407e-11) rot=(0,0,1;0rad)
  shape: bbox 23 x 13.62 x 13.6 mm, 69 faces (baked)
FEATURE [Part::Feature] Part__Feature956  label="SOLID901"
  Placement = pos=(-14.0044,1.66024,-2.0408e-11) rot=(-1,0,0;0.595235rad)
  shape: bbox 24 x 15.94 x 15.94 mm, 34 faces (baked)
FEATURE [App::Part] LU8MM006
  Group = -> [Part__Feature955,Part__Feature956]
  License = CC BY 3.0
  LicenseURL = http://creativecommons.org/licenses/by/3.0/
  Origin = -> Origin057
  Placement = pos=(-1.66024,1.66024,11) rot=(0,0,-1;1.5708rad)
FEATURE [App::Part] SCV8UU006  label="SCV8UU-007"
  Group = -> [Part__Feature789,LU8MM006,Part__Feature753,Part__Feature831]
  License = CC BY 3.0
  LicenseURL = http://creativecommons.org/licenses/by/3.0/
  Origin = -> Origin058
  Placement = pos=(18,115.4,25.75) rot=(1,0,0;-3.14159rad)
FEATURE [Part::Feature] Part__Feature957  label="SOLID902"
  Placement = pos=(-14.0044,1.66024,-2.0407e-11) rot=(0,0,1;0rad)
  shape: bbox 23 x 13.62 x 13.6 mm, 69 faces (baked)
FEATURE [Part::Feature] Part__Feature958  label="SOLID903"
  Placement = pos=(-14.0044,1.66024,-2.0408e-11) rot=(-1,0,0;0.595235rad)
  shape: bbox 24 x 15.94 x 15.94 mm, 34 faces (baked)
FEATURE [App::Part] LU8MM007
  Group = -> [Part__Feature957,Part__Feature958]
  License = CC BY 3.0
  LicenseURL = http://creativecommons.org/licenses/by/3.0/
  Origin = -> Origin059
  Placement = pos=(-1.66024,1.66024,11) rot=(0,0,-1;1.5708rad)
FEATURE [App::Part] SCV8UU007  label="SCV8UU-008"
  Group = -> [Part__Feature875,LU8MM007,Part__Feature864,Part__Feature941]
  License = CC BY 3.0
  LicenseURL = http://creativecommons.org/licenses/by/3.0/
  Origin = -> Origin060
  Placement = pos=(53,115.4,25.75) rot=(1,0,0;-3.14159rad)
FEATURE [Part::Feature] Part__Feature959  label="SOLID904"
  Placement = pos=(-14.0044,1.66024,-2.0407e-11) rot=(0,0,1;0rad)
  shape: bbox 23 x 13.62 x 13.6 mm, 69 faces (baked)
FEATURE [Part::Feature] Part__Feature960  label="SOLID905"
  Placement = pos=(-14.0044,1.66024,-2.0408e-11) rot=(-1,0,0;0.595235rad)
  shape: bbox 24 x 15.94 x 15.94 mm, 34 faces (baked)
FEATURE [App::Part] LU8MM
  Group = -> [Part__Feature959,Part__Feature960]
  License = CC BY 3.0
  LicenseURL = http://creativecommons.org/licenses/by/3.0/
  Origin = -> Origin040
  Placement = pos=(-1.66024,1.66024,11) rot=(0,0,-1;1.5708rad)
FEATURE [App::Part] SCV8UU  label="SCV8UU-001"
  Group = -> [Part__Feature046,LU8MM,Part__Feature151,Part__Feature152]
  License = CC BY 3.0
  LicenseURL = http://creativecommons.org/licenses/by/3.0/
  Origin = -> Origin041
  Placement = pos=(12.9,22.9,-22) rot=(0,0,1;1.5708rad)
FEATURE [Part::Feature] Part__Feature961  label="SOLID906"
  Placement = pos=(-14.0044,1.66024,-2.0407e-11) rot=(0,0,1;0rad)
  shape: bbox 23 x 13.62 x 13.6 mm, 69 faces (baked)
FEATURE [Part::Feature] Part__Feature962  label="SOLID907"
  Placement = pos=(-14.0044,1.66024,-2.0408e-11) rot=(-1,0,0;0.595235rad)
  shape: bbox 24 x 15.94 x 15.94 mm, 34 faces (baked)
FEATURE [App::Part] LU8MM003
  Group = -> [Part__Feature961,Part__Feature962]
  License = CC BY 3.0
  LicenseURL = http://creativecommons.org/licenses/by/3.0/
  Origin = -> Origin047
  Placement = pos=(-1.66024,1.66024,11) rot=(0,0,-1;1.5708rad)
FEATURE [App::Part] SCV8UU003  label="SCV8UU-004"
  Group = -> [Part__Feature468,LU8MM003,Part__Feature432,Part__Feature510]
  License = CC BY 3.0
  LicenseURL = http://creativecommons.org/licenses/by/3.0/
  Origin = -> Origin048
  Placement = pos=(65.4,96.9,-22) rot=(0,0,1;1.5708rad)
FEATURE [Part::Feature] Part__Feature963  label="SOLID908"
  Placement = pos=(-14.0044,1.66024,-2.0407e-11) rot=(0,0,1;0rad)
  shape: bbox 23 x 13.62 x 13.6 mm, 69 faces (baked)
FEATURE [Part::Feature] Part__Feature964  label="SOLID909"
  Placement = pos=(-14.0044,1.66024,-2.0408e-11) rot=(-1,0,0;0.595235rad)
  shape: bbox 24 x 15.94 x 15.94 mm, 34 faces (baked)
FEATURE [App::Part] LU8MM002
  Group = -> [Part__Feature963,Part__Feature964]
  License = CC BY 3.0
  LicenseURL = http://creativecommons.org/licenses/by/3.0/
  Origin = -> Origin045
  Placement = pos=(-1.66024,1.66024,11) rot=(0,0,-1;1.5708rad)
FEATURE [App::Part] SCV8UU002  label="SCV8UU-003"
  Group = -> [Part__Feature361,LU8MM002,Part__Feature325,Part__Feature403]
  License = CC BY 3.0
  LicenseURL = http://creativecommons.org/licenses/by/3.0/
  Origin = -> Origin046
  Placement = pos=(12.9,96.9,-22) rot=(0,0,1;1.5708rad)
FEATURE [Part::Feature] Part__Feature965  label="SOLID910"
  Placement = pos=(-14.0044,1.66024,-2.0407e-11) rot=(0,0,1;0rad)
  shape: bbox 23 x 13.62 x 13.6 mm, 69 faces (baked)
FEATURE [Part::Feature] Part__Feature966  label="SOLID911"
  Placement = pos=(-14.0044,1.66024,-2.0408e-11) rot=(-1,0,0;0.595235rad)
  shape: bbox 24 x 15.94 x 15.94 mm, 34 faces (baked)
FEATURE [App::Part] LU8MM001
  Group = -> [Part__Feature965,Part__Feature966]
  License = CC BY 3.0
  LicenseURL = http://creativecommons.org/licenses/by/3.0/
  Origin = -> Origin043
  Placement = pos=(-1.66024,1.66024,11) rot=(0,0,-1;1.5708rad)
FEATURE [App::Part] SCV8UU001  label="SCV8UU-002"
  Group = -> [Part__Feature254,LU8MM001,Part__Feature218,Part__Feature296]
  License = CC BY 3.0
  LicenseURL = http://creativecommons.org/licenses/by/3.0/
  Origin = -> Origin044
  Placement = pos=(65.4,22.9,-22) rot=(0,0,1;1.5708rad)
FEATURE [Part::Box] Box023  label="Cube018"
  AttacherType = Attacher::AttachEngine3D
  Height = 3.75
  Length = 71
  Width = 120
FEATURE [Part::Feature] Part__Feature967  label="SHF010"
  shape: bbox 22.8 x 7.577 x 7.577 mm, 30 faces (baked)
FEATURE [Part::Feature] Part__Feature968  label="SHF011"
  shape: bbox 42 x 24 x 10 mm, 87 faces (baked)
FEATURE [App::Part] SHF009  label="SHF8_002"
  Group = -> [Part__Feature968,Part__Feature967]
  License = CC BY 3.0
  LicenseURL = http://creativecommons.org/licenses/by/3.0/
  Origin = -> Origin063
  Placement = pos=(53,-14,14.7) rot=(0.249244,0.684791,0.684791;-2.65306rad)
FEATURE [Part::Box] Box024  label="Cube019"
  AttacherType = Attacher::AttachEngine3D
  Height = 3.75
  Length = 71
  Placement = pos=(0,339.75,-10) rot=(1,0,0;1.5708rad)
  Width = 44
FEATURE [Sketcher::SketchObject] Sketch071
  MapMode = 5
  Placement = pos=(0,0,0) rot=(0.57735,0.57735,0.57735;2.0944rad)
  sketch-geometry (9):
    g0: LineSegment StartX=2.499 StartY=0 StartZ=0 EndX=4.25 EndY=0 EndZ=0
    g1: LineSegment StartX=4.25 StartY=0 StartZ=0 EndX=4.25 EndY=4.97229 EndZ=0
    g2: LineSegment StartX=4.22229 StartY=5 StartZ=0 EndX=0 EndY=5 EndZ=0
    g3: LineSegment StartX=2.499 StartY=0 StartZ=0 EndX=2.5 EndY=-0.2 EndZ=0
    g4: LineSegment StartX=2.5 StartY=-0.2 StartZ=0 EndX=2.5 EndY=-19.2 EndZ=0
    g5: LineSegment StartX=2.5 StartY=-19.2 StartZ=0 EndX=1.7 EndY=-20 EndZ=0
    g6: LineSegment StartX=1.7 StartY=-20 StartZ=0 EndX=0 EndY=-20 EndZ=0
    g7: LineSegment StartX=0 StartY=-20 StartZ=0 EndX=0 EndY=5 EndZ=0
    g8: ArcOfCircle CenterX=4.22229 CenterY=4.97229 CenterZ=0 NormalX=0 NormalY=0 NormalZ=1 AngleXU=0 Radius=0.02771 StartAngle=0 EndAngle=1.5708
  constraints (26):
    c: PointOnObject(g0,g-1)
    c: Horizontal(g0)
    c: Coincident(g1,g0)
    c: Vertical(g1)
    c: Horizontal(g2)
    c: Coincident(g3,g0)
    c: Coincident(g4,g3)
    c: Vertical(g4)
    c: Coincident(g5,g4)
    c: Coincident(g6,g5)
    c: Horizontal(g6)
    c: Coincident(g7,g6)
    c: Coincident(g7,g2)
    c: Vertical(g7)
    c: Tangent(g1,g8) = -1.5708
    c: Tangent(g2,g8) = -1.5708
    c: DistanceY(g5) = -0.8
    c: DistanceX(g5) = -0.8
    c: DistanceY(g5,g3) = 19.8
    c: DistanceY(g5,g0) = 20
    c: DistanceY(g0,g2) = 5
    c: DistanceX(g2,g0) = 4.25
    c: DistanceX(g6,g4) = 2.5
    c: DistanceX(g3,g0) = -0.001
    c: PointOnObject(g-1,g7)
    c: Radius(g8) = 0.02771
FEATURE [Part::Revolution] Revolve008
  Angle = 360
  Axis = (0,0,1)
  Base = (0,0,0)
  Solid = true
  Source = -> Sketch071
  Symmetric = false
FEATURE [Sketcher::SketchObject] Sketch072
  MapMode = 5
  Placement = pos=(0,0,5) rot=(0,0,1;0rad)
  Support = -> [Revolve008]
  sketch-geometry (7):
    g0: LineSegment StartX=2.34404 StartY=0 StartZ=0 EndX=1.17202 EndY=2.03 EndZ=0
    g1: LineSegment StartX=1.17202 StartY=2.03 StartZ=0 EndX=-1.17202 EndY=2.03 EndZ=0
    g2: LineSegment StartX=-1.17202 StartY=2.03 StartZ=0 EndX=-2.34404 EndY=0 EndZ=0
    g3: LineSegment StartX=-2.34404 StartY=0 StartZ=0 EndX=-1.17202 EndY=-2.03 EndZ=0
    g4: LineSegment StartX=-1.17202 StartY=-2.03 StartZ=0 EndX=1.17202 EndY=-2.03 EndZ=0
    g5: LineSegment StartX=1.17202 StartY=-2.03 StartZ=0 EndX=2.34404 EndY=0 EndZ=0
    g6: Circle [constr] CenterX=0 CenterY=0 CenterZ=0 NormalX=0 NormalY=0 NormalZ=1 AngleXU=0 Radius=2.34404
  constraints (16):
    c: Coincident(g0,g1)
    c: Coincident(g1,g2)
    c: Coincident(g2,g3)
    c: Coincident(g3,g4)
    c: Coincident(g4,g5)
    c: Coincident(g5,g0)
    c: Equal(g0, g1-g5) x5
    c: PointOnObject(g0,g6)
    c: PointOnObject(g1,g6)
    c: PointOnObject(g2,g6)
    c: PointOnObject(g3,g6)
    c: PointOnObject(g4,g6)
    c: PointOnObject(g5,g6)
    c: Horizontal(g4)
    c: DistanceY(g4,g0) = 4.06
    c: Coincident(g6,g-1)
FEATURE [PartDesign::Pocket] Pocket001006001001001002001003001003001001002001001003  label="Screw M5x20 ISO4762 8,8 A2K"
  Length = 4.06
  Length2 = 100
  Profile = -> Sketch072
  Type = 0
FEATURE [Part::Feature] Pocket001006001001001002001003001003001001002001001003001  label="Screw M5x20 ISO4762 8,8 A2K001"
  Placement = pos=(-24.5,-20.6,0) rot=(0,0,1;0rad)
  shape: bbox 9.2 x 9.2 x 25 mm, 15 faces (baked)
FEATURE [Part::Feature] Pocket001006001001001002001003001003001001002001001003001001  label="Screw M5x20 ISO4762 8,8 A2K002"
  Placement = pos=(-35,-20.6,0) rot=(0,0,1;0rad)
  shape: bbox 9.2 x 9.2 x 25 mm, 15 faces (baked)
FEATURE [Part::Feature] Pocket001006001001001002001003001003001001002001001003001002  label="Screw M5x20 ISO4762 8,8 A2K003"
  Placement = pos=(-59.5,0,0) rot=(0,0,1;0rad)
  shape: bbox 9.2 x 9.2 x 25 mm, 15 faces (baked)
FEATURE [Part::Feature] Part__Feature969  label="SHF012"
  shape: bbox 22.8 x 7.577 x 7.577 mm, 30 faces (baked)
FEATURE [Part::Feature] Part__Feature970  label="SHF013"
  shape: bbox 42 x 24 x 10 mm, 87 faces (baked)
FEATURE [App::Part] SHF010  label="SHF8_003"
  Group = -> [Part__Feature970,Part__Feature969]
  License = CC BY 3.0
  LicenseURL = http://creativecommons.org/licenses/by/3.0/
  Origin = -> Origin067
  Placement = pos=(18,336,14.7) rot=(0.889126,-0.323616,0.323616;1.68804rad)
FEATURE [Part::Feature] Part__Feature971  label="SHF014"
  shape: bbox 42 x 24 x 10 mm, 87 faces (baked)
FEATURE [Part::Feature] Part__Feature972  label="SHF015"
  shape: bbox 22.8 x 7.577 x 7.577 mm, 30 faces (baked)
FEATURE [App::Part] SHF011  label="SHF8_004"
  Group = -> [Part__Feature971,Part__Feature972]
  License = CC BY 3.0
  LicenseURL = http://creativecommons.org/licenses/by/3.0/
  Origin = -> Origin068
  Placement = pos=(53,326,14.7) rot=(0.249244,0.684791,0.684791;-2.65306rad)
FEATURE [Part::Feature] Pocket001006001001001002001003001003001001002001001003001003  label="Screw M5x20 ISO4762 8,8 A2K004"
  Placement = pos=(-59.5,0,0) rot=(0,0,1;0rad)
  shape: bbox 9.2 x 9.2 x 25 mm, 15 faces (baked)
FEATURE [Part::Feature] Pocket001006001001001002001003001003001001002001001003001004  label="Screw M5x20 ISO4762 8,8 A2K005"
  Placement = pos=(-24.5,-20.6,0) rot=(0,0,1;0rad)
  shape: bbox 9.2 x 9.2 x 25 mm, 15 faces (baked)
FEATURE [Part::Feature] Pocket001006001001001002001003001003001001002001001003001005  label="Screw M5x20 ISO4762 8,8 A2K006"
  Placement = pos=(-35,-20.6,0) rot=(0,0,1;0rad)
  shape: bbox 9.2 x 9.2 x 25 mm, 15 faces (baked)
FEATURE [Sketcher::SketchObject] Sketch073
  MapMode = 5
  Placement = pos=(0,0,0) rot=(0.57735,0.57735,0.57735;2.0944rad)
  sketch-geometry (9):
    g0: LineSegment StartX=2.499 StartY=0 StartZ=0 EndX=4.25 EndY=0 EndZ=0
    g1: LineSegment StartX=4.25 StartY=0 StartZ=0 EndX=4.25 EndY=4.97229 EndZ=0
    g2: LineSegment StartX=4.22229 StartY=5 StartZ=0 EndX=0 EndY=5 EndZ=0
    g3: LineSegment StartX=2.499 StartY=0 StartZ=0 EndX=2.5 EndY=-0.2 EndZ=0
    g4: LineSegment StartX=2.5 StartY=-0.2 StartZ=0 EndX=2.5 EndY=-19.2 EndZ=0
    g5: LineSegment StartX=2.5 StartY=-19.2 StartZ=0 EndX=1.7 EndY=-20 EndZ=0
    g6: LineSegment StartX=1.7 StartY=-20 StartZ=0 EndX=0 EndY=-20 EndZ=0
    g7: LineSegment StartX=0 StartY=-20 StartZ=0 EndX=0 EndY=5 EndZ=0
    g8: ArcOfCircle CenterX=4.22229 CenterY=4.97229 CenterZ=0 NormalX=0 NormalY=0 NormalZ=1 AngleXU=0 Radius=0.02771 StartAngle=0 EndAngle=1.5708
  constraints (26):
    c: PointOnObject(g0,g-1)
    c: Horizontal(g0)
    c: Coincident(g1,g0)
    c: Vertical(g1)
    c: Horizontal(g2)
    c: Coincident(g3,g0)
    c: Coincident(g4,g3)
    c: Vertical(g4)
    c: Coincident(g5,g4)
    c: Coincident(g6,g5)
    c: Horizontal(g6)
    c: Coincident(g7,g6)
    c: Coincident(g7,g2)
    c: Vertical(g7)
    c: Tangent(g1,g8) = -1.5708
    c: Tangent(g2,g8) = -1.5708
    c: DistanceY(g5) = -0.8
    c: DistanceX(g5) = -0.8
    c: DistanceY(g5,g3) = 19.8
    c: DistanceY(g5,g0) = 20
    c: DistanceY(g0,g2) = 5
    c: DistanceX(g2,g0) = 4.25
    c: DistanceX(g6,g4) = 2.5
    c: DistanceX(g3,g0) = -0.001
    c: PointOnObject(g-1,g7)
    c: Radius(g8) = 0.02771
FEATURE [Part::Revolution] Revolve009
  Angle = 360
  Axis = (0,0,1)
  Base = (0,0,0)
  Solid = true
  Source = -> Sketch073
  Symmetric = false
FEATURE [Sketcher::SketchObject] Sketch074
  MapMode = 5
  Placement = pos=(0,0,5) rot=(0,0,1;0rad)
  Support = -> [Revolve009]
  sketch-geometry (7):
    g0: LineSegment StartX=2.34404 StartY=0 StartZ=0 EndX=1.17202 EndY=2.03 EndZ=0
    g1: LineSegment StartX=1.17202 StartY=2.03 StartZ=0 EndX=-1.17202 EndY=2.03 EndZ=0
    g2: LineSegment StartX=-1.17202 StartY=2.03 StartZ=0 EndX=-2.34404 EndY=0 EndZ=0
    g3: LineSegment StartX=-2.34404 StartY=0 StartZ=0 EndX=-1.17202 EndY=-2.03 EndZ=0
    g4: LineSegment StartX=-1.17202 StartY=-2.03 StartZ=0 EndX=1.17202 EndY=-2.03 EndZ=0
    g5: LineSegment StartX=1.17202 StartY=-2.03 StartZ=0 EndX=2.34404 EndY=0 EndZ=0
    g6: Circle [constr] CenterX=0 CenterY=0 CenterZ=0 NormalX=0 NormalY=0 NormalZ=1 AngleXU=0 Radius=2.34404
  constraints (16):
    c: Coincident(g0,g1)
    c: Coincident(g1,g2)
    c: Coincident(g2,g3)
    c: Coincident(g3,g4)
    c: Coincident(g4,g5)
    c: Coincident(g5,g0)
    c: Equal(g0, g1-g5) x5
    c: PointOnObject(g0,g6)
    c: PointOnObject(g1,g6)
    c: PointOnObject(g2,g6)
    c: PointOnObject(g3,g6)
    c: PointOnObject(g4,g6)
    c: PointOnObject(g5,g6)
    c: Horizontal(g4)
    c: DistanceY(g4,g0) = 4.06
    c: Coincident(g6,g-1)
FEATURE [PartDesign::Pocket] Pocket001006001001001002001003001003001001002001001003001006  label="Screw M5x20 ISO4762 8,8 A2K007"
  Length = 4.06
  Length2 = 100
  Profile = -> Sketch074
  Type = 0
FEATURE [Part::Feature] Part__Feature973  label="Default"
  shape: bbox 9.238 x 9.238 x 5.02 mm, 44 faces (baked)
FEATURE [App::Part] Nyloc_Nut  label="Nyloc_Nut_M5_"
  Group = -> [Part__Feature973]
  License = CC BY 3.0
  LicenseURL = http://creativecommons.org/licenses/by/3.0/
  Origin = -> Origin071
FEATURE [Part::FeaturePython] Clone001  label="Nyloc_Nut_M5_001"  # Draft clone (typed FeaturePython)
  AttacherType = Attacher::AttachEngine3D
  Fuse = false
  Objects = -> [Nyloc_Nut]
  Placement = pos=(0,0,-15.51) rot=(0,1,0;3.14159rad)
  Scale = (1,1,1)
FEATURE [Part::FeaturePython] Clone002  label="Nyloc_Nut_M5_002"  # Draft clone (typed FeaturePython)
  AttacherType = Attacher::AttachEngine3D
  Fuse = false
  Objects = -> [Nyloc_Nut]
  Placement = pos=(-59.5,0,-15.51) rot=(0,1,0;3.14159rad)
  Scale = (1,1,1)
FEATURE [Part::FeaturePython] Clone003  label="Nyloc_Nut_M5_003"  # Draft clone (typed FeaturePython)
  AttacherType = Attacher::AttachEngine3D
  Fuse = false
  Objects = -> [Nyloc_Nut]
  Placement = pos=(-24.5,-20.6,-15.51) rot=(0,1,0;3.14159rad)
  Scale = (1,1,1)
FEATURE [Part::FeaturePython] Clone004  label="Nyloc_Nut_M5_004"  # Draft clone (typed FeaturePython)
  AttacherType = Attacher::AttachEngine3D
  Fuse = false
  Objects = -> [Nyloc_Nut]
  Placement = pos=(-35,-20.6,-15.51) rot=(0,1,0;3.14159rad)
  Scale = (1,1,1)
FEATURE [App::Part] Part046
  Group = -> [Sketch073,Sketch074,Revolve009,Pocket001006001001001002001003001003001001002001001003001006,Pocket001006001001001002001003001003001001002001001003001004,Pocket001006001001001002001003001003001001002001001003001005,Pocket001006001001001002001003001003001001002001001003001003,Clone004,Clone003,Nyloc_Nut,Clone002,Clone001]
  License = CC BY 3.0
  LicenseURL = http://creativecommons.org/licenses/by/3.0/
  Origin = -> Origin069
  Placement = pos=(65.25,339.75,4.4) rot=(-1,0,0;1.5708rad)
FEATURE [Part::Feature] Part__Feature974  label="Default001"
  shape: bbox 9.238 x 9.238 x 5.02 mm, 44 faces (baked)
FEATURE [App::Part] Nyloc_Nut001  label="Nyloc_Nut_M5_008"
  Group = -> [Part__Feature974]
  License = CC BY 3.0
  LicenseURL = http://creativecommons.org/licenses/by/3.0/
  Origin = -> Origin072
FEATURE [Part::FeaturePython] Clone005  label="Nyloc_Nut_M5_005"  # Draft clone (typed FeaturePython)
  AttacherType = Attacher::AttachEngine3D
  Fuse = false
  Objects = -> [Nyloc_Nut001]
  Placement = pos=(-35,-20.6,-15.51) rot=(0,1,0;3.14159rad)
  Scale = (1,1,1)
FEATURE [Part::FeaturePython] Clone006  label="Nyloc_Nut_M5_006"  # Draft clone (typed FeaturePython)
  AttacherType = Attacher::AttachEngine3D
  Fuse = false
  Objects = -> [Nyloc_Nut001]
  Placement = pos=(0,0,-15.51) rot=(0,1,0;3.14159rad)
  Scale = (1,1,1)
FEATURE [Part::FeaturePython] Clone007  label="Nyloc_Nut_M5_007"  # Draft clone (typed FeaturePython)
  AttacherType = Attacher::AttachEngine3D
  Fuse = false
  Objects = -> [Nyloc_Nut001]
  Placement = pos=(-24.5,-20.6,-15.51) rot=(0,1,0;3.14159rad)
  Scale = (1,1,1)
FEATURE [Part::FeaturePython] Clone008  label="Nyloc_Nut_M5_009"  # Draft clone (typed FeaturePython)
  AttacherType = Attacher::AttachEngine3D
  Fuse = false
  Objects = -> [Nyloc_Nut001]
  Placement = pos=(-59.5,0,-15.51) rot=(0,1,0;3.14159rad)
  Scale = (1,1,1)
FEATURE [App::Part] Part045
  Group = -> [Sketch071,Sketch072,Revolve008,Pocket001006001001001002001003001003001001002001001003,Pocket001006001001001002001003001003001001002001001003001,Pocket001006001001001002001003001003001001002001001003001001,Pocket001006001001001002001003001003001001002001001003001002,Clone006,Nyloc_Nut001,Clone007,Clone005,Clone008]
  License = CC BY 3.0
  LicenseURL = http://creativecommons.org/licenses/by/3.0/
  Origin = -> Origin066
  Placement = pos=(5.75,-17.75,4.4) rot=(0,-0.707107,0.707107;-3.14159rad)
FEATURE [Part::Feature] Connect001  label="GT2 20T Smooth 5mm Bore final"
  shape: bbox 18 x 18 x 8.75 mm, 24 faces (baked)
FEATURE [Sketcher::SketchObject] Sketch
  MapMode = 5
  sketch-geometry (2):
    g0: Circle CenterX=0 CenterY=0 CenterZ=0 NormalX=0 NormalY=0 NormalZ=1 AngleXU=0 Radius=5
    g1: Circle CenterX=0 CenterY=0 CenterZ=0 NormalX=0 NormalY=0 NormalZ=1 AngleXU=0 Radius=2.775
  constraints (4):
    c: Coincident(g1,g0)
    c: Coincident(g1,g-1)
    c: Radius(g0) = 5
    c: Radius(g1) = 2.775
FEATURE [PartDesign::Pad] Pad015
  Length = 1
  Length2 = 100
  Profile = -> Sketch
  Type = 0
FEATURE [App::Part] Part047  label="GT2 20T Smooth 5mm Bore final_"
  Group = -> [Connect001]
  License = CC BY 3.0
  LicenseURL = http://creativecommons.org/licenses/by/3.0/
  Origin = -> Origin073
FEATURE [App::Part] Part048  label="ISO7091DIN126_CLASS_C_M5FlatWasher_"
  Group = -> [Sketch,Pad015]
  License = CC BY 3.0
  LicenseURL = http://creativecommons.org/licenses/by/3.0/
  Origin = -> Origin074
FEATURE [Part::FeaturePython] Clone009  label="GT2 20T Smooth 5mm Bore final_001"  # Draft clone (typed FeaturePython)
  AttacherType = Attacher::AttachEngine3D
  Fuse = false
  Objects = -> [Part047]
  Placement = pos=(21.95,77.25,4.9) rot=(0,0,1;0rad)
  Scale = (1,1,1)
FEATURE [Part::FeaturePython] Clone010  label="GT2 20T Smooth 5mm Bore final_002"  # Draft clone (typed FeaturePython)
  AttacherType = Attacher::AttachEngine3D
  Fuse = false
  Objects = -> [Part047]
  Placement = pos=(49.05,77.25,4.9) rot=(0,0,1;0rad)
  Scale = (1,1,1)
FEATURE [Part::FeaturePython] Clone011  label="GT2 20T Smooth 5mm Bore final_003"  # Draft clone (typed FeaturePython)
  AttacherType = Attacher::AttachEngine3D
  Fuse = false
  Objects = -> [Part047]
  Placement = pos=(21.95,42.75,4.9) rot=(0,0,1;0rad)
  Scale = (1,1,1)
FEATURE [Part::FeaturePython] Clone012  label="GT2 20T Smooth 5mm Bore final_004"  # Draft clone (typed FeaturePython)
  AttacherType = Attacher::AttachEngine3D
  Fuse = false
  Objects = -> [Part047]
  Placement = pos=(49.05,42.75,4.9) rot=(0,0,1;0rad)
  Scale = (1,1,1)
FEATURE [Part::FeaturePython] Clone013  label="ISO7091DIN126_CLASS_C_M5FlatWasher_001"  # Draft clone (typed FeaturePython)
  AttacherType = Attacher::AttachEngine3D
  Fuse = false
  Objects = -> [Part048]
  Placement = pos=(21.95,77.25,3.75) rot=(0,0,1;0rad)
  Scale = (1,1,1)
FEATURE [Part::FeaturePython] Clone014  label="ISO7091DIN126_CLASS_C_M5FlatWasher_002"  # Draft clone (typed FeaturePython)
  AttacherType = Attacher::AttachEngine3D
  Fuse = false
  Objects = -> [Part048]
  Placement = pos=(49.05,77.25,3.75) rot=(0,0,1;0rad)
  Scale = (1,1,1)
FEATURE [Part::FeaturePython] Clone015  label="ISO7091DIN126_CLASS_C_M5FlatWasher_003"  # Draft clone (typed FeaturePython)
  AttacherType = Attacher::AttachEngine3D
  Fuse = false
  Objects = -> [Part048]
  Placement = pos=(21.95,42.75,3.75) rot=(0,0,1;0rad)
  Scale = (1,1,1)
FEATURE [Part::FeaturePython] Clone016  label="ISO7091DIN126_CLASS_C_M5FlatWasher_004"  # Draft clone (typed FeaturePython)
  AttacherType = Attacher::AttachEngine3D
  Fuse = false
  Objects = -> [Part048]
  Placement = pos=(49.05,42.75,3.75) rot=(0,0,1;0rad)
  Scale = (1,1,1)
FEATURE [Part::FeaturePython] Clone017  label="ISO7091DIN126_CLASS_C_M5FlatWasher_005"  # Draft clone (typed FeaturePython)
  AttacherType = Attacher::AttachEngine3D
  Fuse = false
  Objects = -> [Part048]
  Placement = pos=(21.95,77.25,13.53) rot=(0,0,1;0rad)
  Scale = (1,1,1)
FEATURE [Part::FeaturePython] Clone018  label="ISO7091DIN126_CLASS_C_M5FlatWasher_006"  # Draft clone (typed FeaturePython)
  AttacherType = Attacher::AttachEngine3D
  Fuse = false
  Objects = -> [Part048]
  Placement = pos=(49.05,77.25,13.53) rot=(0,0,1;0rad)
  Scale = (1,1,1)
FEATURE [Part::FeaturePython] Clone019  label="ISO7091DIN126_CLASS_C_M5FlatWasher_007"  # Draft clone (typed FeaturePython)
  AttacherType = Attacher::AttachEngine3D
  Fuse = false
  Objects = -> [Part048]
  Placement = pos=(21.95,42.75,13.53) rot=(0,0,1;0rad)
  Scale = (1,1,1)
FEATURE [Part::FeaturePython] Clone020  label="ISO7091DIN126_CLASS_C_M5FlatWasher_008"  # Draft clone (typed FeaturePython)
  AttacherType = Attacher::AttachEngine3D
  Fuse = false
  Objects = -> [Part048]
  Placement = pos=(49.05,42.75,13.53) rot=(0,0,1;0rad)
  Scale = (1,1,1)
FEATURE [Part::Box] Box025  label="Cube020"
  AttacherType = Attacher::AttachEngine3D
  Height = 6
  Length = 100
  Placement = pos=(-19,51,6) rot=(0,0,1;0rad)
  Width = 2
FEATURE [App::Part] Part041  label="x_bearing"
  Group = -> [SCV8UU001,SCV8UU002,SCV8UU003,SCV8UU,Part040,Box023,Part047,Clone010,Clone011,Clone009,Clone012,Part048,Clone013,Clone017,Clone016,Clone019,Clone015,Clone018,Clone014,Clone020,Box025]
  License = CC BY 3.0
  LicenseURL = http://creativecommons.org/licenses/by/3.0/
  Origin = -> Origin053
  Placement = pos=(0,0,37) rot=(0,0,1;0rad)
FEATURE [App::DocumentObjectGroup] Group016  label="Common"
  Group = -> [Part016,Part004]
FEATURE [Part::FeaturePython] Clone021  label="Nyloc_Nut_M5_011"  # WARN: FeaturePython — macro-defined, semantics opaque (R4)
  AttacherType = Attacher::AttachEngine3D
  Fuse = false
  Placement = pos=(21.95,77.25,-16.35) rot=(0,1,0;3.14159rad)
  Scale = (1,1,1)
FEATURE [Sketcher::SketchObject] Sketch075
  MapMode = 5
  Placement = pos=(0,0,0) rot=(0.57735,0.57735,0.57735;2.0944rad)
  sketch-geometry (9):
    g0: LineSegment StartX=2.499 StartY=0 StartZ=0 EndX=4.25 EndY=0 EndZ=0
    g1: LineSegment StartX=4.25 StartY=0 StartZ=0 EndX=4.25 EndY=4.97229 EndZ=0
    g2: LineSegment StartX=4.22229 StartY=5 StartZ=0 EndX=0 EndY=5 EndZ=0
    g3: LineSegment StartX=2.499 StartY=0 StartZ=0 EndX=2.5 EndY=-3 EndZ=0
    g4: LineSegment StartX=2.5 StartY=-3 StartZ=0 EndX=2.5 EndY=-24.2 EndZ=0
    g5: LineSegment StartX=2.5 StartY=-24.2 StartZ=0 EndX=1.7 EndY=-25 EndZ=0
    g6: LineSegment StartX=1.7 StartY=-25 StartZ=0 EndX=0 EndY=-25 EndZ=0
    g7: LineSegment StartX=0 StartY=-25 StartZ=0 EndX=0 EndY=5 EndZ=0
    g8: ArcOfCircle CenterX=4.22229 CenterY=4.97229 CenterZ=0 NormalX=0 NormalY=0 NormalZ=1 AngleXU=0 Radius=0.02771 StartAngle=0 EndAngle=1.5708
  constraints (26):
    c: PointOnObject(g0,g-1)
    c: Horizontal(g0)
    c: Coincident(g1,g0)
    c: Vertical(g1)
    c: Horizontal(g2)
    c: Coincident(g3,g0)
    c: Coincident(g4,g3)
    c: Vertical(g4)
    c: Coincident(g5,g4)
    c: Coincident(g6,g5)
    c: Horizontal(g6)
    c: Coincident(g7,g6)
    c: Coincident(g7,g2)
    c: Vertical(g7)
    c: Tangent(g1,g8) = -1.5708
    c: Tangent(g2,g8) = -1.5708
    c: DistanceY(g5) = -0.8
    c: DistanceX(g5) = -0.8
    c: DistanceY(g5,g3) = 22
    c: DistanceY(g5,g0) = 25
    c: DistanceY(g0,g2) = 5
    c: DistanceX(g2,g0) = 4.25
    c: DistanceX(g6,g4) = 2.5
    c: DistanceX(g3,g0) = -0.001
    c: PointOnObject(g-1,g7)
    c: Radius(g8) = 0.02771
FEATURE [Part::Revolution] Revolve010
  Angle = 360
  Axis = (0,0,1)
  Base = (0,0,0)
  Solid = true
  Source = -> Sketch075
  Symmetric = false
FEATURE [Sketcher::SketchObject] Sketch001
  MapMode = 5
  Placement = pos=(0,0,5) rot=(0,0,1;0rad)
  Support = -> [Revolve010]
  sketch-geometry (7):
    g0: LineSegment StartX=2.34404 StartY=0 StartZ=0 EndX=1.17202 EndY=2.03 EndZ=0
    g1: LineSegment StartX=1.17202 StartY=2.03 StartZ=0 EndX=-1.17202 EndY=2.03 EndZ=0
    g2: LineSegment StartX=-1.17202 StartY=2.03 StartZ=0 EndX=-2.34404 EndY=0 EndZ=0
    g3: LineSegment StartX=-2.34404 StartY=0 StartZ=0 EndX=-1.17202 EndY=-2.03 EndZ=0
    g4: LineSegment StartX=-1.17202 StartY=-2.03 StartZ=0 EndX=1.17202 EndY=-2.03 EndZ=0
    g5: LineSegment StartX=1.17202 StartY=-2.03 StartZ=0 EndX=2.34404 EndY=0 EndZ=0
    g6: Circle [constr] CenterX=0 CenterY=0 CenterZ=0 NormalX=0 NormalY=0 NormalZ=1 AngleXU=0 Radius=2.34404
  constraints (16):
    c: Coincident(g0,g1)
    c: Coincident(g1,g2)
    c: Coincident(g2,g3)
    c: Coincident(g3,g4)
    c: Coincident(g4,g5)
    c: Coincident(g5,g0)
    c: Equal(g0, g1-g5) x5
    c: PointOnObject(g0,g6)
    c: PointOnObject(g1,g6)
    c: PointOnObject(g2,g6)
    c: PointOnObject(g3,g6)
    c: PointOnObject(g4,g6)
    c: PointOnObject(g5,g6)
    c: Horizontal(g4)
    c: DistanceY(g4,g0) = 4.06
    c: Coincident(g6,g-1)
FEATURE [PartDesign::Pocket] Pocket  label="Screw M5x25 ISO4762 8,8 A2K"
  Length = 4.06
  Length2 = 100
  Profile = -> Sketch001
  Type = 0
FEATURE [App::Part] Part049  label="Screw M5x25 ISO4762 8,8 A2K_001"
  Group = -> [Revolve010,Sketch001,Sketch075,Pocket]
  License = CC BY 3.0
  LicenseURL = http://creativecommons.org/licenses/by/3.0/
  Origin = -> Origin075
  Placement = pos=(49.05,42.75,3.75) rot=(0,0,1;0rad)
FEATURE [Sketcher::SketchObject] Sketch076
  MapMode = 5
  Placement = pos=(0,0,0) rot=(0.57735,0.57735,0.57735;2.0944rad)
  sketch-geometry (9):
    g0: LineSegment StartX=2.499 StartY=0 StartZ=0 EndX=4.25 EndY=0 EndZ=0
    g1: LineSegment StartX=4.25 StartY=0 StartZ=0 EndX=4.25 EndY=4.97229 EndZ=0
    g2: LineSegment StartX=4.22229 StartY=5 StartZ=0 EndX=0 EndY=5 EndZ=0
    g3: LineSegment StartX=2.499 StartY=0 StartZ=0 EndX=2.5 EndY=-3 EndZ=0
    g4: LineSegment StartX=2.5 StartY=-3 StartZ=0 EndX=2.5 EndY=-24.2 EndZ=0
    g5: LineSegment StartX=2.5 StartY=-24.2 StartZ=0 EndX=1.7 EndY=-25 EndZ=0
    g6: LineSegment StartX=1.7 StartY=-25 StartZ=0 EndX=0 EndY=-25 EndZ=0
    g7: LineSegment StartX=0 StartY=-25 StartZ=0 EndX=0 EndY=5 EndZ=0
    g8: ArcOfCircle CenterX=4.22229 CenterY=4.97229 CenterZ=0 NormalX=0 NormalY=0 NormalZ=1 AngleXU=0 Radius=0.02771 StartAngle=0 EndAngle=1.5708
  constraints (26):
    c: PointOnObject(g0,g-1)
    c: Horizontal(g0)
    c: Coincident(g1,g0)
    c: Vertical(g1)
    c: Horizontal(g2)
    c: Coincident(g3,g0)
    c: Coincident(g4,g3)
    c: Vertical(g4)
    c: Coincident(g5,g4)
    c: Coincident(g6,g5)
    c: Horizontal(g6)
    c: Coincident(g7,g6)
    c: Coincident(g7,g2)
    c: Vertical(g7)
    c: Tangent(g1,g8) = -1.5708
    c: Tangent(g2,g8) = -1.5708
    c: DistanceY(g5) = -0.8
    c: DistanceX(g5) = -0.8
    c: DistanceY(g5,g3) = 22
    c: DistanceY(g5,g0) = 25
    c: DistanceY(g0,g2) = 5
    c: DistanceX(g2,g0) = 4.25
    c: DistanceX(g6,g4) = 2.5
    c: DistanceX(g3,g0) = -0.001
    c: PointOnObject(g-1,g7)
    c: Radius(g8) = 0.02771
FEATURE [Part::Revolution] Revolve011
  Angle = 360
  Axis = (0,0,1)
  Base = (0,0,0)
  Solid = true
  Source = -> Sketch076
  Symmetric = false
FEATURE [Sketcher::SketchObject] Sketch077
  MapMode = 5
  Placement = pos=(0,0,5) rot=(0,0,1;0rad)
  Support = -> [Revolve011]
  sketch-geometry (7):
    g0: LineSegment StartX=2.34404 StartY=0 StartZ=0 EndX=1.17202 EndY=2.03 EndZ=0
    g1: LineSegment StartX=1.17202 StartY=2.03 StartZ=0 EndX=-1.17202 EndY=2.03 EndZ=0
    g2: LineSegment StartX=-1.17202 StartY=2.03 StartZ=0 EndX=-2.34404 EndY=0 EndZ=0
    g3: LineSegment StartX=-2.34404 StartY=0 StartZ=0 EndX=-1.17202 EndY=-2.03 EndZ=0
    g4: LineSegment StartX=-1.17202 StartY=-2.03 StartZ=0 EndX=1.17202 EndY=-2.03 EndZ=0
    g5: LineSegment StartX=1.17202 StartY=-2.03 StartZ=0 EndX=2.34404 EndY=0 EndZ=0
    g6: Circle [constr] CenterX=0 CenterY=0 CenterZ=0 NormalX=0 NormalY=0 NormalZ=1 AngleXU=0 Radius=2.34404
  constraints (16):
    c: Coincident(g0,g1)
    c: Coincident(g1,g2)
    c: Coincident(g2,g3)
    c: Coincident(g3,g4)
    c: Coincident(g4,g5)
    c: Coincident(g5,g0)
    c: Equal(g0, g1-g5) x5
    c: PointOnObject(g0,g6)
    c: PointOnObject(g1,g6)
    c: PointOnObject(g2,g6)
    c: PointOnObject(g3,g6)
    c: PointOnObject(g4,g6)
    c: PointOnObject(g5,g6)
    c: Horizontal(g4)
    c: DistanceY(g4,g0) = 4.06
    c: Coincident(g6,g-1)
FEATURE [PartDesign::Pocket] Pocket001006001001001002001003001003001001002001001003001007  label="Screw M5x25 ISO4762 8,8 A2K001"
  Length = 4.06
  Length2 = 100
  Profile = -> Sketch077
  Type = 0
FEATURE [App::Part] Part050  label="Screw M5x25 ISO4762 8,8 A2K_002"
  Group = -> [Revolve011,Sketch077,Sketch076,Pocket001006001001001002001003001003001001002001001003001007]
  License = CC BY 3.0
  LicenseURL = http://creativecommons.org/licenses/by/3.0/
  Origin = -> Origin077
  Placement = pos=(21.95,42.75,3.75) rot=(0,0,1;0rad)
FEATURE [Sketcher::SketchObject] Sketch078
  MapMode = 5
  Placement = pos=(0,0,0) rot=(0.57735,0.57735,0.57735;2.0944rad)
  sketch-geometry (9):
    g0: LineSegment StartX=2.499 StartY=0 StartZ=0 EndX=4.25 EndY=0 EndZ=0
    g1: LineSegment StartX=4.25 StartY=0 StartZ=0 EndX=4.25 EndY=4.97229 EndZ=0
    g2: LineSegment StartX=4.22229 StartY=5 StartZ=0 EndX=0 EndY=5 EndZ=0
    g3: LineSegment StartX=2.499 StartY=0 StartZ=0 EndX=2.5 EndY=-3 EndZ=0
    g4: LineSegment StartX=2.5 StartY=-3 StartZ=0 EndX=2.5 EndY=-24.2 EndZ=0
    g5: LineSegment StartX=2.5 StartY=-24.2 StartZ=0 EndX=1.7 EndY=-25 EndZ=0
    g6: LineSegment StartX=1.7 StartY=-25 StartZ=0 EndX=0 EndY=-25 EndZ=0
    g7: LineSegment StartX=0 StartY=-25 StartZ=0 EndX=0 EndY=5 EndZ=0
    g8: ArcOfCircle CenterX=4.22229 CenterY=4.97229 CenterZ=0 NormalX=0 NormalY=0 NormalZ=1 AngleXU=0 Radius=0.02771 StartAngle=0 EndAngle=1.5708
  constraints (26):
    c: PointOnObject(g0,g-1)
    c: Horizontal(g0)
    c: Coincident(g1,g0)
    c: Vertical(g1)
    c: Horizontal(g2)
    c: Coincident(g3,g0)
    c: Coincident(g4,g3)
    c: Vertical(g4)
    c: Coincident(g5,g4)
    c: Coincident(g6,g5)
    c: Horizontal(g6)
    c: Coincident(g7,g6)
    c: Coincident(g7,g2)
    c: Vertical(g7)
    c: Tangent(g1,g8) = -1.5708
    c: Tangent(g2,g8) = -1.5708
    c: DistanceY(g5) = -0.8
    c: DistanceX(g5) = -0.8
    c: DistanceY(g5,g3) = 22
    c: DistanceY(g5,g0) = 25
    c: DistanceY(g0,g2) = 5
    c: DistanceX(g2,g0) = 4.25
    c: DistanceX(g6,g4) = 2.5
    c: DistanceX(g3,g0) = -0.001
    c: PointOnObject(g-1,g7)
    c: Radius(g8) = 0.02771
FEATURE [Part::Revolution] Revolve012
  Angle = 360
  Axis = (0,0,1)
  Base = (0,0,0)
  Solid = true
  Source = -> Sketch078
  Symmetric = false
FEATURE [Sketcher::SketchObject] Sketch079
  MapMode = 5
  Placement = pos=(0,0,5) rot=(0,0,1;0rad)
  Support = -> [Revolve012]
  sketch-geometry (7):
    g0: LineSegment StartX=2.34404 StartY=0 StartZ=0 EndX=1.17202 EndY=2.03 EndZ=0
    g1: LineSegment StartX=1.17202 StartY=2.03 StartZ=0 EndX=-1.17202 EndY=2.03 EndZ=0
    g2: LineSegment StartX=-1.17202 StartY=2.03 StartZ=0 EndX=-2.34404 EndY=0 EndZ=0
    g3: LineSegment StartX=-2.34404 StartY=0 StartZ=0 EndX=-1.17202 EndY=-2.03 EndZ=0
    g4: LineSegment StartX=-1.17202 StartY=-2.03 StartZ=0 EndX=1.17202 EndY=-2.03 EndZ=0
    g5: LineSegment StartX=1.17202 StartY=-2.03 StartZ=0 EndX=2.34404 EndY=0 EndZ=0
    g6: Circle [constr] CenterX=0 CenterY=0 CenterZ=0 NormalX=0 NormalY=0 NormalZ=1 AngleXU=0 Radius=2.34404
  constraints (16):
    c: Coincident(g0,g1)
    c: Coincident(g1,g2)
    c: Coincident(g2,g3)
    c: Coincident(g3,g4)
    c: Coincident(g4,g5)
    c: Coincident(g5,g0)
    c: Equal(g0, g1-g5) x5
    c: PointOnObject(g0,g6)
    c: PointOnObject(g1,g6)
    c: PointOnObject(g2,g6)
    c: PointOnObject(g3,g6)
    c: PointOnObject(g4,g6)
    c: PointOnObject(g5,g6)
    c: Horizontal(g4)
    c: DistanceY(g4,g0) = 4.06
    c: Coincident(g6,g-1)
FEATURE [PartDesign::Pocket] Pocket001006001001001002001003001003001001002001001003001008  label="Screw M5x25 ISO4762 8,8 A2K002"
  Length = 4.06
  Length2 = 100
  Profile = -> Sketch079
  Type = 0
FEATURE [App::Part] Part051  label="Screw M5x25 ISO4762 8,8 A2K_003"
  Group = -> [Revolve012,Sketch079,Sketch078,Pocket001006001001001002001003001003001001002001001003001008]
  License = CC BY 3.0
  LicenseURL = http://creativecommons.org/licenses/by/3.0/
  Origin = -> Origin078
  Placement = pos=(49.05,77.25,3.75) rot=(0,0,1;0rad)
FEATURE [Sketcher::SketchObject] Sketch080
  MapMode = 5
  Placement = pos=(0,0,0) rot=(0.57735,0.57735,0.57735;2.0944rad)
  sketch-geometry (9):
    g0: LineSegment StartX=2.499 StartY=0 StartZ=0 EndX=4.25 EndY=0 EndZ=0
    g1: LineSegment StartX=4.25 StartY=0 StartZ=0 EndX=4.25 EndY=4.97229 EndZ=0
    g2: LineSegment StartX=4.22229 StartY=5 StartZ=0 EndX=0 EndY=5 EndZ=0
    g3: LineSegment StartX=2.499 StartY=0 StartZ=0 EndX=2.5 EndY=-3 EndZ=0
    g4: LineSegment StartX=2.5 StartY=-3 StartZ=0 EndX=2.5 EndY=-24.2 EndZ=0
    g5: LineSegment StartX=2.5 StartY=-24.2 StartZ=0 EndX=1.7 EndY=-25 EndZ=0
    g6: LineSegment StartX=1.7 StartY=-25 StartZ=0 EndX=0 EndY=-25 EndZ=0
    g7: LineSegment StartX=0 StartY=-25 StartZ=0 EndX=0 EndY=5 EndZ=0
    g8: ArcOfCircle CenterX=4.22229 CenterY=4.97229 CenterZ=0 NormalX=0 NormalY=0 NormalZ=1 AngleXU=0 Radius=0.02771 StartAngle=0 EndAngle=1.5708
  constraints (26):
    c: PointOnObject(g0,g-1)
    c: Horizontal(g0)
    c: Coincident(g1,g0)
    c: Vertical(g1)
    c: Horizontal(g2)
    c: Coincident(g3,g0)
    c: Coincident(g4,g3)
    c: Vertical(g4)
    c: Coincident(g5,g4)
    c: Coincident(g6,g5)
    c: Horizontal(g6)
    c: Coincident(g7,g6)
    c: Coincident(g7,g2)
    c: Vertical(g7)
    c: Tangent(g1,g8) = -1.5708
    c: Tangent(g2,g8) = -1.5708
    c: DistanceY(g5) = -0.8
    c: DistanceX(g5) = -0.8
    c: DistanceY(g5,g3) = 22
    c: DistanceY(g5,g0) = 25
    c: DistanceY(g0,g2) = 5
    c: DistanceX(g2,g0) = 4.25
    c: DistanceX(g6,g4) = 2.5
    c: DistanceX(g3,g0) = -0.001
    c: PointOnObject(g-1,g7)
    c: Radius(g8) = 0.02771
FEATURE [Part::Revolution] Revolve013
  Angle = 360
  Axis = (0,0,1)
  Base = (0,0,0)
  Solid = true
  Source = -> Sketch080
  Symmetric = false
FEATURE [Sketcher::SketchObject] Sketch081
  MapMode = 5
  Placement = pos=(0,0,5) rot=(0,0,1;0rad)
  Support = -> [Revolve013]
  sketch-geometry (7):
    g0: LineSegment StartX=2.34404 StartY=0 StartZ=0 EndX=1.17202 EndY=2.03 EndZ=0
    g1: LineSegment StartX=1.17202 StartY=2.03 StartZ=0 EndX=-1.17202 EndY=2.03 EndZ=0
    g2: LineSegment StartX=-1.17202 StartY=2.03 StartZ=0 EndX=-2.34404 EndY=0 EndZ=0
    g3: LineSegment StartX=-2.34404 StartY=0 StartZ=0 EndX=-1.17202 EndY=-2.03 EndZ=0
    g4: LineSegment StartX=-1.17202 StartY=-2.03 StartZ=0 EndX=1.17202 EndY=-2.03 EndZ=0
    g5: LineSegment StartX=1.17202 StartY=-2.03 StartZ=0 EndX=2.34404 EndY=0 EndZ=0
    g6: Circle [constr] CenterX=0 CenterY=0 CenterZ=0 NormalX=0 NormalY=0 NormalZ=1 AngleXU=0 Radius=2.34404
  constraints (16):
    c: Coincident(g0,g1)
    c: Coincident(g1,g2)
    c: Coincident(g2,g3)
    c: Coincident(g3,g4)
    c: Coincident(g4,g5)
    c: Coincident(g5,g0)
    c: Equal(g0, g1-g5) x5
    c: PointOnObject(g0,g6)
    c: PointOnObject(g1,g6)
    c: PointOnObject(g2,g6)
    c: PointOnObject(g3,g6)
    c: PointOnObject(g4,g6)
    c: PointOnObject(g5,g6)
    c: Horizontal(g4)
    c: DistanceY(g4,g0) = 4.06
    c: Coincident(g6,g-1)
FEATURE [PartDesign::Pocket] Pocket001006001001001002001003001003001001002001001003001009  label="Screw M5x25 ISO4762 8,8 A2K003"
  Length = 4.06
  Length2 = 100
  Profile = -> Sketch081
  Type = 0
FEATURE [App::Part] Part052  label="Screw M5x25 ISO4762 8,8 A2K_004"
  Group = -> [Revolve013,Sketch081,Sketch080,Pocket001006001001001002001003001003001001002001001003001009]
  License = CC BY 3.0
  LicenseURL = http://creativecommons.org/licenses/by/3.0/
  Origin = -> Origin079
  Placement = pos=(21.95,77.25,3.75) rot=(0,0,1;0rad)
FEATURE [Part::FeaturePython] Clone022  label="Nyloc_Nut_M5_012"  # WARN: FeaturePython — macro-defined, semantics opaque (R4)
  AttacherType = Attacher::AttachEngine3D
  Fuse = false
  Placement = pos=(49.05,42.75,-16.35) rot=(0,1,0;3.14159rad)
  Scale = (1,1,1)
FEATURE [Part::FeaturePython] Clone023  label="Nyloc_Nut_M5_013"  # WARN: FeaturePython — macro-defined, semantics opaque (R4)
  AttacherType = Attacher::AttachEngine3D
  Fuse = false
  Placement = pos=(21.95,42.75,-16.35) rot=(0,1,0;3.14159rad)
  Scale = (1,1,1)
FEATURE [Part::FeaturePython] Clone024  label="Nyloc_Nut_M5_014"  # WARN: FeaturePython — macro-defined, semantics opaque (R4)
  AttacherType = Attacher::AttachEngine3D
  Fuse = false
  Placement = pos=(49.05,77.25,-16.35) rot=(0,1,0;3.14159rad)
  Scale = (1,1,1)
FEATURE [Part::Feature] Part__Feature976  label="Default003"
  shape: bbox 33 x 59.5 x 33 mm, 139 faces (baked)
FEATURE [Mesh::Feature] Laser_Mount
  Placement = pos=(7.5,-10,-23) rot=(1,0,0;1.5708rad)
FEATURE [App::Part] Elesmaker_2_300_mw
  Group = -> [Part__Feature976]
  License = CC BY 3.0
  LicenseURL = http://creativecommons.org/licenses/by/3.0/
  Origin = -> Origin080
  Placement = pos=(35.5,-40,-27) rot=(1,0,0;1.5708rad)
FEATURE [App::Part] Part053  label="Laser"
  Group = -> [Laser_Mount,Elesmaker_2_300_mw]
  License = CC BY 3.0
  LicenseURL = http://creativecommons.org/licenses/by/3.0/
  Origin = -> Origin081
FEATURE [App::DocumentObjectGroup] Group011  label="Tools"
  Group = -> [Part053]
FEATURE [App::Part] Part044
  Group = -> [Box021,Cylinder002,Cylinder003,SHF8,SHF009,Box024,Part045,SHF010,SHF011,Part046,Group011,Part053]
  License = CC BY 3.0
  LicenseURL = http://creativecommons.org/licenses/by/3.0/
  Origin = -> Origin062
  Placement = pos=(0,-75,0) rot=(0,0,1;0rad)
FEATURE [App::Part] Part042  label="y_bearing"
  Group = -> [Box022,SCV8UU004,SCV8UU005,SCV8UU006,SCV8UU007,Part043,Part044,Part049,Part050,Part051,Part052,Clone021,Clone022,Clone023,Clone024]
  License = CC BY 3.0
  LicenseURL = http://creativecommons.org/licenses/by/3.0/
  Origin = -> Origin054
  Placement = pos=(0,0,51.55) rot=(0,0,1;0rad)
FEATURE [App::Part] Part038  label="Carriage"
  Group = -> [Part041,Part042]
  License = CC BY 3.0
  LicenseURL = http://creativecommons.org/licenses/by/3.0/
  Origin = -> Origin042
  Placement = pos=(239,0,0) rot=(0,0,1;0rad)
FEATURE [App::DocumentObjectGroup] Group008  label="Axes"
  Group = -> [Group009,Part038]
FEATURE [App::DocumentObjectGroup] Group001  label="Mechanics"
  Group = -> [Group004,Group008]
